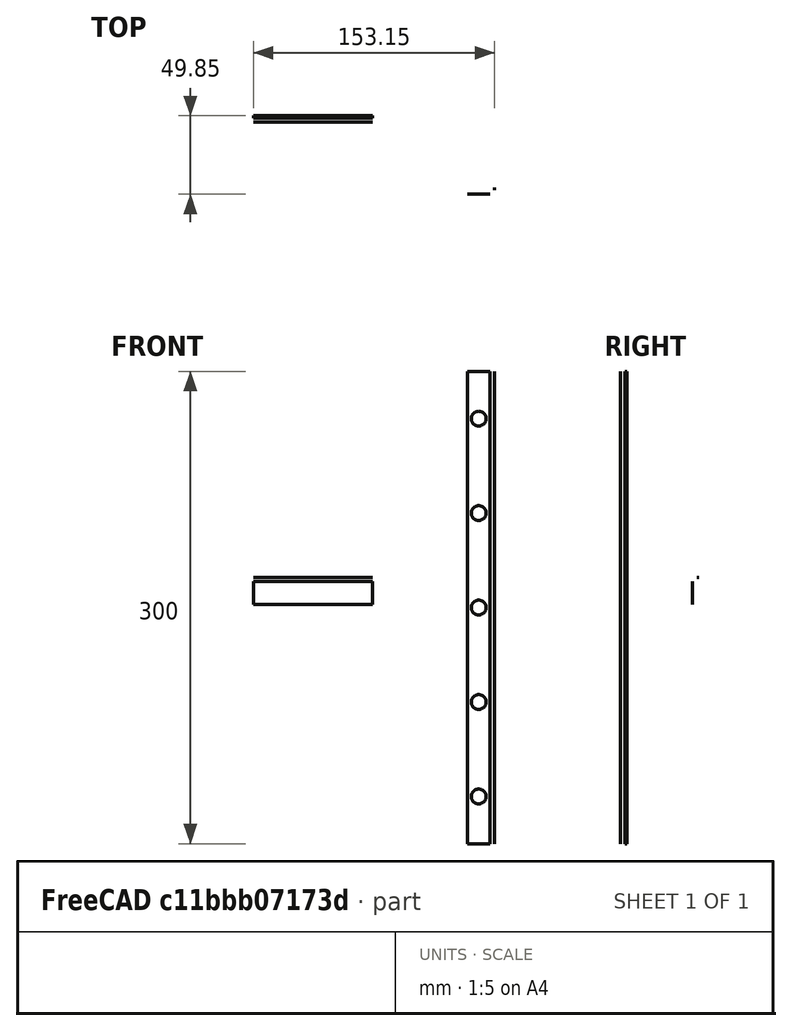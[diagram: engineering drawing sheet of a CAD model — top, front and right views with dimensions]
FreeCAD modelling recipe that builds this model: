
FCSTD DOCUMENT  (FreeCAD 2021.717R24301 +3842 (Git))
Label: Z-axis
License: Creative Commons Attribution
LicenseURL: http://creativecommons.org/licenses/by/4.0/
objects: App::FeaturePython×43, Part::FeaturePython×38, App::Link×14
note: 37 computed .brp shape members not serialized (recipe doc carries the construction recipe); baked Part::Feature solids carry a one-line shape summary decoded from their .brp
EXTERNAL_REF file=parts/Ballscrew.FCStd obj=Assembly002
EXTERNAL_REF file=parts/Z axis plates.FCStd obj=Assembly
EXTERNAL_REF file=parts/HGR20.FCStd obj=Assembly
EXTERNAL_REF file=parts/Z axis plates.FCStd obj=Assembly004
EXTERNAL_REF file=parts/NEMA23-76.FCStd obj=Assembly
EXTERNAL_REF file=parts/NEMA23-76.FCStd obj=Assembly001
EXTERNAL_REF file=parts/BallNut.FCStd obj=Assembly
EXTERNAL_REF file=parts/Z axis plates.FCStd obj=Assembly005
EXTERNAL_REF file=parts/HGH20CA.FCStd obj=Assembly
EXTERNAL_REF file=parts/HGH20CA.FCStd obj=Assembly001
EXTERNAL_REF file=parts/LimitSensor.FCStd obj=Assembly

FEATURE [App::Link] Link007  label="Ballscrew"
  AutoLinkLabel = true
  AutoPlacement = true
  LinkPlacement = pos=(0.026908,-40.4231,-69.025) rot=(-1,0,0;4.71239rad)
  LinkedObject = -> <external parts/Ballscrew.FCStd>#Assembly002
  Placement = pos=(0.026908,-40.4231,-69.025) rot=(-1,0,0;4.71239rad)
  SyncGroupVisibility = false
  _LinkVersion = 1
FEATURE [App::Link] Link  label="Backplate"
  AutoLinkLabel = true
  AutoPlacement = true
  LinkedObject = -> <external parts/Z axis plates.FCStd>#Assembly
  SyncGroupVisibility = false
  _LinkVersion = 1
FEATURE [App::Link] Link011  label="HGR20-300-R"
  AutoLinkLabel = true
  AutoPlacement = true
  LinkPlacement = pos=(54,-15.7,-6.00267e-11) rot=(1,0,0;1.5708rad)
  LinkedObject = -> <external parts/HGR20.FCStd>#Assembly
  Placement = pos=(54,-15.7,-6.00267e-11) rot=(1,0,0;1.5708rad)
  SyncGroupVisibility = false
  _LinkVersion = 1
FEATURE [App::Link] Link012  label="HGR20-300-L"
  AutoLinkLabel = true
  AutoPlacement = true
  LinkPlacement = pos=(-54,-15.7,-5.99982e-11) rot=(1,0,0;1.5708rad)
  LinkedObject = -> <external parts/HGR20.FCStd>#Assembly
  Placement = pos=(-54,-15.7,-5.99982e-11) rot=(1,0,0;1.5708rad)
  SyncGroupVisibility = false
  _LinkVersion = 1
FEATURE [App::Link] Link017  label="Motor Bracket"
  AutoLinkLabel = true
  AutoPlacement = true
  LinkedObject = -> <external parts/Z axis plates.FCStd>#Assembly004
  SyncGroupVisibility = false
  _LinkVersion = 1
FEATURE [App::Link] Link018  label="NEMA23-76"
  AutoLinkLabel = true
  AutoPlacement = true
  LinkPlacement = pos=(0,-40.7,158.85) rot=(0,0,1;3.14159rad)
  LinkedObject = -> <external parts/NEMA23-76.FCStd>#Assembly
  Placement = pos=(0,-40.7,158.85) rot=(0,0,1;3.14159rad)
  SyncGroupVisibility = false
  _LinkVersion = 1
FEATURE [App::Link] Link019  label="Coupling"
  AutoLinkLabel = true
  AutoPlacement = true
  LinkPlacement = pos=(3e-16,-40.7,131.25) rot=(0,1,0;3.14159rad)
  LinkedObject = -> <external parts/NEMA23-76.FCStd>#Assembly001
  Placement = pos=(3e-16,-40.7,131.25) rot=(0,1,0;3.14159rad)
  SyncGroupVisibility = false
  _LinkVersion = 1
FEATURE [App::Link] Link026  label="X-Nut"
  AutoLinkLabel = true
  AutoPlacement = true
  LinkPlacement = pos=(9.875,36.75,-60.65) rot=(-0.57735,-0.57735,-0.57735;2.0944rad)
  LinkedObject = -> <external parts/BallNut.FCStd>#Assembly
  Placement = pos=(9.875,36.75,-60.65) rot=(-0.57735,-0.57735,-0.57735;2.0944rad)
  SyncGroupVisibility = false
  _LinkVersion = 1
FEATURE [App::Link] Link027  label="Nut-shim-X"
  AutoLinkLabel = true
  AutoPlacement = true
  LinkPlacement = pos=(35.475,-6.6e-15,68.35) rot=(0,1,0;4.71239rad)
  LinkedObject = -> <external parts/Z axis plates.FCStd>#Assembly005
  Placement = pos=(35.475,-6.6e-15,68.35) rot=(0,1,0;4.71239rad)
  SyncGroupVisibility = false
  _LinkVersion = 1
FEATURE [App::Link] Link028  label="HGH20CA-L-B"
  AutoLinkLabel = true
  AutoPlacement = true
  LinkPlacement = pos=(-51.25,30,-130.5) rot=(0.57735,0.57735,-0.57735;2.0944rad)
  LinkedObject = -> <external parts/HGH20CA.FCStd>#Assembly
  Placement = pos=(-51.25,30,-130.5) rot=(0.57735,0.57735,-0.57735;2.0944rad)
  SyncGroupVisibility = false
  _LinkVersion = 1
FEATURE [App::Link] Link029  label="HGH20CA-R-B"
  AutoLinkLabel = true
  AutoPlacement = true
  LinkPlacement = pos=(51.25,30,-130.5) rot=(0.57735,0.57735,-0.57735;2.0944rad)
  LinkedObject = -> <external parts/HGH20CA.FCStd>#Assembly001
  Placement = pos=(51.25,30,-130.5) rot=(0.57735,0.57735,-0.57735;2.0944rad)
  SyncGroupVisibility = false
  _LinkVersion = 1
FEATURE [App::Link] Link030  label="HGH20CA-R-T"
  AutoLinkLabel = true
  AutoPlacement = true
  LinkPlacement = pos=(51.25,30,9.2) rot=(0.57735,-0.57735,0.57735;2.0944rad)
  LinkedObject = -> <external parts/HGH20CA.FCStd>#Assembly
  Placement = pos=(51.25,30,9.2) rot=(0.57735,-0.57735,0.57735;2.0944rad)
  SyncGroupVisibility = false
  _LinkVersion = 1
FEATURE [App::Link] Link031  label="HGH20CA-L-T"
  AutoLinkLabel = true
  AutoPlacement = true
  LinkPlacement = pos=(-51.25,30,9.2) rot=(0.57735,-0.57735,0.57735;2.0944rad)
  LinkedObject = -> <external parts/HGH20CA.FCStd>#Assembly001
  Placement = pos=(-51.25,30,9.2) rot=(0.57735,-0.57735,0.57735;2.0944rad)
  SyncGroupVisibility = false
  _LinkVersion = 1
FEATURE [App::Link] Link032  label="Limit sensor"
  AutoLinkLabel = true
  AutoPlacement = true
  LinkPlacement = pos=(-54,-61.85,152.5) rot=(0,0.707107,0.707107;3.14159rad)
  LinkedObject = -> <external parts/LimitSensor.FCStd>#Assembly
  Placement = pos=(-54,-61.85,152.5) rot=(0,0.707107,0.707107;3.14159rad)
  SyncGroupVisibility = false
  _LinkVersion = 1
FEATURE [Part::FeaturePython] Parts  # WARN: FeaturePython — macro-defined, semantics opaque (R4)
  Group = -> [Link007,Link,Link011,Link012,Link017,Link018,Link019,Link026,Link027,Link028,Link029,Link030,Link031,Link032]
  GroupMode = 0
  _LinkVersion = 1
FEATURE [Part::FeaturePython] Assembly  label="Z-axis assembly"  # WARN: FeaturePython — macro-defined, semantics opaque (R4)
  AutoRelax = true
  BuildShape = 0
  Freeze = false
  Group = -> [Constraints,Elements,Parts]
  Verbose = false
  _LinkVersion = 1
  _SolverType = 1
  _Version = 1
FEATURE [App::FeaturePython] Elements  # WARN: FeaturePython — macro-defined, semantics opaque (R4)
  Group = -> [Element,Element001,Element002,Element004,Element005,Element006,Element007,Element009,Element011,Element033,Element034,Element035,Element036,Element037,Element039,Element040,Element041,Element042,Element043,Element044,Element053,Element054,Element055,Element056,Element057,Element058,Element059,Element060,Element061,Element062,Element063,Element064,_Element,_Element001,Element065,_Element002]
  _LinkVersion = 1
FEATURE [Part::FeaturePython] Element  label="rail-tr@Backplate-Assembly"  # link proxy (typed FeaturePython)
  Detach = false
  LinkTransform = true
  LinkedObject = -> Link [1.$rail-tr.]
  _LinkVersion = 1
  _Parent = -> Elements
FEATURE [Part::FeaturePython] Element001  label="rail-bl@Backplate-Assembly"  # link proxy (typed FeaturePython)
  Detach = false
  LinkTransform = true
  LinkedObject = -> Link [1.$rail-tl.]
  _LinkVersion = 1
  _Parent = -> Elements
FEATURE [Part::FeaturePython] Element002  label="screw-br@Backplate-Assembly"  # link proxy (typed FeaturePython)
  Detach = false
  LinkTransform = true
  LinkedObject = -> Link [1.$screw-br.]
  _LinkVersion = 1
  _Parent = -> Elements
FEATURE [Part::FeaturePython] Element004  label="BP-mate@Ballscrew-Assembly"  # link proxy (typed FeaturePython)
  Detach = false
  LinkTransform = true
  LinkedObject = -> Link007 [1.$BP-mate.]
  _LinkVersion = 1
  _Parent = -> Elements
FEATURE [Part::FeaturePython] Element005  label="BP-mate-r@HGR20-300-Assembly"  # link proxy (typed FeaturePython)
  Detach = false
  LinkTransform = true
  LinkedObject = -> Link011 [1.$BP-mate-r.]
  _LinkVersion = 1
  _Parent = -> Elements
FEATURE [Part::FeaturePython] Element006  label="r-mate@HGR20-300-Assembly"  # link proxy (typed FeaturePython)
  Detach = false
  LinkTransform = true
  LinkedObject = -> Link011 [1.$r-mate.]
  _LinkVersion = 1
  _Parent = -> Elements
FEATURE [Part::FeaturePython] Element007  label="top-mate@HGR20-300-Assembly"  # link proxy (typed FeaturePython)
  Detach = false
  LinkTransform = true
  LinkedObject = -> Link011 [1.$top-mate.]
  _LinkVersion = 1
  _Parent = -> Elements
FEATURE [Part::FeaturePython] Element009  label="BP-mate-r@HGR20-300-Assembly001"  # link proxy (typed FeaturePython)
  Detach = false
  LinkTransform = true
  LinkedObject = -> Link012 [1.$BP-mate-r.]
  _LinkVersion = 1
  _Parent = -> Elements
FEATURE [Part::FeaturePython] Element011  label="Axis@Ballscrew-Assembly"  # link proxy (typed FeaturePython)
  Detach = false
  LinkTransform = true
  LinkedObject = -> Link007 [1.$Axis.]
  _LinkVersion = 1
  _Parent = -> Elements
FEATURE [Part::FeaturePython] Element033  label="point@HGR20-300-Assembly"  # link proxy (typed FeaturePython)
  Detach = false
  LinkTransform = true
  LinkedObject = -> Link011 [1.$point.]
  _LinkVersion = 1
  _Parent = -> Elements
FEATURE [App::FeaturePython] ElementLink  label="rail-tr@Backplate-Assembly"  # link proxy (typed FeaturePython)
  LinkTransform = true
  LinkedObject = -> Element
  _LinkVersion = 1
  _Parent = -> Constraint
FEATURE [App::FeaturePython] Constraint  label="Locked"  # WARN: FeaturePython — macro-defined, semantics opaque (R4)
  Disabled = false
  Group = -> [ElementLink]
  _ConstraintType = 0
  _LinkVersion = 1
  _Parent = -> Constraints
FEATURE [App::FeaturePython] ElementLink002  label="screw-br@Backplate-Assembly"  # link proxy (typed FeaturePython)
  LinkTransform = true
  LinkedObject = -> Element002
  Offset = pos=(0,0,0) rot=(0,0,1;3.14159rad)
  Placement = pos=(46,5.33e-14,-241.05) rot=(0,1,0;3.14159rad)
  _LinkVersion = 1
  _Parent = -> Constraint001
FEATURE [App::FeaturePython] ElementLink007  label="BP-mate@Ballscrew-Assembly"  # link proxy (typed FeaturePython)
  LinkTransform = true
  LinkedObject = -> Element004
  Offset = pos=(0,0,0) rot=(1,0,0;3.14159rad)
  Placement = pos=(-2.84e-14,-31.4,-241.05) rot=(1,0,0;3.14159rad)
  _LinkVersion = 1
  _Parent = -> Constraint001
FEATURE [App::FeaturePython] Constraint001  label="Attachment-BP-Screw"  # WARN: FeaturePython — macro-defined, semantics opaque (R4)
  Cascade = false
  Disabled = false
  Group = -> [ElementLink002,ElementLink007]
  Multiply = false
  _ConstraintType = 45
  _LinkVersion = 1
  _Parent = -> Constraints
FEATURE [App::FeaturePython] ElementLink008  label="rail-tr@Backplate-Assembly"  # link proxy (typed FeaturePython)
  LinkTransform = true
  LinkedObject = -> Element
  _LinkVersion = 1
  _Parent = -> Constraint002
FEATURE [App::FeaturePython] ElementLink009  label="BP-mate-r@HGR20-300-Assembly"  # link proxy (typed FeaturePython)
  LinkTransform = true
  LinkedObject = -> Element005
  Offset = pos=(0,0,0) rot=(0,0,1;3.14159rad)
  Placement = pos=(108,5.51e-14,240) rot=(0,1,0;3.14159rad)
  _LinkVersion = 1
  _Parent = -> Constraint002
FEATURE [App::FeaturePython] Constraint002  label="Attachment-BP-rail-r"  # WARN: FeaturePython — macro-defined, semantics opaque (R4)
  Cascade = false
  Disabled = false
  Group = -> [ElementLink008,ElementLink009]
  Multiply = false
  _ConstraintType = 45
  _LinkVersion = 1
  _Parent = -> Constraints
FEATURE [App::FeaturePython] ElementLink010  label="rail-bl@Backplate-Assembly"  # link proxy (typed FeaturePython)
  LinkTransform = true
  LinkedObject = -> Element001
  _LinkVersion = 1
  _Parent = -> Constraint003
FEATURE [App::FeaturePython] ElementLink011  label="BP-mate-r@HGR20-300-Assembly001"  # link proxy (typed FeaturePython)
  LinkTransform = true
  LinkedObject = -> Element009
  _LinkVersion = 1
  _Parent = -> Constraint003
FEATURE [App::FeaturePython] Constraint003  label="Attachment-BP-rail-l"  # WARN: FeaturePython — macro-defined, semantics opaque (R4)
  Cascade = false
  Disabled = false
  Group = -> [ElementLink010,ElementLink011]
  Multiply = false
  _ConstraintType = 45
  _LinkVersion = 1
  _Parent = -> Constraints
FEATURE [App::FeaturePython] Constraints  # WARN: FeaturePython — macro-defined, semantics opaque (R4)
  Group = -> [Constraint,Constraint001,Constraint002,Constraint003,Constraint016,Constraint017,Constraint018,Constraint019,Constraint020,Constraint023,Constraint025,Constraint026,Constraint027,Constraint028]
  _LinkVersion = 1
  _Version = 1
FEATURE [Part::FeaturePython] Element034  label="bp-mate@Motor Bracket Assembly"  # link proxy (typed FeaturePython)
  Detach = false
  LinkTransform = true
  LinkedObject = -> Link017 [1.$bp-mate.]
  _LinkVersion = 1
  _Parent = -> Elements
FEATURE [Part::FeaturePython] Element035  label="Motor-mate@Motor Bracket Assembly"  # link proxy (typed FeaturePython)
  Detach = false
  LinkTransform = true
  LinkedObject = -> Link017 [1.$Motor-mate.]
  _LinkVersion = 1
  _Parent = -> Elements
FEATURE [Part::FeaturePython] Element036  label="bracket-mate@Backplate-Assembly"  # link proxy (typed FeaturePython)
  Detach = false
  LinkTransform = true
  LinkedObject = -> Link [1.$bracket-mate.]
  _LinkVersion = 1
  _Parent = -> Elements
FEATURE [App::FeaturePython] Constraint016  label="Attachment-BP-bracket"  # WARN: FeaturePython — macro-defined, semantics opaque (R4)
  Cascade = false
  Disabled = false
  Group = -> [ElementLink036,ElementLink037]
  Multiply = false
  _ConstraintType = 45
  _LinkVersion = 1
  _Parent = -> Constraints
FEATURE [App::FeaturePython] ElementLink036  label="bracket-mate@Backplate-Assembly"  # link proxy (typed FeaturePython)
  LinkTransform = true
  LinkedObject = -> Element036
  _LinkVersion = 1
  _Parent = -> Constraint016
FEATURE [App::FeaturePython] ElementLink037  label="bp-mate@Motor Bracket Assembly"  # link proxy (typed FeaturePython)
  LinkTransform = true
  LinkedObject = -> Element034
  _LinkVersion = 1
  _Parent = -> Constraint016
FEATURE [Part::FeaturePython] Element037  label="bracket-mate@NEMA23-76-Assembly"  # link proxy (typed FeaturePython)
  Detach = false
  LinkTransform = true
  LinkedObject = -> Link018 [1.$bracket-mate.]
  _LinkVersion = 1
  _Parent = -> Elements
FEATURE [App::FeaturePython] Constraint017  label="Attachment-motor"  # WARN: FeaturePython — macro-defined, semantics opaque (R4)
  Cascade = false
  Disabled = false
  Group = -> [ElementLink038,ElementLink039]
  Multiply = false
  _ConstraintType = 45
  _LinkVersion = 1
  _Parent = -> Constraints
FEATURE [App::FeaturePython] ElementLink038  label="bracket-mate@NEMA23-76-Assembly"  # link proxy (typed FeaturePython)
  LinkTransform = true
  LinkedObject = -> Element037
  Offset = pos=(0,0,0) rot=(1,0,0;3.14159rad)
  Placement = pos=(-1e-14,-81.4,317.7) rot=(1,0,0;3.14159rad)
  _LinkVersion = 1
  _Parent = -> Constraint017
FEATURE [App::FeaturePython] ElementLink039  label="Motor-mate@Motor Bracket Assembly"  # link proxy (typed FeaturePython)
  LinkTransform = true
  LinkedObject = -> Element035
  _LinkVersion = 1
  _Parent = -> Constraint017
FEATURE [Part::FeaturePython] Element039  label="coupling-mate@NEMA23-76-Assembly"  # link proxy (typed FeaturePython)
  Detach = false
  LinkTransform = true
  LinkedObject = -> Link018 [1.$coupling-mate.]
  _LinkVersion = 1
  _Parent = -> Elements
FEATURE [Part::FeaturePython] Element040  label="motor-mate@Coupling-Assembly"  # link proxy (typed FeaturePython)
  Detach = false
  LinkTransform = true
  LinkedObject = -> Link019 [1.$motor-mate.]
  _LinkVersion = 1
  _Parent = -> Elements
FEATURE [App::FeaturePython] Constraint018  label="Attachment-coupling"  # WARN: FeaturePython — macro-defined, semantics opaque (R4)
  Cascade = false
  Disabled = false
  Group = -> [ElementLink040,ElementLink041]
  Multiply = false
  _ConstraintType = 45
  _LinkVersion = 1
  _Parent = -> Constraints
FEATURE [App::FeaturePython] ElementLink040  label="coupling-mate@NEMA23-76-Assembly"  # link proxy (typed FeaturePython)
  LinkTransform = true
  LinkedObject = -> Element039
  _LinkVersion = 1
  _Parent = -> Constraint018
FEATURE [App::FeaturePython] ElementLink041  label="motor-mate@Coupling-Assembly"  # link proxy (typed FeaturePython)
  LinkTransform = true
  LinkedObject = -> Element040
  _LinkVersion = 1
  _Parent = -> Constraint018
FEATURE [Part::FeaturePython] Element041  label="X-cart-BP-br@HGH20CA-R-Assembly002"  # link proxy (typed FeaturePython)
  Detach = false
  LinkTransform = true
  LinkedObject = -> Link029 [1.$shim-br.]
  _LinkVersion = 1
  _Parent = -> Elements
FEATURE [Part::FeaturePython] Element042  label="X-cart-BP-bl@HGH20CA-L-Assembly002"  # link proxy (typed FeaturePython)
  Detach = false
  LinkTransform = true
  LinkedObject = -> Link028 [1.$shim-tr.]
  _LinkVersion = 1
  _Parent = -> Elements
FEATURE [Part::FeaturePython] Element043  label="x-cart-bl@Backplate-Assembly"  # link proxy (typed FeaturePython)
  Detach = false
  LinkTransform = true
  LinkedObject = -> Link [1.$x-cart-bl.]
  _LinkVersion = 1
  _Parent = -> Elements
FEATURE [Part::FeaturePython] Element044  label="x-cart-br@Backplate-Assembly"  # link proxy (typed FeaturePython)
  Detach = false
  LinkTransform = true
  LinkedObject = -> Link [1.$x-cart-br.]
  _LinkVersion = 1
  _Parent = -> Elements
FEATURE [App::FeaturePython] Constraint019  label="Attachment-x-cart-br"  # WARN: FeaturePython — macro-defined, semantics opaque (R4)
  Cascade = false
  Disabled = false
  Group = -> [ElementLink042,ElementLink043]
  Multiply = false
  _ConstraintType = 45
  _LinkVersion = 1
  _Parent = -> Constraints
FEATURE [App::FeaturePython] ElementLink042  label="x-cart-br@Backplate-Assembly"  # link proxy (typed FeaturePython)
  LinkTransform = true
  LinkedObject = -> Element044
  Offset = pos=(0,0,0) rot=(1,0,0;3.14159rad)
  Placement = pos=(0,4.71e-14,-293) rot=(1,0,0;3.14159rad)
  _LinkVersion = 1
  _Parent = -> Constraint019
FEATURE [App::FeaturePython] ElementLink043  label="X-cart-BP-br@HGH20CA-R-Assembly002"  # link proxy (typed FeaturePython)
  LinkTransform = true
  LinkedObject = -> Element041
  Offset = pos=(0,0,0) rot=(0,0,1;4.71239rad)
  Placement = pos=(179.75,-9.02e-14,-113.25) rot=(0,1,0;1.5708rad)
  _LinkVersion = 1
  _Parent = -> Constraint019
FEATURE [App::FeaturePython] Constraint020  label="Attachment-x-cart-bl"  # WARN: FeaturePython — macro-defined, semantics opaque (R4)
  Cascade = false
  Disabled = false
  Group = -> [ElementLink044,ElementLink045]
  Multiply = false
  _ConstraintType = 45
  _LinkVersion = 1
  _Parent = -> Constraints
FEATURE [App::FeaturePython] ElementLink044  label="x-cart-bl@Backplate-Assembly"  # link proxy (typed FeaturePython)
  LinkTransform = true
  LinkedObject = -> Element043
  Offset = pos=(0,0,0) rot=(1,0,0;3.14159rad)
  Placement = pos=(0,4.71e-14,-293) rot=(1,0,0;3.14159rad)
  _LinkVersion = 1
  _Parent = -> Constraint020
FEATURE [App::FeaturePython] ElementLink045  label="X-cart-BP-bl@HGH20CA-L-Assembly002"  # link proxy (typed FeaturePython)
  LinkTransform = true
  LinkedObject = -> Element042
  Offset = pos=(0,0,0) rot=(0,0,1;4.71239rad)
  Placement = pos=(113.25,-3.99e-14,-179.75) rot=(0,1,0;1.5708rad)
  _LinkVersion = 1
  _Parent = -> Constraint020
FEATURE [Part::FeaturePython] Element053  label="x-cart-BP-tl@HGH20CA-R-Assembly002"  # link proxy (typed FeaturePython)
  Detach = false
  LinkTransform = true
  LinkedObject = -> Link030 [1.$shim-tr.]
  _LinkVersion = 1
  _Parent = -> Elements
FEATURE [Part::FeaturePython] Element054  label="x-cart-BP-tr@HGH20CA-R-Assembly002"  # link proxy (typed FeaturePython)
  Detach = false
  LinkTransform = true
  LinkedObject = -> Link030 [1.$shim-tr.]
  _LinkVersion = 1
  _Parent = -> Elements
FEATURE [Part::FeaturePython] Element055  label="x-cart-tl@Backplate-Assembly"  # link proxy (typed FeaturePython)
  Detach = false
  LinkTransform = true
  LinkedObject = -> Link [1.$x-cart-tl.]
  _LinkVersion = 1
  _Parent = -> Elements
FEATURE [Part::FeaturePython] Element056  label="x-cart-tr@Backplate-Assembly"  # link proxy (typed FeaturePython)
  Detach = false
  LinkTransform = true
  LinkedObject = -> Link [1.$x-cart-tr.]
  _LinkVersion = 1
  _Parent = -> Elements
FEATURE [App::FeaturePython] Constraint023  label="Attachment-x-cart-tr"  # WARN: FeaturePython — macro-defined, semantics opaque (R4)
  Cascade = false
  Disabled = false
  Group = -> [ElementLink051,ElementLink052]
  Multiply = false
  _ConstraintType = 45
  _LinkVersion = 1
  _Parent = -> Constraints
FEATURE [App::FeaturePython] ElementLink051  label="x-cart-tr@Backplate-Assembly"  # link proxy (typed FeaturePython)
  LinkTransform = true
  LinkedObject = -> Element056
  Offset = pos=(0,0,0) rot=(1,0,0;3.14159rad)
  Placement = pos=(0,-8.1e-15,50.4) rot=(1,0,0;3.14159rad)
  _LinkVersion = 1
  _Parent = -> Constraint023
FEATURE [App::FeaturePython] ElementLink052  label="x-cart-BP-tr@HGH20CA-R-Assembly002"  # link proxy (typed FeaturePython)
  LinkTransform = true
  LinkedObject = -> Element054
  Offset = pos=(0,0,0) rot=(0,0,1;1.5708rad)
  Placement = pos=(58.45,2.7e-15,-8.05) rot=(0,-1,0;1.5708rad)
  _LinkVersion = 1
  _Parent = -> Constraint023
FEATURE [Part::FeaturePython] Element057  label="x-top-rail-side-mate@HGH20CA-R-Assembly001"  # link proxy (typed FeaturePython)
  Detach = false
  LinkTransform = true
  LinkedObject = -> Link031 [1.$side-mate.]
  _LinkVersion = 1
  _Parent = -> Elements
FEATURE [Part::FeaturePython] Element058  label="x-top-rail-top-mate@HGH20CA-R-Assembly001"  # link proxy (typed FeaturePython)
  Detach = false
  LinkTransform = true
  LinkedObject = -> Link031 [1.$top-mate.]
  _LinkVersion = 1
  _Parent = -> Elements
FEATURE [Part::FeaturePython] Element059  label="x-nut-BP-mate@NUT Assembly001"  # link proxy (typed FeaturePython)
  Detach = false
  LinkTransform = true
  LinkedObject = -> Link026 [1.$shim-mate.]
  _LinkVersion = 1
  _Parent = -> Elements
FEATURE [Part::FeaturePython] Element060  label="x-nut-mate@Backplate-Assembly"  # link proxy (typed FeaturePython)
  Detach = false
  LinkTransform = true
  LinkedObject = -> Link [1.$x-nut-mate.]
  _LinkVersion = 1
  _Parent = -> Elements
FEATURE [App::FeaturePython] Constraint025  label="Attachment-X-Nut-shim"  # WARN: FeaturePython — macro-defined, semantics opaque (R4)
  Cascade = false
  Disabled = false
  Group = -> [ElementLink056,ElementLink057]
  Multiply = false
  _ConstraintType = 45
  _LinkVersion = 1
  _Parent = -> Constraints
FEATURE [App::FeaturePython] ElementLink056  label="x-nut-BP-mate@NUT Assembly001"  # link proxy (typed FeaturePython)
  LinkTransform = true
  LinkedObject = -> Element059
  _LinkVersion = 1
  _Parent = -> Constraint025
FEATURE [Part::FeaturePython] Element061  label="X-nut-Axis@NUT Assembly001"  # link proxy (typed FeaturePython)
  Detach = false
  LinkTransform = true
  LinkedObject = -> Link026 [1.$Axis.]
  _LinkVersion = 1
  _Parent = -> Elements
FEATURE [Part::FeaturePython] Element062  label="x-cart-point@HGH20CA-R-Assembly001"  # link proxy (typed FeaturePython)
  Detach = false
  LinkTransform = true
  LinkedObject = -> Link031 [1.$point.]
  _LinkVersion = 1
  _Parent = -> Elements
FEATURE [Part::FeaturePython] Element063  label="bp-mate@Nut-shim-X-Assembly"  # link proxy (typed FeaturePython)
  Detach = false
  LinkTransform = true
  LinkedObject = -> Link027 [1.$bp-mate.]
  _LinkVersion = 1
  _Parent = -> Elements
FEATURE [Part::FeaturePython] Element064  label="nut-mate@Nut-shim-X-Assembly"  # link proxy (typed FeaturePython)
  Detach = false
  LinkTransform = true
  LinkedObject = -> Link027 [1.$nut-mate.]
  _LinkVersion = 1
  _Parent = -> Elements
FEATURE [App::FeaturePython] ElementLink057  label="nut-mate@Nut-shim-X-Assembly"  # link proxy (typed FeaturePython)
  LinkTransform = true
  LinkedObject = -> Element064
  _LinkVersion = 1
  _Parent = -> Constraint025
FEATURE [App::FeaturePython] Constraint026  label="Attachment001"  # WARN: FeaturePython — macro-defined, semantics opaque (R4)
  Cascade = false
  Disabled = false
  Group = -> [ElementLink058,ElementLink059]
  Multiply = false
  _ConstraintType = 45
  _LinkVersion = 1
  _Parent = -> Constraints
FEATURE [App::FeaturePython] ElementLink058  label="bp-mate@Nut-shim-X-Assembly"  # link proxy (typed FeaturePython)
  LinkTransform = true
  LinkedObject = -> Element063
  Offset = pos=(0,0,0) rot=(1,0,0;3.14159rad)
  Placement = pos=(-6,-3.5e-15,0) rot=(0,0,1;3.14159rad)
  _LinkVersion = 1
  _Parent = -> Constraint026
FEATURE [App::FeaturePython] ElementLink059  label="x-nut-mate@Backplate-Assembly"  # link proxy (typed FeaturePython)
  LinkTransform = true
  LinkedObject = -> Element060
  Offset = pos=(0,0,0) rot=(0,0,1;4.71239rad)
  Placement = pos=(-43.65,8.4e-15,-37.65) rot=(0,-1,0;1.5708rad)
  _LinkVersion = 1
  _Parent = -> Constraint026
FEATURE [Part::FeaturePython] _Element  label="x-cart-tl@Backplate-Assembly001"  # link proxy (typed FeaturePython)
  Detach = false
  LinkTransform = true
  LinkedObject = -> Link [1.$x-cart-tl.]
  _LinkVersion = 1
  _Parent = -> Elements
FEATURE [App::FeaturePython] Constraint027  label="Attachment-x-cart-tl"  # WARN: FeaturePython — macro-defined, semantics opaque (R4)
  Cascade = false
  Disabled = false
  Group = -> [ElementLink060,ElementLink061]
  Multiply = false
  _ConstraintType = 45
  _LinkVersion = 1
  _Parent = -> Constraints
FEATURE [App::FeaturePython] ElementLink060  label="x-cart-tl@Backplate-Assembly"  # link proxy (typed FeaturePython)
  LinkTransform = true
  LinkedObject = -> Element055
  Offset = pos=(0,0,0) rot=(1,0,0;3.14159rad)
  Placement = pos=(0,3.1e-15,50.4) rot=(1,0,0;3.14159rad)
  _LinkVersion = 1
  _Parent = -> Constraint027
FEATURE [App::FeaturePython] ElementLink061  label="shim-br@HGH20CA-R-Assembly"  # link proxy (typed FeaturePython)
  LinkTransform = true
  LinkedObject = -> _Element001
  Offset = pos=(0,0,0) rot=(0,0,1;1.5708rad)
  Placement = pos=(-8.05,1.3e-14,58.45) rot=(0,-1,0;1.5708rad)
  _LinkVersion = 1
  _Parent = -> Constraint027
FEATURE [Part::FeaturePython] _Element001  label="shim-br@HGH20CA-R-Assembly"  # link proxy (typed FeaturePython)
  Detach = false
  LinkTransform = true
  LinkedObject = -> Link031 [1.$shim-br.]
  _LinkVersion = 1
  _Parent = -> Elements
FEATURE [Part::FeaturePython] Element065  label="limit-mate@Motor Bracket Assembly"  # link proxy (typed FeaturePython)
  Detach = false
  LinkTransform = true
  LinkedObject = -> Link017 [1.$limit-mate.]
  _LinkVersion = 1
  _Parent = -> Elements
FEATURE [App::FeaturePython] Constraint028  label="Attachment-limit-sensor"  # WARN: FeaturePython — macro-defined, semantics opaque (R4)
  Cascade = false
  Disabled = false
  Group = -> [ElementLink062,ElementLink063]
  Multiply = false
  _ConstraintType = 45
  _LinkVersion = 1
  _Parent = -> Constraints
FEATURE [App::FeaturePython] ElementLink062  label="limit-mate@Motor Bracket Assembly"  # link proxy (typed FeaturePython)
  LinkTransform = true
  LinkedObject = -> Element065
  Offset = pos=(0,0,0) rot=(0,0,1;3.14159rad)
  Placement = pos=(-96,-102.7,-5.68e-14) rot=(0,0,1;3.14159rad)
  _LinkVersion = 1
  _Parent = -> Constraint028
FEATURE [App::FeaturePython] ElementLink063  label="mate l@Limit sensor Assembly"  # link proxy (typed FeaturePython)
  LinkTransform = true
  LinkedObject = -> _Element002
  Offset = pos=(0,0,0) rot=(1,0,0;3.14159rad)
  Placement = pos=(0,-102.7,305) rot=(1,0,0;3.14159rad)
  _LinkVersion = 1
  _Parent = -> Constraint028
FEATURE [Part::FeaturePython] _Element002  label="mate l@Limit sensor Assembly"  # link proxy (typed FeaturePython)
  Detach = false
  LinkTransform = true
  LinkedObject = -> Link032 [1.$mate l.]
  _LinkVersion = 1
  _Parent = -> Elements

RESOLVED EXTERNAL PARTS (link-assembly join: the EXTERNAL_REF files above that resolve inside this repo's crawl, each included once):
---- part parts/BallNut.FCStd = doc fcstd_aec63517059e ----
FCSTD DOCUMENT  (FreeCAD 2021.614R24301 +3747 (Git))
Label: BallNut
License: Creative Commons Attribution
LicenseURL: http://creativecommons.org/licenses/by/4.0/
objects: App::FeaturePython×25, Part::FeaturePython×22, Sketcher::SketchObject×9, PartDesign::Pocket×6, App::LinkElement×6, PartDesign::Pad×3, App::Link×3, PartDesign::Chamfer×2, PartDesign::Body×2, PartDesign::Plane×1, PartDesign::Line×1, App::DocumentObjectGroup×1
note: 67 computed .brp shape members not serialized (recipe doc carries the construction recipe); baked Part::Feature solids carry a one-line shape summary decoded from their .brp

FEATURE [Sketcher::SketchObject] Sketch
  FullyConstrained = true
  MapMode = 5
  Placement = pos=(0,0,0) rot=(1,0,0;1.5708rad)
  Support = -> [XZ_Plane]
  sketch-geometry (9):
    g0: Circle CenterX=0 CenterY=0 CenterZ=0 NormalX=0 NormalY=0 NormalZ=1 AngleXU=0 Radius=14
    g1: LineSegment StartX=-26.125 StartY=-20 StartZ=0 EndX=26.125 EndY=-20 EndZ=0
    g2: LineSegment StartX=26.125 StartY=-20 StartZ=0 EndX=26.125 EndY=8 EndZ=0
    g3: LineSegment StartX=26.125 StartY=8 StartZ=0 EndX=14 EndY=20 EndZ=0
    g4: LineSegment StartX=14 StartY=20 StartZ=0 EndX=-14 EndY=20 EndZ=0
    g5: LineSegment StartX=-14 StartY=20 StartZ=0 EndX=-26.125 EndY=8 EndZ=0
    g6: LineSegment StartX=-26.125 StartY=8 StartZ=0 EndX=-26.125 EndY=-20 EndZ=0
    g7: GeomPoint [constr] X=0 Y=-20 Z=0
    g8: GeomPoint [constr] X=2e-16 Y=20 Z=0
  constraints (21):
    c: Coincident(g0,g-1)
    c: Horizontal(g1)
    c: Coincident(g1,g2)
    c: Vertical(g2)
    c: Coincident(g2,g3)
    c: Coincident(g3,g4)
    c: Horizontal(g4)
    c: Coincident(g4,g5)
    c: Coincident(g5,g6)
    c: Coincident(g6,g1)
    c: Vertical(g6)
    c: Horizontal(g5,g2)
    c: PointOnObject(g7,g-2)
    c: Symmetric(g4,g3,g8)
    c: Symmetric(g1,g1,g7)
    c: DistanceY(g1,g3) = 40
    c: Symmetric(g8,g7,g0)
    c: DistanceX(g1,g1) = 52.25
    c: DistanceY(g2,g2) = 28
    c: DistanceX(g4,g4) = 28
    c: Diameter(g0) = 28
FEATURE [PartDesign::Pad] Pad
  ClaimChildren = false
  Direction = (1,1,1)
  Fit = 0
  FitJoin = 0
  InnerFit = 0
  InnerFitJoin = 0
  InnerTaperAngle = 0
  InnerTaperAngleRev = 0
  Length = 40.25
  Length2 = 100
  Linearize = true
  Midplane = true
  NewSolid = false
  Placement = pos=(0,0,0) rot=(1,0,0;1.5708rad)
  Profile = -> Sketch
  Refine = true
  Suppress = false
  Type = 0
FEATURE [Sketcher::SketchObject] Sketch001
  FullyConstrained = true
  MapMode = 5
  Placement = pos=(0,-20.125,4.4e-15) rot=(1,0,0;1.5708rad)
  Support = -> [Pad]
  sketch-geometry (8):
    g0: Circle CenterX=-19 CenterY=0 CenterZ=0 NormalX=0 NormalY=0 NormalZ=1 AngleXU=0 Radius=2.1
    g1: Circle CenterX=19 CenterY=0 CenterZ=0 NormalX=0 NormalY=0 NormalZ=1 AngleXU=0 Radius=2.1
    g2: Circle CenterX=13.435 CenterY=-13.435 CenterZ=0 NormalX=0 NormalY=0 NormalZ=1 AngleXU=0 Radius=2.1
    g3: Circle CenterX=-13.435 CenterY=-13.435 CenterZ=0 NormalX=0 NormalY=0 NormalZ=1 AngleXU=0 Radius=2.1
    g4: Circle CenterX=-13.435 CenterY=13.435 CenterZ=0 NormalX=0 NormalY=0 NormalZ=1 AngleXU=0 Radius=2.1
    g5: Circle CenterX=13.435 CenterY=13.435 CenterZ=0 NormalX=0 NormalY=0 NormalZ=1 AngleXU=0 Radius=2.1
    g6: Circle [constr] CenterX=0 CenterY=0 CenterZ=0 NormalX=0 NormalY=0 NormalZ=1 AngleXU=0 Radius=19
    g7: LineSegment [constr] StartX=0 StartY=0 StartZ=0 EndX=13.435 EndY=13.435 EndZ=0
  constraints (22):
    c: PointOnObject(g0,g-1)
    c: PointOnObject(g1,g-1)
    c: Coincident(g6,g-1)
    c: Diameter(g6) = 38
    c: Equal(g1,g5)
    c: Equal(g5,g4)
    c: Equal(g4,g0)
    c: Equal(g0,g3)
    c: Equal(g3,g2)
    c: PointOnObject(g5,g6)
    c: PointOnObject(g4,g6)
    c: PointOnObject(g0,g6)
    c: PointOnObject(g1,g6)
    c: PointOnObject(g2,g6)
    c: PointOnObject(g3,g6)
    c: Vertical(g4,g3)
    c: Vertical(g5,g2)
    c: Horizontal(g4,g5)
    c: Diameter(g4) = 4.2
    c: Coincident(g7,g6)
    c: Coincident(g7,g5)
    c: Angle(g-1,g7) = 0.785398
FEATURE [PartDesign::Pocket] Pocket
  BaseFeature = -> Pad
  ClaimChildren = false
  Fit = 0
  FitJoin = 0
  InnerFit = 0
  InnerFitJoin = 0
  InnerTaperAngle = 0
  InnerTaperAngleRev = 0
  Length = 16
  Length2 = 100
  Linearize = true
  NewSolid = false
  Placement = pos=(0,0,0) rot=(1,0,0;1.5708rad)
  Profile = -> Sketch001
  Refine = true
  Suppress = false
  Type = 0
FEATURE [Sketcher::SketchObject] Sketch002
  FullyConstrained = true
  MapMode = 5
  Placement = pos=(0,-8.8e-15,-20) rot=(1,0,0;3.14159rad)
  Support = -> [Pocket]
  sketch-geometry (4):
    g0: Circle CenterX=-20 CenterY=12 CenterZ=0 NormalX=0 NormalY=0 NormalZ=1 AngleXU=0 Radius=2.1
    g1: Circle CenterX=20 CenterY=12 CenterZ=0 NormalX=0 NormalY=0 NormalZ=1 AngleXU=0 Radius=2.1
    g2: Circle CenterX=-20 CenterY=-12 CenterZ=0 NormalX=0 NormalY=0 NormalZ=1 AngleXU=0 Radius=2.1
    g3: Circle CenterX=20 CenterY=-12 CenterZ=0 NormalX=0 NormalY=0 NormalZ=1 AngleXU=0 Radius=2.1
  constraints (11):
    c: Equal(g3,g1)
    c: Equal(g1,g0)
    c: Equal(g0,g2)
    c: Diameter(g0) = 4.2
    c: Symmetric(g0,g3,g-1)
    c: Horizontal(g0,g1)
    c: Vertical(g0,g2)
    c: Vertical(g1,g3)
    c: Horizontal(g3,g2)
    c: DistanceY(g2,g0) = 24
    c: DistanceX(g0,g1) = 40
FEATURE [PartDesign::Pocket] Pocket001
  BaseFeature = -> Pocket
  ClaimChildren = false
  Fit = 0
  FitJoin = 0
  InnerFit = 0
  InnerFitJoin = 0
  InnerTaperAngle = 0
  InnerTaperAngleRev = 0
  Length = 16
  Length2 = 100
  Linearize = true
  NewSolid = false
  Placement = pos=(0,0,0) rot=(1,0,0;1.5708rad)
  Profile = -> Sketch002
  Refine = true
  Suppress = false
  Type = 0
FEATURE [PartDesign::Chamfer] Chamfer
  Angle = 45
  Base = -> Pocket001 [Edge10,Edge2,Edge15,Edge14,Edge13,Edge12,Edge37,Edge9,Edge1,Edge4,Edge28,Edge38,Edge16,Edge3,Edge17,Edge19,Edge20,Edge18,Edge11,Edge25,Edge22,Edge21,Edge24,Edge26,Edge27,Edge23,Edge5,Edge7,Edge8,Edge6]
  BaseFeature = -> Pocket001
  ChamferType = 0
  FlipDirection = false
  NewSolid = false
  Placement = pos=(0,0,0) rot=(1,0,0;1.5708rad)
  Refine = true
  Size = 1
  Size2 = 1
  SupportTransform = false
  Suppress = false
FEATURE [Sketcher::SketchObject] Sketch003
  FullyConstrained = true
  MapMode = 5
  Placement = pos=(0,0,0) rot=(1,0,0;1.5708rad)
  Support = -> [XZ_Plane001]
  sketch-geometry (1):
    g0: Circle CenterX=0 CenterY=0 CenterZ=0 NormalX=0 NormalY=0 NormalZ=1 AngleXU=0 Radius=14
  constraints (2):
    c: Coincident(g0,g-1)
    c: Diameter(g0) = 28
FEATURE [PartDesign::Pad] Pad001
  ClaimChildren = false
  Direction = (1,1,1)
  Fit = 0
  FitJoin = 0
  InnerFit = 0
  InnerFitJoin = 0
  InnerTaperAngle = 0
  InnerTaperAngleRev = 0
  Length = 32
  Length2 = 100
  Linearize = true
  Midplane = true
  NewSolid = false
  Placement = pos=(0,0,0) rot=(1,0,0;1.5708rad)
  Profile = -> Sketch003
  Refine = true
  Suppress = false
  Type = 0
FEATURE [Sketcher::SketchObject] Sketch004
  FullyConstrained = true
  MapMode = 5
  Placement = pos=(0,-16,3.5e-15) rot=(1,0,0;1.5708rad)
  Support = -> [Pad001]
  sketch-geometry (12):
    g0: ArcOfCircle CenterX=0 CenterY=0 CenterZ=0 NormalX=0 NormalY=0 NormalZ=1 AngleXU=0 Radius=24 StartAngle=2.15648 EndAngle=4.1267
    g1: Circle [constr] CenterX=0 CenterY=0 CenterZ=0 NormalX=0 NormalY=0 NormalZ=1 AngleXU=0 Radius=19
    g2: LineSegment StartX=-13.2665 StartY=20 StartZ=0 EndX=13.2665 EndY=20 EndZ=0
    g3: LineSegment StartX=-13.2665 StartY=-20 StartZ=0 EndX=13.2665 EndY=-20 EndZ=0
    g4: ArcOfCircle CenterX=0 CenterY=0 CenterZ=0 NormalX=0 NormalY=0 NormalZ=1 AngleXU=0 Radius=24 StartAngle=5.29807 EndAngle=7.2683
    g5: Circle CenterX=-19 CenterY=0 CenterZ=0 NormalX=0 NormalY=0 NormalZ=1 AngleXU=0 Radius=2.75
    g6: Circle CenterX=-13.435 CenterY=13.435 CenterZ=0 NormalX=0 NormalY=0 NormalZ=1 AngleXU=0 Radius=2.75
    g7: Circle CenterX=13.435 CenterY=13.435 CenterZ=0 NormalX=0 NormalY=0 NormalZ=1 AngleXU=0 Radius=2.75
    g8: Circle CenterX=19 CenterY=0 CenterZ=0 NormalX=0 NormalY=0 NormalZ=1 AngleXU=0 Radius=2.75
    g9: Circle CenterX=13.435 CenterY=-13.435 CenterZ=0 NormalX=0 NormalY=0 NormalZ=1 AngleXU=0 Radius=2.75
    g10: Circle CenterX=-13.435 CenterY=-13.435 CenterZ=0 NormalX=0 NormalY=0 NormalZ=1 AngleXU=0 Radius=2.75
    g11: LineSegment [constr] StartX=0 StartY=0 StartZ=0 EndX=13.435 EndY=13.435 EndZ=0
  constraints (34):
    c: Coincident(g0,g-1)
    c: Coincident(g1,g0)
    c: Diameter(g1) = 38
    c: Diameter(g0) = 48
    c: Horizontal(g2)
    c: Horizontal(g3)
    c: Symmetric(g3,g2,g0)
    c: DistanceY(g3,g2) = 40
    c: Coincident(g0,g2)
    c: Coincident(g4,g2)
    c: Equal(g0,g4)
    c: Coincident(g0,g3)
    c: PointOnObject(g4,g3)
    c: Coincident(g0,g4)
    c: PointOnObject(g5,g1)
    c: PointOnObject(g6,g1)
    c: PointOnObject(g7,g1)
    c: PointOnObject(g8,g1)
    c: PointOnObject(g9,g1)
    c: PointOnObject(g8,g-1)
    c: PointOnObject(g5,g-1)
    c: PointOnObject(g10,g1)
    c: Vertical(g10,g6)
    c: Vertical(g7,g9)
    c: Horizontal(g7,g6)
    c: Equal(g7,g8)
    c: Equal(g8,g9)
    c: Equal(g9,g6)
    c: Equal(g6,g5)
    c: Equal(g5,g10)
    c: Diameter(g6) = 5.5
    c: Coincident(g11,g0)
    c: Coincident(g11,g7)
    c: Angle(g-1,g11) = 0.785398
FEATURE [PartDesign::Pad] Pad002
  BaseFeature = -> Pad001
  ClaimChildren = false
  Direction = (1,1,1)
  Fit = 0
  FitJoin = 0
  InnerFit = 0
  InnerFitJoin = 0
  InnerTaperAngle = 0
  InnerTaperAngleRev = 0
  Length = 10
  Length2 = 100
  Linearize = true
  NewSolid = false
  Placement = pos=(0,0,0) rot=(1,0,0;1.5708rad)
  Profile = -> Sketch004
  Refine = true
  Suppress = false
  Type = 0
FEATURE [Sketcher::SketchObject] Sketch005
  FullyConstrained = true
  MapMode = 5
  Placement = pos=(0,-26,2.03e-14) rot=(1,0,0;1.5708rad)
  Support = -> [Pad002]
  sketch-geometry (1):
    g0: Circle CenterX=0 CenterY=0 CenterZ=0 NormalX=0 NormalY=0 NormalZ=1 AngleXU=0 Radius=8
  constraints (2):
    c: Coincident(g0,g-1)
    c: Diameter(g0) = 16
FEATURE [PartDesign::Pocket] Pocket002
  BaseFeature = -> Pad002
  ClaimChildren = false
  Fit = 0
  FitJoin = 0
  InnerFit = 0
  InnerFitJoin = 0
  InnerTaperAngle = 0
  InnerTaperAngleRev = 0
  Length = 5
  Length2 = 100
  Linearize = true
  NewSolid = false
  Placement = pos=(0,0,0) rot=(1,0,0;1.5708rad)
  Profile = -> Sketch005
  Refine = true
  Suppress = false
  Type = 1
FEATURE [Sketcher::SketchObject] Sketch006
  FullyConstrained = true
  MapMode = 5
  Placement = pos=(0,-26,2.03e-14) rot=(1,0,0;1.5708rad)
  Support = -> [Pocket002]
  sketch-geometry (1):
    g0: Circle CenterX=0 CenterY=0 CenterZ=0 NormalX=0 NormalY=0 NormalZ=1 AngleXU=0 Radius=11
  constraints (2):
    c: Coincident(g0,g-1)
    c: Diameter(g0) = 22
FEATURE [PartDesign::Pocket] Pocket003
  BaseFeature = -> Pocket002
  ClaimChildren = false
  Fit = 0
  FitJoin = 0
  InnerFit = 0
  InnerFitJoin = 0
  InnerTaperAngle = 0
  InnerTaperAngleRev = 0
  Length = 1
  Length2 = 100
  Linearize = true
  NewSolid = false
  Placement = pos=(0,0,0) rot=(1,0,0;1.5708rad)
  Profile = -> Sketch006
  Refine = true
  Suppress = false
  Type = 0
FEATURE [Sketcher::SketchObject] Sketch007
  FullyConstrained = true
  MapMode = 5
  Placement = pos=(0,16,-3.5e-15) rot=(-1,0,0;1.5708rad)
  Support = -> [Pocket003]
  sketch-geometry (1):
    g0: Circle CenterX=0 CenterY=0 CenterZ=0 NormalX=0 NormalY=0 NormalZ=1 AngleXU=0 Radius=11
  constraints (2):
    c: Coincident(g0,g-1)
    c: Diameter(g0) = 22
FEATURE [PartDesign::Pocket] Pocket004
  BaseFeature = -> Pocket003
  ClaimChildren = false
  Fit = 0
  FitJoin = 0
  InnerFit = 0
  InnerFitJoin = 0
  InnerTaperAngle = 0
  InnerTaperAngleRev = 0
  Length = 1
  Length2 = 100
  Linearize = true
  NewSolid = false
  Placement = pos=(0,0,0) rot=(1,0,0;1.5708rad)
  Profile = -> Sketch007
  Refine = true
  Suppress = false
  Type = 0
FEATURE [PartDesign::Plane] DatumPlane
  AttachmentOffset = pos=(0,0,0) rot=(1,0,0;0.392699rad)
  Length = 42
  MapMode = 5
  MinimumLength = 10
  MinimumWidth = 10
  Placement = pos=(0,0,0) rot=(0.639338,0.639338,0.427192;2.33414rad)
  ResizeMode = 0
  Support = -> [YZ_Plane001]
  Width = 55.324
FEATURE [Sketcher::SketchObject] Sketch008
  ExternalGeometry = -> [Pocket004]
  FullyConstrained = true
  MapMode = 5
  Placement = pos=(0,0,0) rot=(0.485653,-0.485653,-0.726831;1.88458rad)
  Support = -> [DatumPlane]
  sketch-geometry (3):
    g0: Circle CenterX=21 CenterY=0 CenterZ=0 NormalX=0 NormalY=0 NormalZ=1 AngleXU=0 Radius=2.5
    g1: LineSegment [constr] StartX=16 StartY=13.4007 StartZ=0 EndX=21 EndY=0 EndZ=0
    g2: LineSegment [constr] StartX=21 StartY=0 StartZ=0 EndX=26 EndY=13.4007 EndZ=0
  constraints (7):
    c: PointOnObject(g0,g-1)
    c: Coincident(g1,g-3)
    c: Coincident(g1,g0)
    c: Coincident(g2,g0)
    c: Coincident(g2,g-4)
    c: Equal(g2,g1)
    c: Diameter(g0) = 5
FEATURE [PartDesign::Pocket] Pocket005
  BaseFeature = -> Pocket004
  ClaimChildren = false
  Fit = 0
  FitJoin = 0
  InnerFit = 0
  InnerFitJoin = 0
  InnerTaperAngle = 0
  InnerTaperAngleRev = 0
  Length = 5
  Length2 = 100
  Linearize = true
  NewSolid = false
  Placement = pos=(0,0,0) rot=(1,0,0;1.5708rad)
  Profile = -> Sketch008
  Refine = true
  Reversed = true
  Suppress = false
  Type = 1
FEATURE [PartDesign::Chamfer] Chamfer001
  Angle = 45
  Base = -> Pocket005 [Edge35,Edge43,Edge24,Edge25,Edge26,Edge22,Edge21,Edge20,Edge23,Edge14,Edge16,Edge17,Edge11,Edge12,Edge13]
  BaseFeature = -> Pocket005
  ChamferType = 0
  FlipDirection = false
  NewSolid = false
  Placement = pos=(0,0,0) rot=(1,0,0;1.5708rad)
  Refine = true
  Size = 0.5
  Size2 = 1
  SupportTransform = false
  Suppress = false
FEATURE [PartDesign::Body] Body001  label="SFU1605"
  AutoGroupSolids = false
  ExportMode = 0
  Group = -> [Sketch003,Pad001,Sketch004,Pad002,Sketch005,Pocket002,Sketch006,Pocket003,Sketch007,Pocket004,DatumPlane,Sketch008,Pocket005,Chamfer001]
  Origin = -> Origin001
  Placement = pos=(0,-5,0) rot=(0,0,1;0rad)
  Tip = -> Chamfer001
  _ExportChildren = -> [Pad001,Pad002,Pocket002,Pocket003,Pocket004,DatumPlane,Pocket005,Chamfer001]
  _GroupVersion = 1
FEATURE [App::Link] Link  label="Link(SFU1605)"
  AutoLinkLabel = true
  LinkPlacement = pos=(4e-16,-5,-2.7e-15) rot=(0,0,1;0rad)
  LinkedObject = -> Body001
  Placement = pos=(4e-16,-5,-2.7e-15) rot=(0,0,1;0rad)
  SyncGroupVisibility = false
  _LinkVersion = 1
FEATURE [App::Link] Link001  label="Link001(DSG16)"
  AutoLinkLabel = true
  LinkPlacement = pos=(0,-0.875,-9.7e-15) rot=(0,0,1;0rad)
  LinkedObject = -> Body
  Placement = pos=(0,-0.875,-9.7e-15) rot=(0,0,1;0rad)
  SyncGroupVisibility = false
  _LinkVersion = 1
FEATURE [PartDesign::Line] DatumLine
  AttacherType = Attacher::AttachEngineLine
  Length = 40.25
  MapMode = 19
  MinimumLength = 10
  Placement = pos=(0,-19.125,4e-15) rot=(1,0,0;1.5708rad)
  ResizeMode = 0
  Support = -> [Chamfer]
FEATURE [PartDesign::Body] Body  label="DSG16"
  AutoGroupSolids = false
  ExportMode = 0
  Group = -> [Sketch,Pad,Sketch001,Pocket,Sketch002,Pocket001,Chamfer,DatumLine]
  Origin = -> Origin
  Tip = -> Chamfer
  _ExportChildren = -> [Pad,Pocket,Pocket001,Chamfer,DatumLine]
  _GroupVersion = 1
FEATURE [Part::FeaturePython] Screw  label="M5x20-Screw"  # Fasteners workbench fastener (typed FeaturePython)
  Placement = pos=(0,-51,0) rot=(0,0,1;0rad)
  diameter = 3
  invert = false
  length = 5
  lengthCustom = 20
  matchOuter = false
  offset = 0
  thread = false
  type = 39
FEATURE [App::DocumentObjectGroup] Group  label="Components"
  ExportMode = 1
  Group = -> [Body,Body001,Screw]
  _GroupVersion = 1
FEATURE [App::LinkElement] Link002_i0
  LinkPlacement = pos=(-13.435,20,13.435) rot=(1,0,0;1.5708rad)
  LinkedObject = -> Screw
  Placement = pos=(-13.435,20,13.435) rot=(1,0,0;1.5708rad)
  _LinkVersion = 0
FEATURE [App::LinkElement] Link002_i1
  LinkPlacement = pos=(13.435,20,13.435) rot=(1,0,0;1.5708rad)
  LinkedObject = -> Screw
  Placement = pos=(13.435,20,13.435) rot=(1,0,0;1.5708rad)
  _LinkVersion = 0
FEATURE [App::LinkElement] Link002_i2
  LinkPlacement = pos=(19,20,6.78e-14) rot=(1,0,0;1.5708rad)
  LinkedObject = -> Screw
  Placement = pos=(19,20,6.78e-14) rot=(1,0,0;1.5708rad)
  _LinkVersion = 0
FEATURE [App::LinkElement] Link002_i3
  LinkPlacement = pos=(13.435,20,-13.435) rot=(1,0,0;1.5708rad)
  LinkedObject = -> Screw
  Placement = pos=(13.435,20,-13.435) rot=(1,0,0;1.5708rad)
  _LinkVersion = 0
FEATURE [App::LinkElement] Link002_i4
  LinkPlacement = pos=(-19,20,6.78e-14) rot=(1,0,0;1.5708rad)
  LinkedObject = -> Screw
  Placement = pos=(-19,20,6.78e-14) rot=(1,0,0;1.5708rad)
  _LinkVersion = 0
FEATURE [App::LinkElement] Link002_i5
  LinkPlacement = pos=(-13.435,20,-13.435) rot=(1,0,0;1.5708rad)
  LinkedObject = -> Screw
  Placement = pos=(-13.435,20,-13.435) rot=(1,0,0;1.5708rad)
  _LinkVersion = 0
FEATURE [App::Link] Link002  label="M5x20-Screw 6ct"
  AutoLinkLabel = true
  ElementCount = 6
  ElementList = -> [Link002_i0,Link002_i1,Link002_i2,Link002_i3,Link002_i4,Link002_i5]
  LinkPlacement = pos=(0,-51,0) rot=(0,0,1;0rad)
  LinkedObject = -> Screw
  Placement = pos=(0,-51,0) rot=(0,0,1;0rad)
  SyncGroupVisibility = false
  _LinkVersion = 1
FEATURE [Part::FeaturePython] Parts  # WARN: FeaturePython — macro-defined, semantics opaque (R4)
  Group = -> [Link,Link001,Link002]
  GroupMode = 0
  _LinkVersion = 1
FEATURE [Part::FeaturePython] Assembly  label="NUT Assembly"  # WARN: FeaturePython — macro-defined, semantics opaque (R4)
  AutoRelax = true
  BuildShape = 0
  Freeze = false
  Group = -> [Constraints,Elements,Parts]
  Verbose = false
  _LinkVersion = 1
  _SolverType = 1
  _Version = 1
FEATURE [App::FeaturePython] Constraints  # WARN: FeaturePython — macro-defined, semantics opaque (R4)
  Group = -> [Constraint006,Constraint007,Constraint,Constraint008,Constraint009,Constraint010,Constraint011,Constraint012]
  _LinkVersion = 1
  _Version = 1
FEATURE [App::FeaturePython] Elements  # WARN: FeaturePython — macro-defined, semantics opaque (R4)
  Group = -> [_Element012,_Element013,_Element014,Element,Element001,Element002,Element003,_Element,_Element015,_Element016,_Element017,_Element018,_Element019,_Element020,_Element021,_Element022,_Element023,_Element024,_Element025]
  _LinkVersion = 1
FEATURE [App::FeaturePython] Constraint006  label="Attachment006"  # WARN: FeaturePython — macro-defined, semantics opaque (R4)
  Cascade = false
  Disabled = false
  Group = -> [ElementLink012,ElementLink013]
  Multiply = false
  _ConstraintType = 45
  _LinkVersion = 1
  _Parent = -> Constraints
FEATURE [App::FeaturePython] ElementLink012  label="_Element012"  # link proxy (typed FeaturePython)
  LinkTransform = true
  LinkedObject = -> _Element012
  _LinkVersion = 1
  _Parent = -> Constraint006
FEATURE [Part::FeaturePython] _Element012  # link proxy (typed FeaturePython)
  Detach = false
  LinkTransform = true
  LinkedObject = -> Link001 [Chamfer.Edge58]
  _LinkVersion = 1
  _Parent = -> Elements
FEATURE [App::FeaturePython] ElementLink013  label="Nut-mate"  # link proxy (typed FeaturePython)
  LinkTransform = true
  LinkedObject = -> _Element013
  _LinkVersion = 1
  _Parent = -> Constraint006
FEATURE [Part::FeaturePython] _Element013  label="Nut-mate"  # link proxy (typed FeaturePython)
  Detach = false
  LinkTransform = true
  LinkedObject = -> Link [Chamfer001.Edge6]
  _LinkVersion = 1
  _Parent = -> Elements
FEATURE [App::FeaturePython] Constraint007  label="Locked"  # WARN: FeaturePython — macro-defined, semantics opaque (R4)
  Disabled = false
  Group = -> [ElementLink014]
  _ConstraintType = 0
  _LinkVersion = 1
  _Parent = -> Constraints
FEATURE [App::FeaturePython] ElementLink014  label="_Element014"  # link proxy (typed FeaturePython)
  LinkTransform = true
  LinkedObject = -> _Element014
  _LinkVersion = 1
  _Parent = -> Constraint007
FEATURE [Part::FeaturePython] _Element014  # link proxy (typed FeaturePython)
  Detach = false
  LinkTransform = true
  LinkedObject = -> Link001 [Chamfer.Face1]
  _LinkVersion = 1
  _Parent = -> Elements
FEATURE [Part::FeaturePython] Element  label="gov-mate"  # link proxy (typed FeaturePython)
  Detach = false
  LinkTransform = true
  LinkedObject = -> Link001 [Chamfer.Edge7]
  _LinkVersion = 1
  _Parent = -> Elements
FEATURE [Part::FeaturePython] Element001  label="Axis"  # link proxy (typed FeaturePython)
  Detach = false
  LinkTransform = true
  LinkedObject = -> Link001 [DatumLine.]
  _LinkVersion = 1
  _Parent = -> Elements
FEATURE [Part::FeaturePython] Element002  label="gov-mate-r"  # link proxy (typed FeaturePython)
  Detach = false
  LinkTransform = true
  LinkedObject = -> Link001 [Chamfer.Edge5]
  _LinkVersion = 1
  _Parent = -> Elements
FEATURE [Part::FeaturePython] Element003  label="shim-mate"  # link proxy (typed FeaturePython)
  Detach = false
  LinkTransform = true
  LinkedObject = -> Link001 [Chamfer.Edge8]
  _LinkVersion = 1
  _Parent = -> Elements
FEATURE [App::FeaturePython] Constraint  label="Attachment"  # WARN: FeaturePython — macro-defined, semantics opaque (R4)
  Cascade = false
  Disabled = false
  Group = -> [ElementLink,ElementLink015]
  Multiply = false
  _ConstraintType = 45
  _LinkVersion = 0
  _Parent = -> Constraints
FEATURE [App::FeaturePython] ElementLink  label="_Element"  # link proxy (typed FeaturePython)
  LinkTransform = true
  LinkedObject = -> _Element
  _LinkVersion = 0
  _Parent = -> Constraint
FEATURE [Part::FeaturePython] _Element  # link proxy (typed FeaturePython)
  Detach = false
  LinkTransform = true
  LinkedObject = -> Link002 [0.Edge4]
  _LinkVersion = 0
  _Parent = -> Elements
FEATURE [App::FeaturePython] ElementLink015  label="_Element015"  # link proxy (typed FeaturePython)
  LinkTransform = true
  LinkedObject = -> _Element015
  _LinkVersion = 0
  _Parent = -> Constraint
FEATURE [Part::FeaturePython] _Element015  # link proxy (typed FeaturePython)
  Detach = false
  LinkTransform = true
  LinkedObject = -> Link [Chamfer001.Edge40]
  _LinkVersion = 0
  _Parent = -> Elements
FEATURE [App::FeaturePython] Constraint008  label="Attachment007"  # WARN: FeaturePython — macro-defined, semantics opaque (R4)
  Cascade = false
  Disabled = false
  Group = -> [ElementLink016,ElementLink017]
  Multiply = false
  _ConstraintType = 45
  _LinkVersion = 0
  _Parent = -> Constraints
FEATURE [App::FeaturePython] ElementLink016  label="_Element016"  # link proxy (typed FeaturePython)
  LinkTransform = true
  LinkedObject = -> _Element016
  _LinkVersion = 0
  _Parent = -> Constraint008
FEATURE [Part::FeaturePython] _Element016  # link proxy (typed FeaturePython)
  Detach = false
  LinkTransform = true
  LinkedObject = -> Link002 [1.Edge4]
  _LinkVersion = 0
  _Parent = -> Elements
FEATURE [App::FeaturePython] ElementLink017  label="_Element017"  # link proxy (typed FeaturePython)
  LinkTransform = true
  LinkedObject = -> _Element017
  _LinkVersion = 0
  _Parent = -> Constraint008
FEATURE [Part::FeaturePython] _Element017  # link proxy (typed FeaturePython)
  Detach = false
  LinkTransform = true
  LinkedObject = -> Link [Chamfer001.Edge39]
  _LinkVersion = 0
  _Parent = -> Elements
FEATURE [App::FeaturePython] Constraint009  label="Attachment008"  # WARN: FeaturePython — macro-defined, semantics opaque (R4)
  Cascade = false
  Disabled = false
  Group = -> [ElementLink018,ElementLink019]
  Multiply = false
  _ConstraintType = 45
  _LinkVersion = 0
  _Parent = -> Constraints
FEATURE [App::FeaturePython] ElementLink018  label="_Element018"  # link proxy (typed FeaturePython)
  LinkTransform = true
  LinkedObject = -> _Element018
  _LinkVersion = 0
  _Parent = -> Constraint009
FEATURE [Part::FeaturePython] _Element018  # link proxy (typed FeaturePython)
  Detach = false
  LinkTransform = true
  LinkedObject = -> Link002 [2.Edge4]
  _LinkVersion = 0
  _Parent = -> Elements
FEATURE [App::FeaturePython] ElementLink019  label="_Element019"  # link proxy (typed FeaturePython)
  LinkTransform = true
  LinkedObject = -> _Element019
  _LinkVersion = 0
  _Parent = -> Constraint009
FEATURE [Part::FeaturePython] _Element019  # link proxy (typed FeaturePython)
  Detach = false
  LinkTransform = true
  LinkedObject = -> Link [Chamfer001.Edge38]
  _LinkVersion = 0
  _Parent = -> Elements
FEATURE [App::FeaturePython] Constraint010  label="Attachment009"  # WARN: FeaturePython — macro-defined, semantics opaque (R4)
  Cascade = false
  Disabled = false
  Group = -> [ElementLink020,ElementLink021]
  Multiply = false
  _ConstraintType = 45
  _LinkVersion = 0
  _Parent = -> Constraints
FEATURE [App::FeaturePython] ElementLink020  label="_Element020"  # link proxy (typed FeaturePython)
  LinkTransform = true
  LinkedObject = -> _Element020
  _LinkVersion = 0
  _Parent = -> Constraint010
FEATURE [Part::FeaturePython] _Element020  # link proxy (typed FeaturePython)
  Detach = false
  LinkTransform = true
  LinkedObject = -> Link002 [3.Edge4]
  _LinkVersion = 0
  _Parent = -> Elements
FEATURE [App::FeaturePython] ElementLink021  label="_Element021"  # link proxy (typed FeaturePython)
  LinkTransform = true
  LinkedObject = -> _Element021
  _LinkVersion = 0
  _Parent = -> Constraint010
FEATURE [Part::FeaturePython] _Element021  # link proxy (typed FeaturePython)
  Detach = false
  LinkTransform = true
  LinkedObject = -> Link [Chamfer001.Edge43]
  _LinkVersion = 0
  _Parent = -> Elements
FEATURE [App::FeaturePython] Constraint011  label="Attachment010"  # WARN: FeaturePython — macro-defined, semantics opaque (R4)
  Cascade = false
  Disabled = false
  Group = -> [ElementLink022,ElementLink023]
  Multiply = false
  _ConstraintType = 45
  _LinkVersion = 0
  _Parent = -> Constraints
FEATURE [App::FeaturePython] ElementLink022  label="_Element022"  # link proxy (typed FeaturePython)
  LinkTransform = true
  LinkedObject = -> _Element022
  _LinkVersion = 0
  _Parent = -> Constraint011
FEATURE [Part::FeaturePython] _Element022  # link proxy (typed FeaturePython)
  Detach = false
  LinkTransform = true
  LinkedObject = -> Link002 [4.Edge4]
  _LinkVersion = 0
  _Parent = -> Elements
FEATURE [App::FeaturePython] ElementLink023  label="_Element023"  # link proxy (typed FeaturePython)
  LinkTransform = true
  LinkedObject = -> _Element023
  _LinkVersion = 0
  _Parent = -> Constraint011
FEATURE [Part::FeaturePython] _Element023  # link proxy (typed FeaturePython)
  Detach = false
  LinkTransform = true
  LinkedObject = -> Link [Chamfer001.Edge41]
  _LinkVersion = 0
  _Parent = -> Elements
FEATURE [App::FeaturePython] Constraint012  label="Attachment011"  # WARN: FeaturePython — macro-defined, semantics opaque (R4)
  Cascade = false
  Disabled = false
  Group = -> [ElementLink024,ElementLink025]
  Multiply = false
  _ConstraintType = 45
  _LinkVersion = 0
  _Parent = -> Constraints
FEATURE [App::FeaturePython] ElementLink024  label="_Element024"  # link proxy (typed FeaturePython)
  LinkTransform = true
  LinkedObject = -> _Element024
  _LinkVersion = 0
  _Parent = -> Constraint012
FEATURE [Part::FeaturePython] _Element024  # link proxy (typed FeaturePython)
  Detach = false
  LinkTransform = true
  LinkedObject = -> Link002 [5.Edge4]
  _LinkVersion = 0
  _Parent = -> Elements
FEATURE [App::FeaturePython] ElementLink025  label="_Element025"  # link proxy (typed FeaturePython)
  LinkTransform = true
  LinkedObject = -> _Element025
  _LinkVersion = 0
  _Parent = -> Constraint012
FEATURE [Part::FeaturePython] _Element025  # link proxy (typed FeaturePython)
  Detach = false
  LinkTransform = true
  LinkedObject = -> Link [Chamfer001.Edge42]
  _LinkVersion = 0
  _Parent = -> Elements
---- part parts/Ballscrew.FCStd = doc fcstd_904fc7d7aa5a (101767 chars; too large to inline — full recipe in that document) ----
---- part parts/HGH20CA.FCStd = doc fcstd_d22bc38b7fa2 ----
FCSTD DOCUMENT  (FreeCAD 2021.614R24301 +3747 (Git))
Label: HGH20CA
License: Creative Commons Attribution
LicenseURL: http://creativecommons.org/licenses/by/4.0/
objects: Part::FeaturePython×21, App::FeaturePython×20, Sketcher::SketchObject×11, PartDesign::Pad×6, PartDesign::Pocket×4, App::Link×4, PartDesign::Plane×2, PartDesign::Body×2, App::DocumentObjectGroup×2, PartDesign::Mirrored×1, PartDesign::Fillet×1, PartDesign::Line×1, PartDesign::Revolution×1
note: 74 computed .brp shape members not serialized (recipe doc carries the construction recipe); baked Part::Feature solids carry a one-line shape summary decoded from their .brp

FEATURE [Sketcher::SketchObject] Sketch
  FullyConstrained = true
  MapMode = 5
  Placement = pos=(0,0,0) rot=(1,0,0;1.5708rad)
  Support = -> [XZ_Plane]
  sketch-geometry (20):
    g0: LineSegment StartX=-21 StartY=30 StartZ=0 EndX=-11.5 EndY=30 EndZ=0
    g1: LineSegment StartX=22 StartY=29 StartZ=0 EndX=22 EndY=6.1 EndZ=0
    g2: LineSegment StartX=20.5 StartY=4.6 StartZ=0 EndX=-20.5 EndY=4.6 EndZ=0
    g3: LineSegment StartX=-21.6 StartY=5.7 StartZ=0 EndX=-21.6 EndY=22 EndZ=0
    g4: GeomPoint [constr] X=0 Y=4.6 Z=0
    g5: LineSegment StartX=-20.5 StartY=4.6 StartZ=0 EndX=-21.6 EndY=5.7 EndZ=0
    g6: LineSegment StartX=20.5 StartY=4.6 StartZ=0 EndX=22 EndY=6.1 EndZ=0
    g7: LineSegment StartX=-22 StartY=29 StartZ=0 EndX=-21 EndY=30 EndZ=0
    g8: LineSegment StartX=21 StartY=30 StartZ=0 EndX=22 EndY=29 EndZ=0
    g9: LineSegment StartX=-11.5 StartY=30 StartZ=0 EndX=-11.5 EndY=29.6 EndZ=0
    g10: LineSegment StartX=-11.5 StartY=29.6 StartZ=0 EndX=-4.25 EndY=29.6 EndZ=0
    g11: LineSegment StartX=-4.25 StartY=29.6 StartZ=0 EndX=-4.25 EndY=30 EndZ=0
    g12: LineSegment StartX=4.25 StartY=30 StartZ=0 EndX=4.25 EndY=29.6 EndZ=0
    g13: LineSegment StartX=4.25 StartY=29.6 StartZ=0 EndX=11.5 EndY=29.6 EndZ=0
    g14: LineSegment StartX=11.5 StartY=29.6 StartZ=0 EndX=11.5 EndY=30 EndZ=0
    g15: LineSegment StartX=11.5 StartY=30 StartZ=0 EndX=21 EndY=30 EndZ=0
    g16: LineSegment StartX=-4.25 StartY=30 StartZ=0 EndX=4.25 EndY=30 EndZ=0
    g17: GeomPoint [constr] X=0 Y=30 Z=0
    g18: LineSegment StartX=-21.6 StartY=22 StartZ=0 EndX=-22 EndY=22 EndZ=0
    g19: LineSegment StartX=-22 StartY=22 StartZ=0 EndX=-22 EndY=29 EndZ=0
  constraints (54):
    c: Horizontal(g0)
    c: Horizontal(g2)
    c: Vertical(g1)
    c: Vertical(g3)
    c: PointOnObject(g4,g-2)
    c: Vertical(g9)
    c: Coincident(g10,g9)
    c: Horizontal(g10)
    c: Coincident(g11,g10)
    c: Vertical(g11)
    c: Vertical(g12)
    c: Coincident(g13,g12)
    c: Horizontal(g13)
    c: Coincident(g14,g13)
    c: Vertical(g14)
    c: Coincident(g0,g7)
    c: Coincident(g15,g8)
    c: Coincident(g1,g8)
    c: Coincident(g16,g12)
    c: Coincident(g15,g14)
    c: Tangent(g0,g15)
    c: Coincident(g0,g9)
    c: Coincident(g16,g11)
    c: Tangent(g0,g16)
    c: Coincident(g1,g6)
    c: Coincident(g2,g6)
    c: Coincident(g2,g5)
    c: Coincident(g3,g5)
    c: Symmetric(g2,g2,g4)
    c: PointOnObject(g17,g-2)
    c: Symmetric(g12,g11,g17)
    c: Equal(g13,g10)
    c: Symmetric(g8,g0,g17)
    c: Horizontal(g12,g10)
    c: DistanceX(g16,g16) = 8.5
    c: DistanceX(g2,g2) = 41
    c: DistanceY(g14,g14) = 0.4
    c: DistanceX(g14,g1) = 10.5
    c: DistanceY(g1,g8) = 1
    c: DistanceY(g-1,g2) = 4.6
    c: DistanceY(g-1,g8) = 30
    c: DistanceY(g2,g1) = 1.5
    c: Horizontal(g18)
    c: Coincident(g19,g18)
    c: Vertical(g19)
    c: DistanceX(g8,g1) = 1
    c: Coincident(g3,g18)
    c: Coincident(g7,g19)
    c: Horizontal(g1,g7)
    c: DistanceX(g7,g1) = 44
    c: DistanceX(g7,g0) = 10.5
    c: DistanceY(g18,g0) = 8
    c: DistanceX(g18,g3) = 0.4
    c: Angle(g2,g5) = 2.35619
FEATURE [PartDesign::Pad] Pad
  ClaimChildren = false
  Direction = (1,1,1)
  Fit = 0
  FitJoin = 0
  InnerFit = 0
  InnerFitJoin = 0
  InnerTaperAngle = 0
  InnerTaperAngleRev = 0
  Length = 50.5
  Length2 = 100
  Linearize = true
  Midplane = true
  NewSolid = false
  Placement = pos=(0,0,0) rot=(1,0,0;1.5708rad)
  Profile = -> Sketch
  Refine = true
  Suppress = false
  Type = 0
FEATURE [Sketcher::SketchObject] Sketch001
  ExternalGeometry = -> [Pad]
  FullyConstrained = true
  MapMode = 5
  Placement = pos=(0,1.32e-14,30) rot=(0,0,1;3.14159rad)
  Support = -> [Pad]
  sketch-geometry (4):
    g0: Circle CenterX=-16 CenterY=18 CenterZ=0 NormalX=0 NormalY=0 NormalZ=1 AngleXU=0 Radius=2.5
    g1: Circle CenterX=-16 CenterY=-18 CenterZ=0 NormalX=0 NormalY=0 NormalZ=1 AngleXU=0 Radius=2.5
    g2: Circle CenterX=16 CenterY=18 CenterZ=0 NormalX=0 NormalY=0 NormalZ=1 AngleXU=0 Radius=2.5
    g3: Circle CenterX=16 CenterY=-18 CenterZ=0 NormalX=0 NormalY=0 NormalZ=1 AngleXU=0 Radius=2.5
  constraints (12):
    c: Horizontal(g3,g1)
    c: Vertical(g1,g0)
    c: Vertical(g2,g3)
    c: Horizontal(g0,g2)
    c: DistanceX(g0,g2) = 32
    c: DistanceY(g3,g2) = 36
    c: Equal(g0,g2)
    c: Equal(g2,g3)
    c: Equal(g3,g1)
    c: Symmetric(g0,g3,g-1)
    c: DistanceX(g2,g-3) = 5.6
    c: Diameter(g2) = 5
FEATURE [Sketcher::SketchObject] Sketch002
  ExternalGeometry = -> [Pad]
  FullyConstrained = true
  MapMode = 5
  Placement = pos=(0,0,0) rot=(1,0,0;1.5708rad)
  Support = -> [XZ_Plane]
  sketch-geometry (8):
    g0: LineSegment StartX=-20.6 StartY=29.1 StartZ=0 EndX=20.4 EndY=29.1 EndZ=0
    g1: LineSegment StartX=21.4 StartY=28.1 StartZ=0 EndX=21.4 EndY=5.5 EndZ=0
    g2: LineSegment StartX=20.5 StartY=4.6 StartZ=0 EndX=-20.5 EndY=4.6 EndZ=0
    g3: LineSegment StartX=-21.6 StartY=5.7 StartZ=0 EndX=-21.6 EndY=28.1 EndZ=0
    g4: LineSegment StartX=-21.6 StartY=5.7 StartZ=0 EndX=-20.5 EndY=4.6 EndZ=0
    g5: LineSegment StartX=-21.6 StartY=28.1 StartZ=0 EndX=-20.6 EndY=29.1 EndZ=0
    g6: LineSegment StartX=20.4 StartY=29.1 StartZ=0 EndX=21.4 EndY=28.1 EndZ=0
    g7: LineSegment StartX=20.5 StartY=4.6 StartZ=0 EndX=21.4 EndY=5.5 EndZ=0
  constraints (22):
    c: Horizontal(g0)
    c: Horizontal(g2)
    c: Vertical(g1)
    c: Vertical(g3)
    c: Coincident(g3,g4)
    c: Coincident(g2,g4)
    c: Coincident(g2,g-7)
    c: Coincident(g3,g-7)
    c: Coincident(g0,g5)
    c: Coincident(g3,g5)
    c: Coincident(g0,g6)
    c: Coincident(g1,g6)
    c: Horizontal(g1,g3)
    c: DistanceX(g3,g0) = 1
    c: DistanceY(g3,g0) = 1
    c: DistanceX(g0,g1) = 1
    c: DistanceY(g2,g0) = 24.5
    c: DistanceX(g3,g1) = 43
    c: Coincident(g7,g-5)
    c: PointOnObject(g7,g-5)
    c: Coincident(g1,g7)
    c: PointOnObject(g2,g7)
FEATURE [PartDesign::Pad] Pad001
  BaseFeature = -> Pad
  ClaimChildren = false
  Direction = (1,1,1)
  Fit = 0
  FitJoin = 0
  InnerFit = 0
  InnerFitJoin = 0
  InnerTaperAngle = 0
  InnerTaperAngleRev = 0
  Length = 75.8
  Length2 = 100
  Linearize = true
  Midplane = true
  NewSolid = false
  Placement = pos=(0,0,0) rot=(1,0,0;1.5708rad)
  Profile = -> Sketch002
  Refine = true
  Suppress = false
  Type = 0
FEATURE [Sketcher::SketchObject] Sketch003
  ExternalGeometry = -> [Pad001]
  FullyConstrained = true
  MapMode = 5
  Placement = pos=(0,-37.9,8.3e-15) rot=(1,0,0;1.5708rad)
  Support = -> [Pad001]
  sketch-geometry (14):
    g0: ArcOfCircle CenterX=0 CenterY=24.1 CenterZ=0 NormalX=0 NormalY=0 NormalZ=1 AngleXU=0 Radius=5.25 StartAngle=3.14159 EndAngle=6.28319
    g1: ArcOfCircle CenterX=-19.35 CenterY=15.6 CenterZ=0 NormalX=0 NormalY=0 NormalZ=1 AngleXU=0 Radius=2.75 StartAngle=4.71239 EndAngle=7.85398
    g2: ArcOfCircle CenterX=19.35 CenterY=15.6 CenterZ=0 NormalX=0 NormalY=0 NormalZ=1 AngleXU=0 Radius=2.75 StartAngle=1.5708 EndAngle=4.71239
    g3: LineSegment StartX=-5.25 StartY=24.1 StartZ=0 EndX=-5.25 EndY=29.1 EndZ=0
    g4: LineSegment StartX=5.25 StartY=24.1 StartZ=0 EndX=5.25 EndY=29.1 EndZ=0
    g5: LineSegment StartX=-5.25 StartY=29.1 StartZ=0 EndX=5.25 EndY=29.1 EndZ=0
    g6: LineSegment StartX=-19.35 StartY=18.35 StartZ=0 EndX=-21.6 EndY=18.35 EndZ=0
    g7: LineSegment StartX=-19.35 StartY=12.85 StartZ=0 EndX=-21.6 EndY=12.85 EndZ=0
    g8: LineSegment [constr] StartX=-19.35 StartY=15.6 StartZ=0 EndX=0 EndY=15.6 EndZ=0
    g9: LineSegment [constr] StartX=0 StartY=15.6 StartZ=0 EndX=19.35 EndY=15.6 EndZ=0
    g10: LineSegment StartX=19.35 StartY=18.35 StartZ=0 EndX=21.4 EndY=18.35 EndZ=0
    g11: LineSegment StartX=19.35 StartY=12.85 StartZ=0 EndX=21.4 EndY=12.85 EndZ=0
    g12: LineSegment StartX=-21.6 StartY=18.35 StartZ=0 EndX=-21.6 EndY=12.85 EndZ=0
    g13: LineSegment StartX=21.4 StartY=18.35 StartZ=0 EndX=21.4 EndY=12.85 EndZ=0
  constraints (38):
    c: PointOnObject(g0,g-2)
    c: Horizontal(g1,g2)
    c: Equal(g1,g2)
    c: Diameter(g0) = 10.5
    c: DistanceY(g0,g-3) = 5
    c: PointOnObject(g3,g-3)
    c: Vertical(g3)
    c: PointOnObject(g4,g-3)
    c: Vertical(g4)
    c: Tangent(g0,g3) = 1.5708
    c: Tangent(g0,g4) = -1.5708
    c: Coincident(g5,g3)
    c: Coincident(g5,g4)
    c: PointOnObject(g6,g-4)
    c: Horizontal(g6)
    c: PointOnObject(g7,g-4)
    c: Horizontal(g7)
    c: Diameter(g1) = 5.5
    c: Coincident(g8,g1)
    c: Horizontal(g8)
    c: Coincident(g9,g8)
    c: Coincident(g9,g2)
    c: Equal(g9,g8)
    c: PointOnObject(g10,g-5)
    c: Horizontal(g10)
    c: PointOnObject(g11,g-5)
    c: Horizontal(g11)
    c: DistanceY(g2,g-3) = 13.5
    c: DistanceX(g-4,g1) = 2.25
    c: PointOnObject(g8,g-2)
    c: Tangent(g1,g7) = 1.5708
    c: Tangent(g1,g6) = -1.5708
    c: Tangent(g2,g10) = 1.5708
    c: Tangent(g2,g11) = -1.5708
    c: Coincident(g12,g6)
    c: Coincident(g12,g7)
    c: Coincident(g13,g10)
    c: Coincident(g13,g11)
FEATURE [PartDesign::Pocket] Pocket
  BaseFeature = -> Pad001
  ClaimChildren = false
  Fit = 0
  FitJoin = 0
  InnerFit = 0
  InnerFitJoin = 0
  InnerTaperAngle = 0
  InnerTaperAngleRev = 0
  Length = 1.5
  Length2 = 100
  Linearize = true
  NewSolid = false
  Placement = pos=(0,0,0) rot=(1,0,0;1.5708rad)
  Profile = -> Sketch003
  Refine = true
  Suppress = false
  Type = 0
FEATURE [Sketcher::SketchObject] Sketch004
  ExternalGeometry = -> [Pocket]
  FullyConstrained = true
  MapMode = 5
  Placement = pos=(0,-36.4,2.95e-14) rot=(1,0,0;1.5708rad)
  Support = -> [Pocket]
  sketch-geometry (3):
    g0: Circle CenterX=-19.35 CenterY=15.6 CenterZ=0 NormalX=0 NormalY=0 NormalZ=1 AngleXU=0 Radius=1.25
    g1: Circle CenterX=19.35 CenterY=15.6 CenterZ=0 NormalX=0 NormalY=0 NormalZ=1 AngleXU=0 Radius=1.25
    g2: Circle CenterX=0 CenterY=24.1 CenterZ=0 NormalX=0 NormalY=0 NormalZ=1 AngleXU=0 Radius=2.5
  constraints (6):
    c: Coincident(g0,g-3)
    c: Coincident(g1,g-5)
    c: Coincident(g2,g-4)
    c: Diameter(g2) = 5
    c: Diameter(g1) = 2.5
    c: Equal(g1,g0)
FEATURE [PartDesign::Pocket] Pocket001
  BaseFeature = -> Pocket
  ClaimChildren = false
  Fit = 0
  FitJoin = 0
  InnerFit = 0
  InnerFitJoin = 0
  InnerTaperAngle = 0
  InnerTaperAngleRev = 0
  Length = 8
  Length2 = 100
  Linearize = true
  NewSolid = false
  Placement = pos=(0,0,0) rot=(1,0,0;1.5708rad)
  Profile = -> Sketch004
  Refine = true
  Suppress = false
  Type = 0
FEATURE [PartDesign::Mirrored] Mirrored
  BaseFeature = -> Pocket001
  CopyShape = false
  MirrorPlane = -> XZ_Plane
  NewSolid = false
  OriginalSubs = -> [Pocket001,Pocket]
  Originals = -> [Pocket001,Pocket]
  ParallelTransform = true
  Placement = pos=(0,0,0) rot=(1,0,0;1.5708rad)
  Refine = true
  SubTransform = true
  Suppress = false
  _Version = 1
FEATURE [Sketcher::SketchObject] Sketch005
  FullyConstrained = true
  MapMode = 5
  Placement = pos=(0,0,0) rot=(1,0,0;1.5708rad)
  Support = -> [XZ_Plane001]
  sketch-geometry (1):
    g0: Circle CenterX=0 CenterY=0 CenterZ=0 NormalX=0 NormalY=0 NormalZ=1 AngleXU=0 Radius=3
  constraints (2):
    c: Coincident(g0,g-1)
    c: Radius(g0) = 3
FEATURE [PartDesign::Pad] Pad002
  ClaimChildren = false
  Direction = (1,1,1)
  Fit = 0
  FitJoin = 0
  InnerFit = 0
  InnerFitJoin = 0
  InnerTaperAngle = 0
  InnerTaperAngleRev = 0
  Length = 7
  Length2 = 100
  Linearize = true
  NewSolid = false
  Placement = pos=(0,0,0) rot=(1,0,0;1.5708rad)
  Profile = -> Sketch005
  Refine = true
  Suppress = false
  Type = 0
FEATURE [Sketcher::SketchObject] Sketch006
  FullyConstrained = true
  MapMode = 5
  Placement = pos=(0,0,0) rot=(-1,0,0;1.5708rad)
  Support = -> [Pad002]
  sketch-geometry (7):
    g0: LineSegment StartX=4 StartY=-2.3094 StartZ=0 EndX=4 EndY=2.3094 EndZ=0
    g1: LineSegment StartX=4 StartY=2.3094 StartZ=0 EndX=-4e-16 EndY=4.6188 EndZ=0
    g2: LineSegment StartX=-4e-16 StartY=4.6188 StartZ=0 EndX=-4 EndY=2.3094 EndZ=0
    g3: LineSegment StartX=-4 StartY=2.3094 StartZ=0 EndX=-4 EndY=-2.3094 EndZ=0
    g4: LineSegment StartX=-4 StartY=-2.3094 StartZ=0 EndX=4e-16 EndY=-4.6188 EndZ=0
    g5: LineSegment StartX=4e-16 StartY=-4.6188 StartZ=0 EndX=4 EndY=-2.3094 EndZ=0
    g6: Circle [constr] CenterX=0 CenterY=0 CenterZ=0 NormalX=0 NormalY=0 NormalZ=1 AngleXU=0 Radius=4.6188
  constraints (16):
    c: Coincident(g0,g1)
    c: Coincident(g1,g2)
    c: Coincident(g2,g3)
    c: Coincident(g3,g4)
    c: Coincident(g4,g5)
    c: Coincident(g5,g0)
    c: Equal(g0, g1-g5) x5
    c: PointOnObject(g0,g6)
    c: PointOnObject(g1,g6)
    c: PointOnObject(g2,g6)
    c: PointOnObject(g3,g6)
    c: PointOnObject(g4,g6)
    c: PointOnObject(g5,g6)
    c: Coincident(g6,g-1)
    c: Vertical(g0)
    c: DistanceX(g2,g0) = 8
FEATURE [PartDesign::Pad] Pad003
  BaseFeature = -> Pad002
  ClaimChildren = false
  Direction = (1,1,1)
  Fit = 0
  FitJoin = 0
  InnerFit = 0
  InnerFitJoin = 0
  InnerTaperAngle = 0
  InnerTaperAngleRev = 0
  Length = 3.5
  Length2 = 100
  Linearize = true
  NewSolid = false
  Placement = pos=(0,0,0) rot=(1,0,0;1.5708rad)
  Profile = -> Sketch006
  Refine = true
  Suppress = false
  Type = 0
FEATURE [Sketcher::SketchObject] Sketch007
  FullyConstrained = true
  MapMode = 5
  Placement = pos=(0,3.5,8e-16) rot=(-1,0,0;1.5708rad)
  Support = -> [Pad003]
  sketch-geometry (1):
    g0: Circle CenterX=0 CenterY=0 CenterZ=0 NormalX=0 NormalY=0 NormalZ=1 AngleXU=0 Radius=4
  constraints (2):
    c: Coincident(g0,g-1)
    c: Radius(g0) = 4
FEATURE [PartDesign::Pad] Pad004
  BaseFeature = -> Pad003
  ClaimChildren = false
  Direction = (1,1,1)
  Fit = 0
  FitJoin = 0
  InnerFit = 0
  InnerFitJoin = 0
  InnerTaperAngle = 0
  InnerTaperAngleRev = 0
  Length = 8
  Length2 = 100
  Linearize = true
  NewSolid = false
  Placement = pos=(0,0,0) rot=(1,0,0;1.5708rad)
  Profile = -> Sketch007
  Refine = true
  Suppress = false
  Type = 0
FEATURE [PartDesign::Fillet] Fillet
  Base = -> Pad004 [Edge35]
  BaseFeature = -> Pad004
  NewSolid = false
  Placement = pos=(0,0,0) rot=(1,0,0;1.5708rad)
  Radius = 3
  Refine = true
  SupportTransform = false
  Suppress = false
FEATURE [PartDesign::Plane] DatumPlane
  AttachmentOffset = pos=(0,0,0) rot=(1,0,0;0.785398rad)
  Length = 50
  MapMode = 5
  MinimumLength = 10
  MinimumWidth = 10
  Placement = pos=(0,11.5,3e-15) rot=(-1,0,0;0.785398rad)
  ResizeMode = 0
  Support = -> [Fillet]
  Width = 70.7107
FEATURE [Sketcher::SketchObject] Sketch008
  FullyConstrained = true
  MapMode = 5
  Placement = pos=(0,11.5,3.6e-15) rot=(-1,0,0;0.785398rad)
  Support = -> [DatumPlane]
  sketch-geometry (7):
    g0: LineSegment StartX=3.5 StartY=-4.62073 StartZ=0 EndX=3.5 EndY=-0.579274 EndZ=0
    g1: LineSegment StartX=3.5 StartY=-0.579274 StartZ=0 EndX=8.273e-13 EndY=1.44145 EndZ=0
    g2: LineSegment StartX=8.273e-13 StartY=1.44145 StartZ=0 EndX=-3.5 EndY=-0.579274 EndZ=0
    g3: LineSegment StartX=-3.5 StartY=-0.579274 StartZ=0 EndX=-3.5 EndY=-4.62073 EndZ=0
    g4: LineSegment StartX=-3.5 StartY=-4.62073 StartZ=0 EndX=-8.273e-13 EndY=-6.64145 EndZ=0
    g5: LineSegment StartX=-8.273e-13 StartY=-6.64145 StartZ=0 EndX=3.5 EndY=-4.62073 EndZ=0
    g6: Circle [constr] CenterX=0 CenterY=-2.6 CenterZ=0 NormalX=0 NormalY=0 NormalZ=1 AngleXU=0 Radius=4.04145
  constraints (17):
    c: Coincident(g0,g1)
    c: Coincident(g1,g2)
    c: Coincident(g2,g3)
    c: Coincident(g3,g4)
    c: Coincident(g4,g5)
    c: Coincident(g5,g0)
    c: Equal(g0, g1-g5) x5
    c: PointOnObject(g0,g6)
    c: PointOnObject(g1,g6)
    c: PointOnObject(g2,g6)
    c: PointOnObject(g3,g6)
    c: PointOnObject(g4,g6)
    c: PointOnObject(g5,g6)
    c: PointOnObject(g6,g-2)
    c: Vertical(g0)
    c: DistanceX(g2,g0) = 7
    c: DistanceY(g6,g-1) = 2.6
FEATURE [PartDesign::Pad] Pad005
  BaseFeature = -> Fillet
  ClaimChildren = false
  Direction = (1,1,1)
  Fit = 0
  FitJoin = 0
  InnerFit = 0
  InnerFitJoin = 0
  InnerTaperAngle = 0
  InnerTaperAngleRev = 0
  Length = 2.5
  Length2 = 100
  Linearize = true
  NewSolid = false
  Placement = pos=(0,0,0) rot=(1,0,0;1.5708rad)
  Profile = -> Sketch008
  Refine = true
  Suppress = false
  Type = 0
FEATURE [PartDesign::Plane] DatumPlane001
  AttachmentOffset = pos=(0,0,0) rot=(0,1,0;1.5708rad)
  Length = 70.7107
  MapMode = 5
  MinimumLength = 10
  MinimumWidth = 10
  Placement = pos=(2e-16,7.51777,7.51777) rot=(-0.357407,0.862856,-0.357407;1.71777rad)
  ResizeMode = 0
  Support = -> [Pad005]
  Width = 70.7107
FEATURE [Sketcher::SketchObject] Sketch009
  ExternalGeometry = -> [Pad005]
  FullyConstrained = true
  MapMode = 5
  Placement = pos=(2e-16,7.51777,7.51777) rot=(-0.357407,0.862856,-0.357407;1.71777rad)
  Support = -> [DatumPlane001]
  sketch-geometry (7):
    g0: LineSegment StartX=0 StartY=8.43173 StartZ=0 EndX=-2 EndY=7.78173 EndZ=0
    g1: LineSegment StartX=-4 StartY=8.78173 StartZ=0 EndX=-5.5 EndY=7.78173 EndZ=0
    g2: LineSegment StartX=-5.5 StartY=7.78173 StartZ=0 EndX=-5.5 EndY=5.53173 EndZ=0
    g3: LineSegment StartX=-5.5 StartY=5.53173 StartZ=0 EndX=1.8e-15 EndY=5.53173 EndZ=0
    g4: LineSegment StartX=1.8e-15 StartY=5.53173 StartZ=0 EndX=0 EndY=8.43173 EndZ=0
    g5: LineSegment StartX=-4 StartY=8.78173 StartZ=0 EndX=-3.5 EndY=8.78173 EndZ=0
    g6: LineSegment StartX=-3.5 StartY=8.78173 StartZ=0 EndX=-2 EndY=7.78173 EndZ=0
  constraints (20):
    c: PointOnObject(g0,g-2)
    c: Vertical(g2)
    c: Coincident(g3,g2)
    c: Horizontal(g3)
    c: Coincident(g4,g3)
    c: Coincident(g4,g0)
    c: Symmetric(g-3,g-4,g3)
    c: DistanceY(g4,g4) = 2.9
    c: DistanceX(g3,g3) = 5.5
    c: Coincident(g2,g1)
    c: DistanceX(g1,g1) = 1.5
    c: Coincident(g5,g1)
    c: Coincident(g6,g5)
    c: Coincident(g6,g0)
    c: Horizontal(g5)
    c: DistanceX(g5,g0) = 1.5
    c: Horizontal(g1,g0)
    c: DistanceX(g1,g0) = 3.5
    c: DistanceY(g2,g2) = 2.25
    c: DistanceY(g2,g1) = 3.25
FEATURE [PartDesign::Line] DatumLine
  AttacherType = Attacher::AttachEngineLine
  Length = 70.7107
  MapMode = 29
  MinimumLength = 10
  Placement = pos=(2e-16,11.4293,3.60624) rot=(1,0,0;2.35619rad)
  ResizeMode = 0
  Support = -> [Sketch009]
FEATURE [PartDesign::Revolution] Revolution
  Angle = 360
  Axis = (0,-0.707107,-0.707107)
  Base = (2e-16,11.4293,3.60624)
  BaseFeature = -> Pad005
  ClaimChildren = false
  Fit = 0
  FitJoin = 0
  InnerFit = 0
  InnerFitJoin = 0
  NewSolid = false
  Placement = pos=(0,0,0) rot=(1,0,0;1.5708rad)
  Profile = -> Sketch009
  ReferenceAxis = -> DatumLine
  Refine = true
  Suppress = false
FEATURE [PartDesign::Body] Body001  label="Greaser"
  AutoGroupSolids = false
  ExportMode = 0
  Group = -> [Sketch005,Pad002,Sketch006,Pad003,Sketch007,Pad004,Fillet,DatumPlane,Sketch008,Pad005,DatumPlane001,Sketch009,DatumLine,Revolution]
  Origin = -> Origin001
  Placement = pos=(0.291005,-51,25.9599) rot=(-0.793353,0,0.608761;3.14159rad)
  Tip = -> Revolution
  _ExportChildren = -> [Pad002,Pad003,Pad004,Fillet,DatumPlane,Pad005,DatumPlane001,DatumLine,Revolution]
  _GroupVersion = 1
FEATURE [App::Link] Link001  label="Link001(HGH20CA)"
  AutoLinkLabel = true
  LinkedObject = -> Body
  SyncGroupVisibility = false
  _LinkVersion = 1
FEATURE [App::Link] Link002  label="Link002(Greaser)"
  AutoLinkLabel = true
  LinkPlacement = pos=(-9e-16,36.4,24.1) rot=(0,-1,0;4.45059rad)
  LinkedObject = -> Body001
  Placement = pos=(-9e-16,36.4,24.1) rot=(0,-1,0;4.45059rad)
  SyncGroupVisibility = false
  _LinkVersion = 1
FEATURE [Part::FeaturePython] Screw  label="M6x8-Screw"  # Fasteners workbench fastener (typed FeaturePython)
  Placement = pos=(0,-36.4,24.1) rot=(1,0,0;1.5708rad)
  diameter = 4
  invert = false
  length = 13
  lengthCustom = 8
  matchOuter = false
  offset = 0
  thread = false
  type = 39
FEATURE [Part::FeaturePython] Parts  # WARN: FeaturePython — macro-defined, semantics opaque (R4)
  Group = -> [Link001,Link002,Screw]
  GroupMode = 0
  _LinkVersion = 1
FEATURE [App::Link] Link003  label="Link003(Greaser)"
  AutoLinkLabel = true
  LinkPlacement = pos=(-1e-16,-36.4,24.1) rot=(-0.793353,0,-0.608761;3.14159rad)
  LinkedObject = -> Body001
  Placement = pos=(-1e-16,-36.4,24.1) rot=(-0.793353,0,-0.608761;3.14159rad)
  SyncGroupVisibility = false
  _LinkVersion = 1
FEATURE [App::Link] Link004  label="Link004(HGH20CA)"
  AutoLinkLabel = true
  LinkedObject = -> Body
  SyncGroupVisibility = false
  _LinkVersion = 1
FEATURE [Part::FeaturePython] Screw001  label="M6x8-Screw001"  # Fasteners workbench fastener (typed FeaturePython)
  Placement = pos=(0,36.4,24.1) rot=(-1,0,0;1.5708rad)
  diameter = 4
  invert = false
  length = 13
  lengthCustom = 8
  matchOuter = false
  offset = 0
  thread = false
  type = 39
FEATURE [Part::FeaturePython] Parts001  # WARN: FeaturePython — macro-defined, semantics opaque (R4)
  Group = -> [Link003,Link004,Screw001]
  GroupMode = 0
  _LinkVersion = 1
FEATURE [Sketcher::SketchObject] Sketch010
  FullyConstrained = true
  MapMode = 5
  Placement = pos=(0,0,0) rot=(1,0,0;1.5708rad)
  Support = -> [XZ_Plane]
  sketch-geometry (29):
    g0: LineSegment StartX=-9 StartY=0 StartZ=0 EndX=-10 EndY=1 EndZ=0
    g1: LineSegment StartX=-10 StartY=1 StartZ=0 EndX=-10 EndY=4 EndZ=0
    g2: LineSegment StartX=-10 StartY=4 StartZ=0 EndX=-6.6 EndY=7.45 EndZ=0
    g3: LineSegment StartX=-6.6 StartY=7.45 StartZ=0 EndX=-6.6 EndY=9.95 EndZ=0
    g4: LineSegment StartX=-6.6 StartY=9.95 StartZ=0 EndX=-7.65996 EndY=11.05 EndZ=0
    g5: ArcOfCircle CenterX=-9.8 CenterY=10.8 CenterZ=0 NormalX=0 NormalY=0 NormalZ=1 AngleXU=0 Radius=2.15459 StartAngle=0.116293 EndAngle=1.47784
    g6: LineSegment StartX=-9.6 StartY=12.9453 StartZ=0 EndX=-10 EndY=13.3453 EndZ=0
    g7: LineSegment StartX=-10 StartY=13.3453 StartZ=0 EndX=-10 EndY=14.6953 EndZ=0
    g8: LineSegment StartX=-10 StartY=14.6953 StartZ=0 EndX=-9.6 EndY=15.0953 EndZ=0
    g9: ArcOfCircle CenterX=-9.8 CenterY=17.2406 CenterZ=0 NormalX=0 NormalY=0 NormalZ=1 AngleXU=0 Radius=2.15459 StartAngle=4.80535 EndAngle=6.21789
    g10: LineSegment StartX=-7.65 StartY=17.1 StartZ=0 EndX=-7.25 EndY=17.5 EndZ=0
    g11: LineSegment StartX=-7.25 StartY=17.5 StartZ=0 EndX=0 EndY=17.5 EndZ=0
    g12: LineSegment StartX=0 StartY=17.5 StartZ=0 EndX=7.25 EndY=17.5 EndZ=0
    g13: LineSegment StartX=7.25 StartY=17.5 StartZ=0 EndX=7.65 EndY=17.1 EndZ=0
    g14: ArcOfCircle CenterX=9.8 CenterY=17.2406 CenterZ=0 NormalX=0 NormalY=0 NormalZ=1 AngleXU=0 Radius=2.15459 StartAngle=3.20688 EndAngle=4.61943
    g15: LineSegment StartX=9.6 StartY=15.0953 StartZ=0 EndX=10 EndY=14.6953 EndZ=0
    g16: LineSegment StartX=10 StartY=14.6953 StartZ=0 EndX=10 EndY=13.3453 EndZ=0
    g17: LineSegment StartX=10 StartY=13.3453 StartZ=0 EndX=9.6 EndY=12.9453 EndZ=0
    g18: ArcOfCircle CenterX=9.8 CenterY=10.8 CenterZ=0 NormalX=0 NormalY=0 NormalZ=1 AngleXU=0 Radius=2.15459 StartAngle=1.66376 EndAngle=3.0253
    g19: LineSegment StartX=7.65996 StartY=11.05 StartZ=0 EndX=6.6 EndY=9.95 EndZ=0
    g20: LineSegment StartX=6.6 StartY=9.95 StartZ=0 EndX=6.6 EndY=7.45 EndZ=0
    g21: LineSegment StartX=6.6 StartY=7.45 StartZ=0 EndX=10 EndY=4 EndZ=0
    g22: LineSegment StartX=10 StartY=4 StartZ=0 EndX=10 EndY=1 EndZ=0
    g23: LineSegment StartX=10 StartY=1 StartZ=0 EndX=9 EndY=0 EndZ=0
    g24: LineSegment StartX=-4 StartY=0 StartZ=0 EndX=-4 EndY=0.4 EndZ=0
    g25: LineSegment StartX=-4 StartY=0.4 StartZ=0 EndX=4 EndY=0.4 EndZ=0
    g26: LineSegment StartX=4 StartY=0.4 StartZ=0 EndX=4 EndY=0 EndZ=0
    g27: LineSegment StartX=-9 StartY=0 StartZ=0 EndX=-4 EndY=0 EndZ=0
    g28: LineSegment StartX=4 StartY=0 StartZ=0 EndX=9 EndY=0 EndZ=0
  constraints (89):
    c: Coincident(g0,g1)
    c: Vertical(g1)
    c: Coincident(g1,g2)
    c: Coincident(g2,g3)
    c: Vertical(g3)
    c: Coincident(g3,g4)
    c: Coincident(g5,g4)
    c: Coincident(g6,g5)
    c: Coincident(g6,g7)
    c: Vertical(g7)
    c: Coincident(g7,g8)
    c: Coincident(g9,g8)
    c: Coincident(g9,g10)
    c: Coincident(g10,g11)
    c: PointOnObject(g11,g-2)
    c: Horizontal(g11)
    c: Coincident(g11,g12)
    c: Horizontal(g12)
    c: Coincident(g12,g13)
    c: Coincident(g14,g13)
    c: Coincident(g14,g15)
    c: Coincident(g15,g16)
    c: Coincident(g16,g17)
    c: Coincident(g18,g17)
    c: Coincident(g18,g19)
    c: Coincident(g19,g20)
    c: Vertical(g20)
    c: Coincident(g20,g21)
    c: Coincident(g21,g22)
    c: Vertical(g22)
    c: Coincident(g22,g23)
    c: PointOnObject(g23,g-1)
    c: Equal(g0,g23)
    c: Equal(g22,g1)
    c: Equal(g2,g21)
    c: Equal(g20,g3)
    c: Equal(g4,g19)
    c: Equal(g5,g18)
    c: Equal(g18,g14)
    c: Equal(g14,g9)
    c: Equal(g15,g17)
    c: Vertical(g16)
    c: Equal(g16,g7)
    c: Equal(g10,g13)
    c: Equal(g12,g11)
    c: DistanceX(g10,g12) = 14.5
    c: Horizontal(g22,g0)
    c: DistanceX(g0,g22) = 20
    c: Horizontal(g2,g20)
    c: DistanceX(g0,g23) = 18
    c: DistanceY(g23,g22) = 1
    c: DistanceY(g22,g22) = 3
    c: DistanceX(g2,g20) = 13.2
    c: DistanceY(g21,g20) = 3.45
    c: DistanceY(g20,g20) = 2.5
    c: Horizontal(g18,g5)
    c: Horizontal(g18,g4)
    c: Horizontal(g9,g13)
    c: Horizontal(g9,g14)
    c: Vertical(g9,g5)
    c: DistanceX(g9,g13) = 15.3
    c: DistanceY(g13,g12) = 0.4
    c: Vertical(g15,g21)
    c: Vertical(g7,g1)
    c: Equal(g13,g15)
    c: Equal(g17,g6)
    c: Equal(g6,g8)
    c: DistanceY(g19,g18) = 1.1
    c: DistanceY(g23,g18) = 10.8
    c: DistanceX(g5,g17) = 19.2
    c: DistanceY(g23,g12) = 17.5
    c: DistanceY(g17,g16) = 0.4
    c: DistanceY(g15,g14) = 0.4
    c: DistanceY(g7,g7) = 1.35
    c: DistanceX(g-1,g18) = 9.8
    c: Coincident(g24,g25)
    c: Horizontal(g25)
    c: Coincident(g25,g26)
    c: Vertical(g26)
    c: Vertical(g24)
    c: Symmetric(g26,g24,g-1)
    c: Coincident(g27,g0)
    c: Coincident(g27,g24)
    c: Horizontal(g27)
    c: Coincident(g28,g26)
    c: Coincident(g28,g23)
    c: DistanceX(g25,g25) = 8
    c: DistanceY(g26,g26) = 0.4
    c: Symmetric(g23,g0,g-1)
FEATURE [PartDesign::Pocket] Pocket002
  BaseFeature = -> Mirrored
  ClaimChildren = false
  Fit = 0
  FitJoin = 0
  InnerFit = 0
  InnerFitJoin = 0
  InnerTaperAngle = 0
  InnerTaperAngleRev = 0
  Length = 5
  Length2 = 100
  Linearize = true
  Midplane = true
  NewSolid = false
  Placement = pos=(0,0,0) rot=(1,0,0;1.5708rad)
  Profile = -> Sketch010
  Refine = true
  Suppress = false
  Type = 1
FEATURE [PartDesign::Pocket] Pocket003
  BaseFeature = -> Pocket002
  ClaimChildren = false
  Fit = 0
  FitJoin = 0
  InnerFit = 0
  InnerFitJoin = 0
  InnerTaperAngle = 0
  InnerTaperAngleRev = 0
  Length = 9
  Length2 = 100
  Linearize = true
  NewSolid = false
  Placement = pos=(0,0,0) rot=(1,0,0;1.5708rad)
  Profile = -> Sketch001
  Refine = true
  Suppress = false
  Type = 0
FEATURE [PartDesign::Body] Body  label="HGH20CA"
  AutoGroupSolids = false
  ExportMode = 0
  Group = -> [Sketch,Pad,Sketch001,Sketch002,Pad001,Sketch003,Pocket,Sketch004,Pocket001,Mirrored,Sketch010,Pocket002,Pocket003]
  Origin = -> Origin
  Tip = -> Pocket003
  _ExportChildren = -> [Pad,Pad001,Pocket,Pocket001,Mirrored,Pocket002,Pocket003]
  _GroupVersion = 1
FEATURE [App::DocumentObjectGroup] Group  label="Components"
  ExportMode = 1
  Group = -> [Body,Body001]
  _GroupVersion = 1
FEATURE [Part::FeaturePython] Assembly  label="HGH20CA-L-Assembly"  # WARN: FeaturePython — macro-defined, semantics opaque (R4)
  AutoRelax = true
  BuildShape = 0
  Freeze = false
  Group = -> [Constraints,Elements,Parts]
  Placement = pos=(0,54,-7.15256e-07) rot=(0,0,1;0rad)
  Verbose = false
  _LinkVersion = 1
  _SolverType = 1
  _Version = 1
FEATURE [App::FeaturePython] Constraints  # WARN: FeaturePython — macro-defined, semantics opaque (R4)
  Group = -> [Constraint,Constraint001,Constraint002]
  _LinkVersion = 1
  _Version = 1
FEATURE [App::FeaturePython] Elements  # WARN: FeaturePython — macro-defined, semantics opaque (R4)
  Group = -> [_Element,_Element001,_Element002,_Element003,_Element004,Element004]
  _LinkVersion = 1
FEATURE [App::FeaturePython] Constraint  label="Locked"  # WARN: FeaturePython — macro-defined, semantics opaque (R4)
  Disabled = false
  Group = -> [ElementLink]
  _ConstraintType = 0
  _LinkVersion = 1
  _Parent = -> Constraints
FEATURE [App::FeaturePython] ElementLink  label="_Element"  # link proxy (typed FeaturePython)
  LinkTransform = true
  LinkedObject = -> _Element
  _LinkVersion = 1
  _Parent = -> Constraint
FEATURE [Part::FeaturePython] _Element  # link proxy (typed FeaturePython)
  Detach = false
  LinkTransform = true
  LinkedObject = -> Link001 [Pocket003.Face62]
  _LinkVersion = 1
  _Parent = -> Elements
FEATURE [App::FeaturePython] Constraint001  label="Attachment"  # WARN: FeaturePython — macro-defined, semantics opaque (R4)
  Cascade = false
  Disabled = false
  Group = -> [ElementLink001,ElementLink002]
  Multiply = false
  _ConstraintType = 45
  _LinkVersion = 1
  _Parent = -> Constraints
FEATURE [App::FeaturePython] ElementLink001  label="_Element001"  # link proxy (typed FeaturePython)
  LinkTransform = true
  LinkedObject = -> _Element001
  Offset = pos=(0,0,0) rot=(0,0,1;1.8326rad)
  Placement = pos=(23.2788,-2.84e-14,30.3375) rot=(0,-1,0;1.8326rad)
  _LinkVersion = 1
  _Parent = -> Constraint001
FEATURE [Part::FeaturePython] _Element001  # link proxy (typed FeaturePython)
  Detach = false
  LinkTransform = true
  LinkedObject = -> Link002 [Revolution.Edge59]
  _LinkVersion = 1
  _Parent = -> Elements
FEATURE [App::FeaturePython] ElementLink002  label="_Element002"  # link proxy (typed FeaturePython)
  LinkTransform = true
  LinkedObject = -> _Element002
  _LinkVersion = 1
  _Parent = -> Constraint001
FEATURE [Part::FeaturePython] _Element002  # link proxy (typed FeaturePython)
  Detach = false
  LinkTransform = true
  LinkedObject = -> Link001 [Pocket003.Edge186]
  _LinkVersion = 1
  _Parent = -> Elements
FEATURE [App::FeaturePython] Constraint002  label="Attachment001"  # WARN: FeaturePython — macro-defined, semantics opaque (R4)
  Cascade = false
  Disabled = false
  Group = -> [ElementLink003,ElementLink004]
  Multiply = false
  _ConstraintType = 45
  _LinkVersion = 1
  _Parent = -> Constraints
FEATURE [App::FeaturePython] ElementLink003  label="_Element003"  # link proxy (typed FeaturePython)
  LinkTransform = true
  LinkedObject = -> _Element003
  _LinkVersion = 1
  _Parent = -> Constraint002
FEATURE [Part::FeaturePython] _Element003  # link proxy (typed FeaturePython)
  Detach = false
  LinkTransform = true
  LinkedObject = -> Screw [Edge4]
  _LinkVersion = 1
  _Parent = -> Elements
FEATURE [App::FeaturePython] ElementLink004  label="_Element004"  # link proxy (typed FeaturePython)
  LinkTransform = true
  LinkedObject = -> _Element004
  _LinkVersion = 1
  _Parent = -> Constraint002
FEATURE [Part::FeaturePython] _Element004  # link proxy (typed FeaturePython)
  Detach = false
  LinkTransform = true
  LinkedObject = -> Link001 [Pocket003.Edge234]
  _LinkVersion = 1
  _Parent = -> Elements
FEATURE [Part::FeaturePython] Assembly001  label="HGH20CA-R-Assembly"  # WARN: FeaturePython — macro-defined, semantics opaque (R4)
  AutoRelax = true
  BuildShape = 0
  Freeze = false
  Group = -> [Constraints001,Elements001,Parts001]
  Placement = pos=(0,-36,-7.15256e-07) rot=(0,0,1;0rad)
  Verbose = false
  _LinkVersion = 1
  _SolverType = 1
  _Version = 1
FEATURE [App::FeaturePython] Constraints001  # WARN: FeaturePython — macro-defined, semantics opaque (R4)
  Group = -> [Constraint003,Constraint004,Constraint005]
  _LinkVersion = 1
  _Version = 1
FEATURE [App::FeaturePython] Elements001  # WARN: FeaturePython — macro-defined, semantics opaque (R4)
  Group = -> [_Element005,_Element006,_Element007,_Element008,_Element009,Element,Element001,Element002,Element003]
  _LinkVersion = 1
FEATURE [App::FeaturePython] Constraint003  label="Locked001"  # WARN: FeaturePython — macro-defined, semantics opaque (R4)
  Disabled = false
  Group = -> [ElementLink005]
  _ConstraintType = 0
  _LinkVersion = 1
  _Parent = -> Constraints001
FEATURE [App::FeaturePython] ElementLink005  label="_Element005"  # link proxy (typed FeaturePython)
  LinkTransform = true
  LinkedObject = -> _Element005
  _LinkVersion = 1
  _Parent = -> Constraint003
FEATURE [Part::FeaturePython] _Element005  # link proxy (typed FeaturePython)
  Detach = false
  LinkTransform = true
  LinkedObject = -> Link004 [Pocket003.Face62]
  _LinkVersion = 1
  _Parent = -> Elements001
FEATURE [App::FeaturePython] Constraint004  label="Attachment002"  # WARN: FeaturePython — macro-defined, semantics opaque (R4)
  Cascade = false
  Disabled = false
  Group = -> [ElementLink006,ElementLink007]
  Multiply = false
  _ConstraintType = 45
  _LinkVersion = 1
  _Parent = -> Constraints001
FEATURE [App::FeaturePython] ElementLink006  label="_Element006"  # link proxy (typed FeaturePython)
  LinkTransform = true
  LinkedObject = -> _Element006
  Offset = pos=(0,0,0) rot=(1,0,0;3.14159rad)
  Placement = pos=(0,-72.8,48.2) rot=(1,0,0;3.14159rad)
  _LinkVersion = 1
  _Parent = -> Constraint004
FEATURE [Part::FeaturePython] _Element006  # link proxy (typed FeaturePython)
  Detach = false
  LinkTransform = true
  LinkedObject = -> Link004 [Pocket003.Edge234]
  _LinkVersion = 1
  _Parent = -> Elements001
FEATURE [App::FeaturePython] ElementLink007  label="_Element007"  # link proxy (typed FeaturePython)
  LinkTransform = true
  LinkedObject = -> _Element007
  Offset = pos=(0,0,0) rot=(0,0,1;1.309rad)
  Placement = pos=(-23.2788,2.13e-14,17.8625) rot=(0,1,0;1.309rad)
  _LinkVersion = 1
  _Parent = -> Constraint004
FEATURE [Part::FeaturePython] _Element007  # link proxy (typed FeaturePython)
  Detach = false
  LinkTransform = true
  LinkedObject = -> Link003 [Revolution.Edge59]
  _LinkVersion = 1
  _Parent = -> Elements001
FEATURE [App::FeaturePython] Constraint005  label="Attachment003"  # WARN: FeaturePython — macro-defined, semantics opaque (R4)
  Cascade = false
  Disabled = false
  Group = -> [ElementLink008,ElementLink009]
  Multiply = false
  _ConstraintType = 45
  _LinkVersion = 1
  _Parent = -> Constraints001
FEATURE [App::FeaturePython] ElementLink008  label="_Element008"  # link proxy (typed FeaturePython)
  LinkTransform = true
  LinkedObject = -> _Element008
  Offset = pos=(0,0,0) rot=(1,0,0;3.14159rad)
  Placement = pos=(0,72.8,48.2) rot=(1,0,0;3.14159rad)
  _LinkVersion = 1
  _Parent = -> Constraint005
FEATURE [Part::FeaturePython] _Element008  # link proxy (typed FeaturePython)
  Detach = false
  LinkTransform = true
  LinkedObject = -> Link004 [Pocket003.Edge186]
  _LinkVersion = 1
  _Parent = -> Elements001
FEATURE [App::FeaturePython] ElementLink009  label="_Element009"  # link proxy (typed FeaturePython)
  LinkTransform = true
  LinkedObject = -> _Element009
  _LinkVersion = 1
  _Parent = -> Constraint005
FEATURE [Part::FeaturePython] _Element009  # link proxy (typed FeaturePython)
  Detach = false
  LinkTransform = true
  LinkedObject = -> Screw001 [Edge4]
  _LinkVersion = 1
  _Parent = -> Elements001
FEATURE [App::DocumentObjectGroup] Group001  label="Assemblies"
  ExportMode = 1
  Group = -> [Assembly,Assembly001]
  _GroupVersion = 1
FEATURE [Part::FeaturePython] Element  label="top-mate"  # link proxy (typed FeaturePython)
  Detach = false
  LinkTransform = true
  LinkedObject = -> Link004 [Pocket003.Face13]
  _LinkVersion = 1
  _Parent = -> Elements001
FEATURE [Part::FeaturePython] Element001  label="side-mate"  # link proxy (typed FeaturePython)
  Detach = false
  LinkTransform = true
  LinkedObject = -> Link004 [Pocket003.Face17]
  _LinkVersion = 1
  _Parent = -> Elements001
FEATURE [Part::FeaturePython] Element002  label="point"  # link proxy (typed FeaturePython)
  Detach = false
  LinkTransform = true
  LinkedObject = -> Link004 [Pocket003.Vertex56]
  _LinkVersion = 1
  _Parent = -> Elements001
FEATURE [Part::FeaturePython] Element003  label="shim-br"  # link proxy (typed FeaturePython)
  Detach = false
  LinkTransform = true
  LinkedObject = -> Link004 [Pocket003.Edge212]
  _LinkVersion = 1
  _Parent = -> Elements001
FEATURE [Part::FeaturePython] Element004  label="shim-tr"  # link proxy (typed FeaturePython)
  Detach = false
  LinkTransform = true
  LinkedObject = -> Link001 [Pocket003.Edge213]
  _LinkVersion = 1
  _Parent = -> Elements
---- part parts/HGR20.FCStd = doc fcstd_98294569bf8e (65349 chars; too large to inline — full recipe in that document) ----
---- part parts/LimitSensor.FCStd = doc fcstd_3f7c24fee6a1 ----
FCSTD DOCUMENT  (FreeCAD 2021.717R24301 +3842 (Git))
Label: LimitSensor
License: Creative Commons Attribution
LicenseURL: http://creativecommons.org/licenses/by/4.0/
objects: App::FeaturePython×10, Part::FeaturePython×8, Sketcher::SketchObject×6, PartDesign::Pocket×4, App::Link×2, App::DocumentObjectGroup×2, App::LinkElement×2, PartDesign::Pad×1, PartDesign::Mirrored×1, PartDesign::Body×1
note: 32 computed .brp shape members not serialized (recipe doc carries the construction recipe); baked Part::Feature solids carry a one-line shape summary decoded from their .brp

FEATURE [Sketcher::SketchObject] Sketch
  FullyConstrained = true
  MapMode = 5
  Placement = pos=(0,0,0) rot=(1,0,0;1.5708rad)
  Support = -> [XZ_Plane]
  sketch-geometry (4):
    g0: LineSegment StartX=-9 StartY=15.25 StartZ=0 EndX=9 EndY=15.25 EndZ=0
    g1: LineSegment StartX=9 StartY=15.25 StartZ=0 EndX=9 EndY=-15.25 EndZ=0
    g2: LineSegment StartX=9 StartY=-15.25 StartZ=0 EndX=-9 EndY=-15.25 EndZ=0
    g3: LineSegment StartX=-9 StartY=-15.25 StartZ=0 EndX=-9 EndY=15.25 EndZ=0
  constraints (11):
    c: Coincident(g0,g1)
    c: Coincident(g1,g2)
    c: Coincident(g2,g3)
    c: Coincident(g3,g0)
    c: Horizontal(g0)
    c: Horizontal(g2)
    c: Vertical(g1)
    c: Vertical(g3)
    c: Symmetric(g1,g0,g-1)
    c: DistanceX(g0,g0) = 18
    c: DistanceY(g1,g1) = 30.5
FEATURE [PartDesign::Pad] Pad
  ClaimChildren = false
  Direction = (1,1,1)
  Fit = 0
  FitJoin = 0
  InnerFit = 0
  InnerFitJoin = 0
  InnerTaperAngle = 0
  InnerTaperAngleRev = 0
  Length = 10
  Length2 = 100
  Linearize = true
  NewSolid = false
  Placement = pos=(0,0,0) rot=(1,0,0;1.5708rad)
  Profile = -> Sketch
  Refine = true
  Suppress = false
  Type = 0
  _ProfileBasedVersion = 1
FEATURE [Sketcher::SketchObject] Sketch001
  FullyConstrained = true
  MapMode = 5
  Placement = pos=(0,-10,2.2e-15) rot=(1,0,0;1.5708rad)
  Support = -> [Pad]
  sketch-geometry (4):
    g0: LineSegment StartX=-9 StartY=15.25 StartZ=0 EndX=9 EndY=15.25 EndZ=0
    g1: LineSegment StartX=9 StartY=15.25 StartZ=0 EndX=9 EndY=7 EndZ=0
    g2: LineSegment StartX=9 StartY=7 StartZ=0 EndX=-9 EndY=7 EndZ=0
    g3: LineSegment StartX=-9 StartY=7 StartZ=0 EndX=-9 EndY=15.25 EndZ=0
  constraints (11):
    c: Coincident(g0,g1)
    c: Coincident(g1,g2)
    c: Coincident(g2,g3)
    c: Coincident(g3,g0)
    c: Horizontal(g0)
    c: Vertical(g1)
    c: Vertical(g3)
    c: Symmetric(g1,g2,g-2)
    c: DistanceX(g0,g0) = 18
    c: DistanceY(g1,g1) = 8.25
    c: DistanceY(g-1,g1) = 7
FEATURE [PartDesign::Pocket] Pocket
  BaseFeature = -> Pad
  ClaimChildren = false
  Fit = 0
  FitJoin = 0
  InnerFit = 0
  InnerFitJoin = 0
  InnerTaperAngle = 0
  InnerTaperAngleRev = 0
  Length = 2
  Length2 = 100
  Linearize = true
  NewSolid = false
  Placement = pos=(0,0,0) rot=(1,0,0;1.5708rad)
  Profile = -> Sketch001
  Refine = true
  Suppress = false
  Type = 0
  _ProfileBasedVersion = 1
FEATURE [Sketcher::SketchObject] Sketch002
  FullyConstrained = true
  MapMode = 5
  Placement = pos=(0,-8,6.9e-15) rot=(1,0,0;1.5708rad)
  Support = -> [Pocket]
  sketch-geometry (4):
    g0: ArcOfCircle CenterX=-6 CenterY=11.25 CenterZ=0 NormalX=0 NormalY=0 NormalZ=1 AngleXU=0 Radius=1.75 StartAngle=0 EndAngle=3.14159
    g1: ArcOfCircle CenterX=-6 CenterY=9.75 CenterZ=0 NormalX=0 NormalY=0 NormalZ=1 AngleXU=0 Radius=1.75 StartAngle=3.14159 EndAngle=6.28319
    g2: LineSegment StartX=-7.75 StartY=11.25 StartZ=0 EndX=-7.75 EndY=9.75 EndZ=0
    g3: LineSegment StartX=-4.25 StartY=11.25 StartZ=0 EndX=-4.25 EndY=9.75 EndZ=0
  constraints (10):
    c: Tangent(g0,g3) = 1.5708
    c: Tangent(g0,g2) = -1.5708
    c: Tangent(g2,g1) = -1.5708
    c: Tangent(g3,g1) = 1.5708
    c: Vertical(g2)
    c: Equal(g0,g1)
    c: DistanceY(g3,g3) = 1.5
    c: Diameter(g0) = 3.5
    c: DistanceY(g-1,g0) = 11.25
    c: DistanceX(g0,g-1) = 6
FEATURE [PartDesign::Pocket] Pocket001
  BaseFeature = -> Pocket
  ClaimChildren = false
  Fit = 0
  FitJoin = 0
  InnerFit = 0
  InnerFitJoin = 0
  InnerTaperAngle = 0
  InnerTaperAngleRev = 0
  Length = 5
  Length2 = 100
  Linearize = true
  NewSolid = false
  Placement = pos=(0,0,0) rot=(1,0,0;1.5708rad)
  Profile = -> Sketch002
  Refine = true
  Suppress = false
  Type = 1
  _ProfileBasedVersion = 1
FEATURE [Sketcher::SketchObject] Sketch003
  ExternalGeometry = -> [Pocket001]
  FullyConstrained = true
  MapMode = 5
  Placement = pos=(0,-8,6.9e-15) rot=(1,0,0;1.5708rad)
  Support = -> [Pocket001]
  sketch-geometry (6):
    g0: LineSegment StartX=-9 StartY=15.25 StartZ=0 EndX=-2 EndY=15.25 EndZ=0
    g1: LineSegment StartX=-2 StartY=15.25 StartZ=0 EndX=-2 EndY=9 EndZ=0
    g2: LineSegment StartX=-4 StartY=7 StartZ=0 EndX=-9 EndY=7 EndZ=0
    g3: LineSegment StartX=-9 StartY=7 StartZ=0 EndX=-9 EndY=15.25 EndZ=0
    g4: ArcOfCircle CenterX=-4 CenterY=9 CenterZ=0 NormalX=0 NormalY=0 NormalZ=1 AngleXU=0 Radius=2 StartAngle=4.71239 EndAngle=6.28319
    g5: GeomPoint [constr] X=-2 Y=7 Z=0
  constraints (16):
    c: Coincident(g0,g1)
    c: Coincident(g2,g3)
    c: Coincident(g3,g0)
    c: Horizontal(g0)
    c: Horizontal(g2)
    c: Vertical(g1)
    c: Vertical(g3)
    c: DistanceX(g2,g-1) = 9
    c: DistanceY(g-1,g0) = 15.25
    c: Horizontal(g-3,g2)
    c: DistanceX(g0,g0) = 7
    c: PointOnObject(g5,g1)
    c: PointOnObject(g5,g2)
    c: Tangent(g1,g4) = 1.5708
    c: Tangent(g2,g4) = 1.5708
    c: Radius(g4) = 2
FEATURE [PartDesign::Pocket] Pocket002
  BaseFeature = -> Pocket001
  ClaimChildren = false
  Fit = 0
  FitJoin = 0
  InnerFit = 0
  InnerFitJoin = 0
  InnerTaperAngle = 0
  InnerTaperAngleRev = 0
  Length = 1.5
  Length2 = 100
  Linearize = true
  NewSolid = false
  Placement = pos=(0,0,0) rot=(1,0,0;1.5708rad)
  Profile = -> Sketch003
  Refine = true
  Suppress = false
  Type = 0
  _ProfileBasedVersion = 1
FEATURE [PartDesign::Mirrored] Mirrored
  BaseFeature = -> Pocket002
  CopyShape = false
  MirrorPlane = -> Sketch003 [V_Axis]
  NewSolid = false
  OriginalSubs = -> [Pocket002,Pocket001]
  Originals = -> [Pocket002,Pocket001]
  ParallelTransform = true
  Placement = pos=(0,0,0) rot=(1,0,0;1.5708rad)
  Refine = true
  SubTransform = true
  Suppress = false
  _Version = 2
FEATURE [Sketcher::SketchObject] Sketch004
  FullyConstrained = false
  MapMode = 5
  Placement = pos=(0,-10,2.2e-15) rot=(1,0,0;1.5708rad)
  Support = -> [Mirrored]
  sketch-geometry (30):
    g0: LineSegment StartX=-7.75 StartY=5.75 StartZ=0 EndX=7.75 EndY=5.75 EndZ=0
    g1: LineSegment StartX=7.75 StartY=5.75 StartZ=0 EndX=7.75 EndY=0.25 EndZ=0
    g2: LineSegment StartX=7.75 StartY=0.25 StartZ=0 EndX=-7.75 EndY=0.25 EndZ=0
    g3: LineSegment StartX=-7.75 StartY=0.25 StartZ=0 EndX=-7.75 EndY=5.75 EndZ=0
    g4: Circle CenterX=0 CenterY=-7 CenterZ=0 NormalX=0 NormalY=0 NormalZ=1 AngleXU=0 Radius=6
    g5: ArcOfCircle CenterX=0 CenterY=-7 CenterZ=0 NormalX=0 NormalY=0 NormalZ=1 AngleXU=0 Radius=5.5 StartAngle=3.18706 EndAngle=4.66692
    g6: ArcOfCircle CenterX=0 CenterY=-7 CenterZ=0 NormalX=0 NormalY=0 NormalZ=1 AngleXU=0 Radius=3.175 StartAngle=3.22041 EndAngle=4.63357
    g7: ArcOfCircle CenterX=0 CenterY=-7 CenterZ=0 NormalX=0 NormalY=0 NormalZ=1 AngleXU=0 Radius=2.675 StartAngle=3.23519 EndAngle=4.61879
    g8: LineSegment StartX=-5.49432 StartY=-6.75 StartZ=0 EndX=-3.16514 EndY=-6.75 EndZ=0
    g9: LineSegment StartX=-5.49432 StartY=-7.25 StartZ=0 EndX=-3.16514 EndY=-7.25 EndZ=0
    g10: LineSegment StartX=0.25 StartY=-1.50568 StartZ=0 EndX=0.25 EndY=-3.83486 EndZ=0
    g11: LineSegment StartX=-0.25 StartY=-1.50568 StartZ=0 EndX=-0.25 EndY=-3.83486 EndZ=0
    g12: LineSegment [constr] StartX=-7.32001 StartY=-7 StartZ=0 EndX=7.24789 EndY=-7 EndZ=0
    g13: ArcOfCircle CenterX=0 CenterY=-7 CenterZ=0 NormalX=0 NormalY=0 NormalZ=1 AngleXU=0 Radius=2.675 StartAngle=0.0935945 EndAngle=1.4772
    g14: ArcOfCircle CenterX=0 CenterY=-7 CenterZ=0 NormalX=0 NormalY=0 NormalZ=1 AngleXU=0 Radius=3.175 StartAngle=0.0788218 EndAngle=1.49197
    g15: ArcOfCircle CenterX=0 CenterY=-7 CenterZ=0 NormalX=0 NormalY=0 NormalZ=1 AngleXU=0 Radius=5.5 StartAngle=0.0454702 EndAngle=1.52533
    g16: LineSegment StartX=3.16514 StartY=-7.25 StartZ=0 EndX=5.49432 EndY=-7.25 EndZ=0
    g17: LineSegment StartX=3.16514 StartY=-6.75 StartZ=0 EndX=5.49432 EndY=-6.75 EndZ=0
    g18: LineSegment StartX=-2.66329 StartY=-6.75 StartZ=0 EndX=2.66329 EndY=-6.75 EndZ=0
    g19: LineSegment StartX=-2.66329 StartY=-7.25 StartZ=0 EndX=2.66329 EndY=-7.25 EndZ=0
    g20: LineSegment StartX=-0.25 StartY=-4.33671 StartZ=0 EndX=-0.25 EndY=-9.66329 EndZ=0
    g21: LineSegment StartX=0.25 StartY=-4.33671 StartZ=0 EndX=0.25 EndY=-9.66329 EndZ=0
    g22: ArcOfCircle CenterX=0 CenterY=-7 CenterZ=0 NormalX=0 NormalY=0 NormalZ=1 AngleXU=0 Radius=2.675 StartAngle=1.66439 EndAngle=3.048
    g23: ArcOfCircle CenterX=0 CenterY=-7 CenterZ=0 NormalX=0 NormalY=0 NormalZ=1 AngleXU=0 Radius=2.675 StartAngle=4.80598 EndAngle=6.18959
    g24: ArcOfCircle CenterX=0 CenterY=-7 CenterZ=0 NormalX=0 NormalY=0 NormalZ=1 AngleXU=0 Radius=3.175 StartAngle=4.79121 EndAngle=6.20436
    g25: LineSegment StartX=0.25 StartY=-10.1651 StartZ=0 EndX=0.25 EndY=-12.4943 EndZ=0
    g26: LineSegment StartX=-0.25 StartY=-10.1651 StartZ=0 EndX=-0.25 EndY=-12.4943 EndZ=0
    g27: ArcOfCircle CenterX=0 CenterY=-7 CenterZ=0 NormalX=0 NormalY=0 NormalZ=1 AngleXU=0 Radius=5.5 StartAngle=4.75786 EndAngle=6.23772
    g28: ArcOfCircle CenterX=0 CenterY=-7 CenterZ=0 NormalX=0 NormalY=0 NormalZ=1 AngleXU=0 Radius=5.5 StartAngle=1.61627 EndAngle=3.09612
    g29: ArcOfCircle CenterX=0 CenterY=-7 CenterZ=0 NormalX=0 NormalY=0 NormalZ=1 AngleXU=0 Radius=3.175 StartAngle=1.64962 EndAngle=3.06277
  constraints (80):
    c: Coincident(g0,g1)
    c: Coincident(g1,g2)
    c: Coincident(g2,g3)
    c: Coincident(g3,g0)
    c: Horizontal(g2)
    c: Vertical(g1)
    c: Vertical(g3)
    c: Symmetric(g0,g0,g-2)
    c: DistanceX(g0,g0) = 15.5
    c: DistanceY(g1,g1) = 5.5
    c: PointOnObject(g4,g-2)
    c: Coincident(g5,g4)
    c: Coincident(g6,g4)
    c: Coincident(g7,g4)
    c: Diameter(g7) = 5.35
    c: Diameter(g6) = 6.35
    c: Diameter(g5) = 11
    c: Diameter(g4) = 12
    c: Horizontal(g8)
    c: Horizontal(g9)
    c: PointOnObject(g10,g5)
    c: Vertical(g10)
    c: Vertical(g11)
    c: Symmetric(g11,g10,g-2)
    c: DistanceX(g11,g10) = 0.5
    c: Horizontal(g12)
    c: Symmetric(g17,g16,g12)
    c: DistanceY(g16,g17) = 0.5
    c: Coincident(g28,g8)
    c: Coincident(g5,g9)
    c: Equal(g7,g13)
    c: Coincident(g7,g13)
    c: Equal(g6,g14)
    c: Coincident(g6,g14)
    c: Equal(g5,g15)
    c: Coincident(g15,g17)
    c: Coincident(g5,g15)
    c: Coincident(g27,g16)
    c: Coincident(g19,g23)
    c: Coincident(g16,g24)
    c: Tangent(g9,g16)
    c: Coincident(g18,g13)
    c: Coincident(g17,g14)
    c: Tangent(g8,g17)
    c: Coincident(g8,g29)
    c: Coincident(g18,g22)
    c: Tangent(g8,g18)
    c: Coincident(g9,g6)
    c: Coincident(g19,g7)
    c: Tangent(g9,g19)
    c: Tangent(g11,g20)
    c: Tangent(g10,g21)
    c: Equal(g13,g22)
    c: Coincident(g13,g21)
    c: Coincident(g22,g20)
    c: Coincident(g13,g22)
    c: Equal(g7,g23)
    c: Coincident(g7,g23)
    c: Equal(g6,g24)
    c: Coincident(g6,g24)
    c: Coincident(g21,g23)
    c: Coincident(g25,g24)
    c: Tangent(g21,g25)
    c: Coincident(g20,g7)
    c: Coincident(g26,g6)
    c: Tangent(g20,g26)
    c: Equal(g5,g27)
    c: Coincident(g5,g26)
    c: Coincident(g27,g25)
    c: Coincident(g5,g27)
    c: Equal(g15,g28)
    c: PointOnObject(g15,g10)
    c: PointOnObject(g28,g11)
    c: Coincident(g15,g28)
    c: DistanceY(g4,g-1) = 7
    c: DistanceY(g-1,g1) = 0.25
    c: Equal(g14,g29)
    c: Coincident(g14,g10)
    c: Coincident(g29,g11)
    c: Coincident(g14,g29)
FEATURE [PartDesign::Pocket] Pocket003
  BaseFeature = -> Mirrored
  ClaimChildren = false
  Fit = 0
  FitJoin = 0
  InnerFit = 0
  InnerFitJoin = 0
  InnerTaperAngle = 0
  InnerTaperAngleRev = 0
  Length = 0.2
  Length2 = 100
  Linearize = true
  NewSolid = false
  Placement = pos=(0,0,0) rot=(1,0,0;1.5708rad)
  Profile = -> Sketch004
  Refine = true
  Suppress = false
  Type = 0
  _ProfileBasedVersion = 1
FEATURE [App::Link] Link  label="Link(Limit sensor)"
  AutoLinkLabel = true
  AutoPlacement = true
  LinkedObject = -> Body
  SyncGroupVisibility = false
  _LinkVersion = 1
FEATURE [Sketcher::SketchObject] Sketch005
  ExternalGeometry = -> [Pocket003]
  FullyConstrained = true
  MapMode = 5
  Placement = pos=(0,0,0) rot=(-1,0,0;1.5708rad)
  Support = -> [Pocket003]
  sketch-geometry (2):
    g0: Circle CenterX=-6 CenterY=-10.5 CenterZ=0 NormalX=0 NormalY=0 NormalZ=1 AngleXU=0 Radius=1.5
    g1: Circle CenterX=6 CenterY=-10.5 CenterZ=0 NormalX=0 NormalY=0 NormalZ=1 AngleXU=0 Radius=1.5
  constraints (4):
    c: Symmetric(g-3,g-4,g0)
    c: Symmetric(g-5,g-6,g1)
    c: Equal(g1,g0)
    c: Diameter(g1) = 3
FEATURE [PartDesign::Body] Body  label="Limit sensor"
  AutoGroupSolids = false
  ExportMode = 0
  Group = -> [Sketch,Pad,Sketch001,Pocket,Sketch002,Pocket001,Sketch003,Pocket002,Mirrored,Sketch004,Pocket003,Sketch005]
  Origin = -> Origin
  Tip = -> Pocket003
  _ExportChildren = -> [Pad,Pocket,Pocket001,Pocket002,Mirrored,Pocket003,Sketch005]
  _GroupVersion = 1
FEATURE [Part::FeaturePython] Screw  label="M3x12-Screw"  # Fasteners workbench fastener (typed FeaturePython)
  Placement = pos=(15,-17,-3.8e-15) rot=(1,0,0;1.5708rad)
  diameter = 4
  invert = false
  length = 10
  lengthCustom = 12
  matchOuter = false
  offset = 0
  thread = false
  type = 33
FEATURE [App::DocumentObjectGroup] Group  label="Components"
  ExportMode = 1
  Group = -> [Body,Screw]
  _GroupVersion = 1
FEATURE [App::LinkElement] Link001_i0
  LinkPlacement = pos=(-9,10.5,-10.5) rot=(0,0,1;0rad)
  LinkedObject = -> Screw
  Placement = pos=(-9,10.5,-10.5) rot=(0,0,1;0rad)
  _LinkVersion = 0
FEATURE [App::LinkElement] Link001_i1
  LinkPlacement = pos=(-21,10.5,-10.5) rot=(0,0,1;0rad)
  LinkedObject = -> Screw
  Placement = pos=(-21,10.5,-10.5) rot=(0,0,1;0rad)
  _LinkVersion = 0
FEATURE [App::Link] Link001  label="M3x12-Screw 2pc"
  AutoLinkLabel = true
  AutoPlacement = true
  ElementCount = 2
  ElementList = -> [Link001_i0,Link001_i1]
  LinkPlacement = pos=(15,-17,-3.8e-15) rot=(1,0,0;1.5708rad)
  LinkedObject = -> Screw
  Placement = pos=(15,-17,-3.8e-15) rot=(1,0,0;1.5708rad)
  SyncGroupVisibility = false
  _LinkVersion = 1
FEATURE [Part::FeaturePython] Parts  # WARN: FeaturePython — macro-defined, semantics opaque (R4)
  Group = -> [Link,Link001]
  GroupMode = 0
  _LinkVersion = 1
FEATURE [App::DocumentObjectGroup] Group001  label="Assemblies"
  ExportMode = 1
  Group = -> [Assembly]
  _GroupVersion = 1
FEATURE [Part::FeaturePython] Assembly  label="Limit sensor Assembly"  # WARN: FeaturePython — macro-defined, semantics opaque (R4)
  AutoRelax = true
  BuildShape = 0
  Freeze = false
  Group = -> [Constraints,Elements,Parts]
  Verbose = false
  _LinkVersion = 1
  _SolverType = 1
  _Version = 1
FEATURE [App::FeaturePython] Constraints  # WARN: FeaturePython — macro-defined, semantics opaque (R4)
  Group = -> [Constraint,Constraint001,Constraint002]
  _LinkVersion = 1
  _Version = 1
FEATURE [App::FeaturePython] Elements  # WARN: FeaturePython — macro-defined, semantics opaque (R4)
  Group = -> [_Element,Element,Element001,_Element001,_Element002]
  _LinkVersion = 1
FEATURE [App::FeaturePython] Constraint  label="Locked"  # WARN: FeaturePython — macro-defined, semantics opaque (R4)
  Disabled = false
  Group = -> [ElementLink]
  _ConstraintType = 0
  _LinkVersion = 1
  _Parent = -> Constraints
FEATURE [App::FeaturePython] ElementLink  label="_Element"  # link proxy (typed FeaturePython)
  LinkTransform = true
  LinkedObject = -> _Element
  _LinkVersion = 1
  _Parent = -> Constraint
FEATURE [Part::FeaturePython] _Element  # link proxy (typed FeaturePython)
  Detach = false
  LinkTransform = true
  LinkedObject = -> Link [Pocket003.Face2]
  _LinkVersion = 1
  _Parent = -> Elements
FEATURE [Part::FeaturePython] Element  label="mate l"  # link proxy (typed FeaturePython)
  Detach = false
  LinkTransform = true
  LinkedObject = -> Link [Sketch005.Edge1]
  _LinkVersion = 1
  _Parent = -> Elements
FEATURE [Part::FeaturePython] Element001  label="mate r"  # link proxy (typed FeaturePython)
  Detach = false
  LinkTransform = true
  LinkedObject = -> Link [Sketch005.Edge2]
  _LinkVersion = 1
  _Parent = -> Elements
FEATURE [App::FeaturePython] Constraint001  label="Attachment"  # WARN: FeaturePython — macro-defined, semantics opaque (R4)
  Cascade = false
  Disabled = false
  Group = -> [ElementLink001,ElementLink002]
  Multiply = false
  _ConstraintType = 45
  _LinkVersion = 0
  _Parent = -> Constraints
FEATURE [App::FeaturePython] ElementLink001  label="_Element001"  # link proxy (typed FeaturePython)
  LinkTransform = true
  LinkedObject = -> _Element001
  Offset = pos=(0,0,-6.5) rot=(1,0,0;3.14159rad)
  Placement = pos=(-9e-16,-6.5,21) rot=(1,0,0;3.14159rad)
  _LinkVersion = 0
  _Parent = -> Constraint001
FEATURE [Part::FeaturePython] _Element001  # link proxy (typed FeaturePython)
  Detach = false
  LinkTransform = true
  LinkedObject = -> Link001 [0.Edge9]
  _LinkVersion = 0
  _Parent = -> Elements
FEATURE [App::FeaturePython] ElementLink002  label="mate r"  # link proxy (typed FeaturePython)
  LinkTransform = true
  LinkedObject = -> Element001
  _LinkVersion = 0
  _Parent = -> Constraint001
FEATURE [App::FeaturePython] Constraint002  label="Attachment001"  # WARN: FeaturePython — macro-defined, semantics opaque (R4)
  Cascade = false
  Disabled = false
  Group = -> [ElementLink003,ElementLink004]
  Multiply = false
  _ConstraintType = 45
  _LinkVersion = 0
  _Parent = -> Constraints
FEATURE [App::FeaturePython] ElementLink003  label="_Element002"  # link proxy (typed FeaturePython)
  LinkTransform = true
  LinkedObject = -> _Element002
  Offset = pos=(0,0,-6.5) rot=(1,0,0;3.14159rad)
  Placement = pos=(9e-16,-6.5,21) rot=(1,0,0;3.14159rad)
  _LinkVersion = 0
  _Parent = -> Constraint002
FEATURE [Part::FeaturePython] _Element002  # link proxy (typed FeaturePython)
  Detach = false
  LinkTransform = true
  LinkedObject = -> Link001 [1.Edge9]
  _LinkVersion = 0
  _Parent = -> Elements
FEATURE [App::FeaturePython] ElementLink004  label="mate l"  # link proxy (typed FeaturePython)
  LinkTransform = true
  LinkedObject = -> Element
  _LinkVersion = 0
  _Parent = -> Constraint002
---- part parts/NEMA23-76.FCStd = doc fcstd_c19784181319 ----
FCSTD DOCUMENT  (FreeCAD 2021.614R24301 +3747 (Git))
Label: NEMA23-76
License: Creative Commons Attribution
LicenseURL: http://creativecommons.org/licenses/by/4.0/
objects: App::FeaturePython×32, Part::FeaturePython×28, Sketcher::SketchObject×14, PartDesign::Pad×5, App::Link×5, PartDesign::Pocket×4, PartDesign::Hole×4, App::LinkElement×4, PartDesign::Body×2, PartDesign::Fillet×1, PartDesign::Line×1, PartDesign::SubtractiveHelix×1, PartDesign::Chamfer×1, App::DocumentObjectGroup×1
note: 91 computed .brp shape members not serialized (recipe doc carries the construction recipe); baked Part::Feature solids carry a one-line shape summary decoded from their .brp

FEATURE [Sketcher::SketchObject] Sketch
  FullyConstrained = true
  MapMode = 5
  Support = -> [XY_Plane]
  sketch-geometry (16):
    g0: LineSegment StartX=-23.55 StartY=28.2 StartZ=0 EndX=23.55 EndY=28.2 EndZ=0
    g1: LineSegment StartX=28.2 StartY=23.55 StartZ=0 EndX=28.2 EndY=-23.55 EndZ=0
    g2: LineSegment StartX=23.55 StartY=-28.2 StartZ=0 EndX=-23.55 EndY=-28.2 EndZ=0
    g3: LineSegment StartX=-28.2 StartY=-23.55 StartZ=0 EndX=-28.2 EndY=23.55 EndZ=0
    g4: ArcOfCircle CenterX=-23.55 CenterY=23.55 CenterZ=0 NormalX=0 NormalY=0 NormalZ=1 AngleXU=0 Radius=4.65 StartAngle=1.5708 EndAngle=3.14159
    g5: GeomPoint [constr] X=-28.2 Y=28.2 Z=0
    g6: ArcOfCircle CenterX=23.55 CenterY=23.55 CenterZ=0 NormalX=0 NormalY=0 NormalZ=1 AngleXU=0 Radius=4.65 StartAngle=0 EndAngle=1.5708
    g7: GeomPoint [constr] X=28.2 Y=28.2 Z=0
    g8: ArcOfCircle CenterX=23.55 CenterY=-23.55 CenterZ=0 NormalX=0 NormalY=0 NormalZ=1 AngleXU=0 Radius=4.65 StartAngle=4.71239 EndAngle=6.28319
    g9: GeomPoint [constr] X=28.2 Y=-28.2 Z=0
    g10: ArcOfCircle CenterX=-23.55 CenterY=-23.55 CenterZ=0 NormalX=0 NormalY=0 NormalZ=1 AngleXU=0 Radius=4.65 StartAngle=3.14159 EndAngle=4.71239
    g11: GeomPoint [constr] X=-28.2 Y=-28.2 Z=0
    g12: Circle CenterX=-23.55 CenterY=23.55 CenterZ=0 NormalX=0 NormalY=0 NormalZ=1 AngleXU=0 Radius=2.55
    g13: Circle CenterX=23.55 CenterY=23.55 CenterZ=0 NormalX=0 NormalY=0 NormalZ=1 AngleXU=0 Radius=2.55
    g14: Circle CenterX=23.55 CenterY=-23.55 CenterZ=0 NormalX=0 NormalY=0 NormalZ=1 AngleXU=0 Radius=2.55
    g15: Circle CenterX=-23.55 CenterY=-23.55 CenterZ=0 NormalX=0 NormalY=0 NormalZ=1 AngleXU=0 Radius=2.55
  constraints (35):
    c: Horizontal(g0)
    c: Horizontal(g2)
    c: Vertical(g1)
    c: Vertical(g3)
    c: Symmetric(g9,g5,g-1)
    c: PointOnObject(g5,g0)
    c: PointOnObject(g5,g3)
    c: Tangent(g0,g4) = 1.5708
    c: Tangent(g3,g4) = 1.5708
    c: PointOnObject(g7,g0)
    c: PointOnObject(g7,g1)
    c: Tangent(g0,g6) = 1.5708
    c: Tangent(g1,g6) = 1.5708
    c: PointOnObject(g9,g1)
    c: PointOnObject(g9,g2)
    c: Tangent(g1,g8) = 1.5708
    c: Tangent(g2,g8) = 1.5708
    c: PointOnObject(g11,g2)
    c: PointOnObject(g11,g3)
    c: Tangent(g2,g10) = 1.5708
    c: Tangent(g3,g10) = 1.5708
    c: Equal(g10,g8)
    c: Equal(g8,g6)
    c: Equal(g6,g4)
    c: Equal(g0,g1)
    c: DistanceX(g3,g1) = 56.4
    c: Coincident(g12,g4)
    c: Coincident(g13,g6)
    c: Coincident(g14,g8)
    c: Coincident(g15,g10)
    c: Equal(g15,g14)
    c: Equal(g14,g13)
    c: Equal(g13,g12)
    c: Diameter(g12) = 5.1
    c: DistanceX(g4,g6) = 47.1
FEATURE [PartDesign::Pad] Pad
  ClaimChildren = false
  Direction = (1,1,1)
  Fit = 0
  FitJoin = 0
  InnerFit = 0
  InnerFitJoin = 0
  InnerTaperAngle = 0
  InnerTaperAngleRev = 0
  Length = 6
  Length2 = 100
  Linearize = true
  NewSolid = false
  Profile = -> Sketch
  Refine = true
  Suppress = false
  Type = 0
FEATURE [Sketcher::SketchObject] Sketch001
  ExternalGeometry = -> [Pad]
  FullyConstrained = true
  MapMode = 5
  Placement = pos=(0,0,6) rot=(0,0,1;0rad)
  Support = -> [Pad]
  sketch-geometry (16):
    g0: LineSegment StartX=-18.55 StartY=28.2 StartZ=0 EndX=18.55 EndY=28.2 EndZ=0
    g1: LineSegment StartX=28.2 StartY=18.55 StartZ=0 EndX=28.2 EndY=-18.55 EndZ=0
    g2: LineSegment StartX=18.55 StartY=-28.2 StartZ=0 EndX=-18.55 EndY=-28.2 EndZ=0
    g3: LineSegment StartX=-28.2 StartY=-18.55 StartZ=0 EndX=-28.2 EndY=18.55 EndZ=0
    g4: ArcOfCircle CenterX=-23.55 CenterY=23.55 CenterZ=0 NormalX=0 NormalY=0 NormalZ=1 AngleXU=0 Radius=5 StartAngle=4.71239 EndAngle=6.28319
    g5: ArcOfCircle CenterX=23.55 CenterY=23.55 CenterZ=0 NormalX=0 NormalY=0 NormalZ=1 AngleXU=0 Radius=5 StartAngle=3.14159 EndAngle=4.71239
    g6: ArcOfCircle CenterX=23.55 CenterY=-23.55 CenterZ=0 NormalX=0 NormalY=0 NormalZ=1 AngleXU=0 Radius=5 StartAngle=1.5708 EndAngle=3.14159
    g7: ArcOfCircle CenterX=-23.55 CenterY=-23.55 CenterZ=0 NormalX=0 NormalY=0 NormalZ=1 AngleXU=0 Radius=5 StartAngle=1e-16 EndAngle=1.5708
    g8: LineSegment StartX=-18.55 StartY=28.2 StartZ=0 EndX=-18.55 EndY=23.55 EndZ=0
    g9: LineSegment StartX=-23.55 StartY=18.55 StartZ=0 EndX=-28.2 EndY=18.55 EndZ=0
    g10: LineSegment StartX=18.55 StartY=23.55 StartZ=0 EndX=18.55 EndY=28.2 EndZ=0
    g11: LineSegment StartX=23.55 StartY=18.55 StartZ=0 EndX=28.2 EndY=18.55 EndZ=0
    g12: LineSegment StartX=23.55 StartY=-18.55 StartZ=0 EndX=28.2 EndY=-18.55 EndZ=0
    g13: LineSegment StartX=18.55 StartY=-23.55 StartZ=0 EndX=18.55 EndY=-28.2 EndZ=0
    g14: LineSegment StartX=-18.55 StartY=-23.55 StartZ=0 EndX=-18.55 EndY=-28.2 EndZ=0
    g15: LineSegment StartX=-23.55 StartY=-18.55 StartZ=0 EndX=-28.2 EndY=-18.55 EndZ=0
  constraints (40):
    c: Horizontal(g0)
    c: Horizontal(g2)
    c: Vertical(g1)
    c: Vertical(g3)
    c: Coincident(g4,g-4)
    c: Vertical(g7,g4)
    c: Horizontal(g4,g5)
    c: Vertical(g5,g6)
    c: Horizontal(g7,g6)
    c: Symmetric(g6,g4,g-1)
    c: Equal(g5,g4)
    c: Equal(g4,g7)
    c: Equal(g7,g6)
    c: Diameter(g4) = 10
    c: Vertical(g10)
    c: Horizontal(g11)
    c: Horizontal(g12)
    c: Vertical(g14)
    c: Vertical(g8)
    c: Horizontal(g9)
    c: Coincident(g0,g8)
    c: Coincident(g3,g9)
    c: Coincident(g0,g10)
    c: Coincident(g1,g11)
    c: Coincident(g1,g12)
    c: Coincident(g2,g13)
    c: Tangent(g6,g13) = -1.5708
    c: Coincident(g3,g15)
    c: Tangent(g7,g14) = 1.5708
    c: Coincident(g2,g14)
    c: Tangent(g7,g15) = -1.5708
    c: Tangent(g6,g12) = 1.5708
    c: Tangent(g5,g10) = 1.5708
    c: Tangent(g5,g11) = -1.5708
    c: Tangent(g4,g8) = 1.5708
    c: Tangent(g4,g9) = 1.5708
    c: Horizontal(g0,g-4)
    c: Vertical(g3,g-4)
    c: Symmetric(g2,g0,g-1)
    c: Symmetric(g1,g3,g-2)
FEATURE [PartDesign::Pad] Pad001
  BaseFeature = -> Pad
  ClaimChildren = false
  Direction = (1,1,1)
  Fit = 0
  FitJoin = 0
  InnerFit = 0
  InnerFitJoin = 0
  InnerTaperAngle = 0
  InnerTaperAngleRev = 0
  Length = 70
  Length2 = 100
  Linearize = true
  NewSolid = false
  Profile = -> Sketch001
  Refine = true
  Suppress = false
  Type = 0
FEATURE [Sketcher::SketchObject] Sketch002
  FullyConstrained = true
  MapMode = 5
  Placement = pos=(0,0,0) rot=(1,0,0;3.14159rad)
  Support = -> [Pad001]
  sketch-geometry (1):
    g0: Circle CenterX=0 CenterY=0 CenterZ=0 NormalX=0 NormalY=0 NormalZ=1 AngleXU=0 Radius=19.05
  constraints (2):
    c: Coincident(g0,g-1)
    c: Diameter(g0) = 38.1
FEATURE [PartDesign::Pad] Pad002
  BaseFeature = -> Pad001
  ClaimChildren = false
  Direction = (1,1,1)
  Fit = 0
  FitJoin = 0
  InnerFit = 0
  InnerFitJoin = 0
  InnerTaperAngle = 0
  InnerTaperAngleRev = 0
  Length = 1.6
  Length2 = 100
  Linearize = true
  NewSolid = false
  Profile = -> Sketch002
  Refine = true
  Suppress = false
  Type = 0
FEATURE [Sketcher::SketchObject] Sketch003
  FullyConstrained = true
  MapMode = 5
  Placement = pos=(0,0,-1.6) rot=(1,0,0;3.14159rad)
  Support = -> [Pad002]
  sketch-geometry (1):
    g0: Circle CenterX=0 CenterY=0 CenterZ=0 NormalX=0 NormalY=0 NormalZ=1 AngleXU=0 Radius=3.175
  constraints (2):
    c: Coincident(g0,g-1)
    c: Diameter(g0) = 6.35
FEATURE [PartDesign::Pad] Pad003
  BaseFeature = -> Pad002
  ClaimChildren = false
  Direction = (1,1,1)
  Fit = 0
  FitJoin = 0
  InnerFit = 0
  InnerFitJoin = 0
  InnerTaperAngle = 0
  InnerTaperAngleRev = 0
  Length = 20
  Length2 = 100
  Linearize = true
  NewSolid = false
  Profile = -> Sketch003
  Refine = true
  Suppress = false
  Type = 0
FEATURE [PartDesign::Fillet] Fillet
  Base = -> Pad003 [Edge71,Edge8,Edge6,Edge16,Edge14,Edge68,Edge67,Edge72,Edge39,Edge40,Edge43,Edge44,Edge15,Edge47,Edge7,Edge36]
  BaseFeature = -> Pad003
  NewSolid = false
  Radius = 1.5
  Refine = true
  SupportTransform = false
  Suppress = false
FEATURE [App::Link] Link  label="Link(Nema23)"
  AutoLinkLabel = true
  LinkedObject = -> Body
  SyncGroupVisibility = false
  _LinkVersion = 1
FEATURE [PartDesign::Line] DatumLine
  AttacherType = Attacher::AttachEngineLine
  Length = 97.6
  MapMode = 19
  MinimumLength = 10
  Placement = pos=(0,0,-21.6) rot=(-1,0,0;3.14159rad)
  ResizeMode = 0
  Support = -> [Fillet]
FEATURE [PartDesign::Body] Body  label="Nema23"
  AutoGroupSolids = false
  ExportMode = 0
  Group = -> [Sketch,Pad,Sketch001,Pad001,Sketch002,Pad002,Sketch003,Pad003,Fillet,DatumLine]
  Origin = -> Origin
  Tip = -> Fillet
  _ExportChildren = -> [Pad,Pad001,Pad002,Pad003,Fillet,DatumLine]
  _GroupVersion = 1
FEATURE [Sketcher::SketchObject] Sketch004
  FullyConstrained = true
  MapMode = 5
  Support = -> [XY_Plane001]
  sketch-geometry (1):
    g0: Circle CenterX=0 CenterY=0 CenterZ=0 NormalX=0 NormalY=0 NormalZ=1 AngleXU=0 Radius=12.5
  constraints (2):
    c: Coincident(g0,g-1)
    c: Diameter(g0) = 25
FEATURE [PartDesign::Pad] Pad004
  ClaimChildren = false
  Direction = (1,1,1)
  Fit = 0
  FitJoin = 0
  InnerFit = 0
  InnerFitJoin = 0
  InnerTaperAngle = 0
  InnerTaperAngleRev = 0
  Length = 30
  Length2 = 100
  Linearize = true
  Midplane = true
  NewSolid = false
  Profile = -> Sketch004
  Refine = true
  Suppress = false
  Type = 0
FEATURE [Sketcher::SketchObject] Sketch005
  FullyConstrained = true
  MapMode = 5
  Placement = pos=(0,0,15) rot=(0,0,1;0rad)
  Support = -> [Pad004]
  sketch-geometry (1):
    g0: Circle CenterX=0 CenterY=0 CenterZ=0 NormalX=0 NormalY=0 NormalZ=1 AngleXU=0 Radius=3.175
  constraints (2):
    c: Coincident(g0,g-1)
    c: Diameter(g0) = 6.35
FEATURE [PartDesign::Pocket] Pocket
  BaseFeature = -> Pad004
  ClaimChildren = false
  Fit = 0
  FitJoin = 0
  InnerFit = 0
  InnerFitJoin = 0
  InnerTaperAngle = 0
  InnerTaperAngleRev = 0
  Length = 5
  Length2 = 100
  Linearize = true
  NewSolid = false
  Profile = -> Sketch005
  Refine = true
  Suppress = false
  Type = 1
FEATURE [Sketcher::SketchObject] Sketch006
  FullyConstrained = true
  MapMode = 5
  Placement = pos=(0,0,15) rot=(0,0,1;0rad)
  Support = -> [Pocket]
  sketch-geometry (1):
    g0: Circle CenterX=0 CenterY=0 CenterZ=0 NormalX=0 NormalY=0 NormalZ=1 AngleXU=0 Radius=5
  constraints (2):
    c: Coincident(g0,g-1)
    c: Diameter(g0) = 10
FEATURE [PartDesign::Pocket] Pocket001
  BaseFeature = -> Pocket
  ClaimChildren = false
  Fit = 0
  FitJoin = 0
  InnerFit = 0
  InnerFitJoin = 0
  InnerTaperAngle = 0
  InnerTaperAngleRev = 0
  Length = 21.5
  Length2 = 100
  Linearize = true
  NewSolid = false
  Profile = -> Sketch006
  Refine = true
  Suppress = false
  Type = 0
FEATURE [Sketcher::SketchObject] Sketch007
  FullyConstrained = true
  MapMode = 5
  Placement = pos=(0,0,15) rot=(0,0,1;0rad)
  Support = -> [Pocket001]
  sketch-geometry (4):
    g0: LineSegment StartX=-11.5 StartY=0.5 StartZ=0 EndX=13.5 EndY=0.5 EndZ=0
    g1: LineSegment StartX=13.5 StartY=0.5 StartZ=0 EndX=13.5 EndY=-0.5 EndZ=0
    g2: LineSegment StartX=13.5 StartY=-0.5 StartZ=0 EndX=-11.5 EndY=-0.5 EndZ=0
    g3: LineSegment StartX=-11.5 StartY=-0.5 StartZ=0 EndX=-11.5 EndY=0.5 EndZ=0
  constraints (11):
    c: Coincident(g0,g1)
    c: Coincident(g1,g2)
    c: Coincident(g2,g3)
    c: Coincident(g3,g0)
    c: Horizontal(g0)
    c: Horizontal(g2)
    c: DistanceY(g1,g1) = 1
    c: Symmetric(g1,g0,g-1)
    c: DistanceX(g2,g2) = 25
    c: Vertical(g3)
    c: DistanceX(g2,g-1) = 11.5
FEATURE [Sketcher::SketchObject] Sketch008
  FullyConstrained = true
  MapMode = 5
  Placement = pos=(0,0,0) rot=(1,0,0;1.5708rad)
  Support = -> [XZ_Plane001]
  sketch-geometry (2):
    g0: Circle CenterX=0 CenterY=10 CenterZ=0 NormalX=0 NormalY=0 NormalZ=1 AngleXU=0 Radius=1.75
    g1: Circle CenterX=0 CenterY=-10 CenterZ=0 NormalX=0 NormalY=0 NormalZ=1 AngleXU=0 Radius=1.75
  constraints (5):
    c: PointOnObject(g0,g-2)
    c: Equal(g1,g0)
    c: Symmetric(g0,g1,g-1)
    c: DistanceY(g1,g0) = 20
    c: Diameter(g0) = 3.5
FEATURE [PartDesign::Hole] Hole
  BaseFeature = -> Pocket001
  ClaimChildren = false
  CustomThreadClearance = 0
  Depth = 25
  DepthType = 1
  Diameter = 4.5
  DrillForDepth = false
  DrillPoint = 1
  DrillPointAngle = 118
  Fit = 0
  FitJoin = 0
  HoleCutCountersinkAngle = 90
  HoleCutCustomValues = false
  HoleCutDepth = 0
  HoleCutDiameter = 6.1
  HoleCutType = 0
  InnerFit = 0
  InnerFitJoin = 0
  ModelThread = false
  NewSolid = false
  Profile = -> Sketch008
  Refine = true
  Reversed = true
  Suppress = false
  Tapered = false
  TaperedAngle = 90
  ThreadClass = 0
  ThreadDepth = 93.5288
  ThreadDepthType = 0
  ThreadDirection = 0
  ThreadFit = 0
  ThreadSize = 0
  ThreadType = 0
  Threaded = false
  UseCustomThreadClearance = false
FEATURE [Sketcher::SketchObject] Sketch009
  FullyConstrained = true
  MapMode = 5
  Placement = pos=(0,0,0) rot=(1,0,0;1.5708rad)
  Support = -> [XZ_Plane001]
  sketch-geometry (2):
    g0: Circle CenterX=8 CenterY=10 CenterZ=0 NormalX=0 NormalY=0 NormalZ=1 AngleXU=0 Radius=1.25
    g1: Circle CenterX=8 CenterY=-10 CenterZ=0 NormalX=0 NormalY=0 NormalZ=1 AngleXU=0 Radius=1.25
  constraints (5):
    c: Symmetric(g0,g1,g-1)
    c: DistanceX(g-1,g0) = 8
    c: DistanceY(g1,g0) = 20
    c: Equal(g0,g1)
    c: Diameter(g0) = 2.5
FEATURE [Sketcher::SketchObject] Sketch010
  FullyConstrained = true
  MapMode = 5
  Placement = pos=(0,0,0) rot=(1,0,0;1.5708rad)
  Support = -> [XZ_Plane001]
  sketch-geometry (2):
    g0: Circle CenterX=8 CenterY=10 CenterZ=0 NormalX=0 NormalY=0 NormalZ=1 AngleXU=0 Radius=1.25
    g1: Circle CenterX=8 CenterY=-10 CenterZ=0 NormalX=0 NormalY=0 NormalZ=1 AngleXU=0 Radius=1.25
  constraints (5):
    c: Symmetric(g0,g1,g-1)
    c: DistanceX(g-1,g0) = 8
    c: DistanceY(g1,g0) = 20
    c: Equal(g0,g1)
    c: Diameter(g0) = 2.5
FEATURE [Sketcher::SketchObject] Sketch011
  AttachmentOffset = pos=(0,0,-4) rot=(0,0,1;0rad)
  FullyConstrained = true
  MapMode = 5
  Placement = pos=(0,4,9e-16) rot=(1,0,0;1.5708rad)
  Support = -> [XZ_Plane001]
  sketch-geometry (2):
    g0: Circle CenterX=8 CenterY=10 CenterZ=0 NormalX=0 NormalY=0 NormalZ=1 AngleXU=0 Radius=1.25
    g1: Circle CenterX=8 CenterY=-10 CenterZ=0 NormalX=0 NormalY=0 NormalZ=1 AngleXU=0 Radius=1.25
  constraints (5):
    c: Symmetric(g0,g1,g-1)
    c: DistanceX(g-1,g0) = 8
    c: DistanceY(g1,g0) = 20
    c: Equal(g0,g1)
    c: Diameter(g0) = 2.5
FEATURE [PartDesign::Hole] Hole001
  BaseFeature = -> Hole
  ClaimChildren = false
  CustomThreadClearance = 0
  Depth = 25
  DepthType = 1
  Diameter = 2.5
  DrillForDepth = false
  DrillPoint = 1
  DrillPointAngle = 118
  Fit = 0
  FitJoin = 0
  HoleCutCountersinkAngle = 90
  HoleCutCustomValues = false
  HoleCutDepth = 0
  HoleCutDiameter = 6.1
  HoleCutType = 0
  InnerFit = 0
  InnerFitJoin = 0
  ModelThread = false
  NewSolid = false
  Profile = -> Sketch009
  Refine = true
  Reversed = true
  Suppress = false
  Tapered = false
  TaperedAngle = 90
  ThreadClass = 0
  ThreadDepth = 93.5621
  ThreadDepthType = 0
  ThreadDirection = 0
  ThreadFit = 0
  ThreadSize = 0
  ThreadType = 0
  Threaded = false
  UseCustomThreadClearance = false
FEATURE [PartDesign::Hole] Hole002
  BaseFeature = -> Hole001
  ClaimChildren = false
  CustomThreadClearance = 0
  Depth = 25
  DepthType = 1
  Diameter = 3.1
  DrillForDepth = false
  DrillPoint = 1
  DrillPointAngle = 118
  Fit = 0
  FitJoin = 0
  HoleCutCountersinkAngle = 90
  HoleCutCustomValues = false
  HoleCutDepth = 0
  HoleCutDiameter = 6.1
  HoleCutType = 0
  InnerFit = 0
  InnerFitJoin = 0
  ModelThread = false
  NewSolid = false
  Profile = -> Sketch010
  Refine = true
  Suppress = false
  Tapered = false
  TaperedAngle = 90
  ThreadClass = 0
  ThreadDepth = 93.56
  ThreadDepthType = 0
  ThreadDirection = 0
  ThreadFit = 0
  ThreadSize = 0
  ThreadType = 0
  Threaded = false
  UseCustomThreadClearance = false
FEATURE [PartDesign::Hole] Hole003
  BaseFeature = -> Hole002
  ClaimChildren = false
  CustomThreadClearance = 0
  Depth = 25
  DepthType = 1
  Diameter = 6
  DrillForDepth = false
  DrillPoint = 1
  DrillPointAngle = 118
  Fit = 0
  FitJoin = 0
  HoleCutCountersinkAngle = 90
  HoleCutCustomValues = false
  HoleCutDepth = 0
  HoleCutDiameter = 6.1
  HoleCutType = 0
  InnerFit = 0
  InnerFitJoin = 0
  ModelThread = false
  NewSolid = false
  Profile = -> Sketch011
  Refine = true
  Suppress = false
  Tapered = false
  TaperedAngle = 90
  ThreadClass = 0
  ThreadDepth = 93.56
  ThreadDepthType = 0
  ThreadDirection = 0
  ThreadFit = 0
  ThreadSize = 0
  ThreadType = 0
  Threaded = false
  UseCustomThreadClearance = false
FEATURE [Sketcher::SketchObject] Sketch012
  AttachmentOffset = pos=(0,0,0) rot=(0,1,0;0.349066rad)
  ExternalGeometry = -> [Hole003]
  FullyConstrained = true
  MapMode = 5
  Placement = pos=(0,0,0) rot=(0.443713,0.633687,0.633687;2.30637rad)
  Support = -> [YZ_Plane001]
  sketch-geometry (4):
    g0: LineSegment StartX=4 StartY=-6.25 StartZ=0 EndX=14 EndY=-6.25 EndZ=0
    g1: LineSegment StartX=14 StartY=-6.25 StartZ=0 EndX=14 EndY=-6.75 EndZ=0
    g2: LineSegment StartX=14 StartY=-6.75 StartZ=0 EndX=4 EndY=-6.75 EndZ=0
    g3: LineSegment StartX=4 StartY=-6.75 StartZ=0 EndX=4 EndY=-6.25 EndZ=0
  constraints (12):
    c: Coincident(g0,g1)
    c: Coincident(g1,g2)
    c: Coincident(g2,g3)
    c: Coincident(g3,g0)
    c: Horizontal(g0)
    c: Horizontal(g2)
    c: Vertical(g1)
    c: Vertical(g3)
    c: DistanceY(g1,g1) = 0.5
    c: DistanceX(g2,g2) = 10
    c: DistanceX(g-1,g0) = 4
    c: DistanceY(g-3,g2) = 8.25
FEATURE [PartDesign::SubtractiveHelix] SubtractiveHelix
  Angle = 0
  Axis = (-2e-16,2e-16,1)
  Base = (0,0,0)
  BaseFeature = -> Hole003
  ClaimChildren = false
  Fit = 0
  FitJoin = 0
  HasBeenEdited = true
  Height = 13
  InnerFit = 0
  InnerFitJoin = 0
  LeftHanded = false
  Mode = 0
  NewSolid = false
  Outside = false
  Pitch = 3
  Profile = -> Sketch012
  ReferenceAxis = -> Sketch012 [V_Axis]
  Refine = true
  Suppress = false
  Turns = 3
FEATURE [PartDesign::Pocket] Pocket002
  BaseFeature = -> SubtractiveHelix
  ClaimChildren = false
  Fit = 0
  FitJoin = 0
  InnerFit = 0
  InnerFitJoin = 0
  InnerTaperAngle = 0
  InnerTaperAngleRev = 0
  Length = 10.5
  Length2 = 100
  Linearize = true
  NewSolid = false
  Profile = -> Sketch007
  Refine = true
  Suppress = false
  Type = 0
FEATURE [Sketcher::SketchObject] Sketch013
  FullyConstrained = true
  MapMode = 5
  Placement = pos=(0,0,-15) rot=(1,0,0;3.14159rad)
  Support = -> [Pocket002]
  sketch-geometry (4):
    g0: LineSegment StartX=-11.5 StartY=0.5 StartZ=0 EndX=13.5 EndY=0.5 EndZ=0
    g1: LineSegment StartX=13.5 StartY=0.5 StartZ=0 EndX=13.5 EndY=-0.5 EndZ=0
    g2: LineSegment StartX=13.5 StartY=-0.5 StartZ=0 EndX=-11.5 EndY=-0.5 EndZ=0
    g3: LineSegment StartX=-11.5 StartY=-0.5 StartZ=0 EndX=-11.5 EndY=0.5 EndZ=0
  constraints (11):
    c: Coincident(g0,g1)
    c: Coincident(g1,g2)
    c: Coincident(g2,g3)
    c: Coincident(g3,g0)
    c: Horizontal(g0)
    c: Horizontal(g2)
    c: Vertical(g3)
    c: DistanceY(g1,g1) = 1
    c: Symmetric(g1,g0,g-1)
    c: DistanceX(g2,g2) = 25
    c: DistanceX(g2,g-1) = 11.5
FEATURE [PartDesign::Pocket] Pocket003
  BaseFeature = -> Pocket002
  ClaimChildren = false
  Fit = 0
  FitJoin = 0
  InnerFit = 0
  InnerFitJoin = 0
  InnerTaperAngle = 0
  InnerTaperAngleRev = 0
  Length = 10
  Length2 = 100
  Linearize = true
  NewSolid = false
  Profile = -> Sketch013
  Refine = true
  Suppress = false
  Type = 0
FEATURE [App::Link] Link001  label="Link001(Coupling)"
  AutoLinkLabel = true
  LinkedObject = -> Body001
  SyncGroupVisibility = false
  _LinkVersion = 1
FEATURE [Part::FeaturePython] Screw  label="M3x12-Screw"  # Fasteners workbench fastener (typed FeaturePython)
  Placement = pos=(8,4,-10) rot=(0,0.707107,0.707107;3.14159rad)
  diameter = 4
  invert = false
  length = 4
  lengthCustom = 12
  matchOuter = false
  offset = 0
  thread = false
  type = 33
FEATURE [Part::FeaturePython] Screw001  label="M4x8-Screw"  # Fasteners workbench fastener (typed FeaturePython)
  Placement = pos=(0,-10.23,-10) rot=(1,0,0;1.5708rad)
  diameter = 7
  invert = false
  length = 3
  lengthCustom = 8
  matchOuter = false
  offset = 0
  thread = false
  type = 29
FEATURE [App::Link] Link002  label="Link002(M4x8-Screw)"
  AutoLinkLabel = true
  LinkPlacement = pos=(0,-12.23,10) rot=(1,0,0;1.5708rad)
  LinkedObject = -> Screw001
  Placement = pos=(0,-12.23,10) rot=(1,0,0;1.5708rad)
  SyncGroupVisibility = false
  _LinkVersion = 1
FEATURE [App::Link] Link003  label="Link003(M3x12-Screw)"
  AutoLinkLabel = true
  LinkPlacement = pos=(8,4,10) rot=(0,0.707107,0.707107;3.14159rad)
  LinkedObject = -> Screw
  Placement = pos=(8,4,10) rot=(0,0.707107,0.707107;3.14159rad)
  SyncGroupVisibility = false
  _LinkVersion = 1
FEATURE [Part::FeaturePython] Parts001  # WARN: FeaturePython — macro-defined, semantics opaque (R4)
  Group = -> [Link001,Screw,Screw001,Link002,Link003]
  GroupMode = 0
  _LinkVersion = 1
FEATURE [PartDesign::Chamfer] Chamfer
  Angle = 45
  Base = -> Pocket003 [Edge115,Edge1,Edge17,Edge21,Edge138,Edge143]
  BaseFeature = -> Pocket003
  ChamferType = 0
  FlipDirection = false
  NewSolid = false
  Refine = true
  Size = 0.5
  Size2 = 1
  SupportTransform = false
  Suppress = false
FEATURE [PartDesign::Body] Body001  label="Coupling"
  AutoGroupSolids = false
  ExportMode = 0
  Group = -> [Sketch004,Pad004,Sketch005,Pocket,Sketch006,Pocket001,Sketch007,Sketch008,Hole,Sketch009,Sketch010,Sketch011,Hole001,Hole002,Hole003,Sketch012,SubtractiveHelix,Pocket002,Sketch013,Pocket003,Chamfer]
  Origin = -> Origin001
  Placement = pos=(0,0,-51) rot=(0,0,1;0rad)
  Tip = -> Chamfer
  _ExportChildren = -> [Pad004,Pocket,Pocket001,Hole,Hole001,Hole002,Hole003,SubtractiveHelix,Pocket002,Pocket003,Chamfer]
  _GroupVersion = 1
FEATURE [Part::FeaturePython] Screw002  label="M5x16-Screw"  # Fasteners workbench fastener (typed FeaturePython)
  diameter = 6
  invert = false
  length = 4
  lengthCustom = 16
  matchOuter = false
  offset = 0
  thread = false
  type = 33
FEATURE [App::DocumentObjectGroup] Group  label="Components"
  ExportMode = 1
  Group = -> [Body001,Body,Screw002]
  _GroupVersion = 1
FEATURE [App::LinkElement] Link004_i0
  LinkPlacement = pos=(23.55,67.55,6) rot=(0,0,1;0rad)
  LinkedObject = -> Screw002
  Placement = pos=(23.55,67.55,6) rot=(0,0,1;0rad)
  _LinkVersion = 1
FEATURE [App::LinkElement] Link004_i1
  LinkPlacement = pos=(-23.55,67.55,6) rot=(0,0,1;0rad)
  LinkedObject = -> Screw002
  Placement = pos=(-23.55,67.55,6) rot=(0,0,1;0rad)
  _LinkVersion = 1
FEATURE [App::LinkElement] Link004_i2
  LinkPlacement = pos=(-23.55,20.45,6) rot=(0,0,1;0rad)
  LinkedObject = -> Screw002
  Placement = pos=(-23.55,20.45,6) rot=(0,0,1;0rad)
  _LinkVersion = 1
FEATURE [App::LinkElement] Link004_i3
  LinkPlacement = pos=(23.55,20.45,6) rot=(0,0,1;0rad)
  LinkedObject = -> Screw002
  Placement = pos=(23.55,20.45,6) rot=(0,0,1;0rad)
  _LinkVersion = 1
FEATURE [App::Link] Link004  label="M5x16-Screw 4ct"
  AutoLinkLabel = true
  ElementCount = 4
  ElementList = -> [Link004_i0,Link004_i1,Link004_i2,Link004_i3]
  LinkPlacement = pos=(0,-44,0) rot=(0,0,1;0rad)
  LinkedObject = -> Screw002
  Placement = pos=(0,-44,0) rot=(0,0,1;0rad)
  SyncGroupVisibility = false
  _LinkVersion = 1
FEATURE [Part::FeaturePython] Parts  # WARN: FeaturePython — macro-defined, semantics opaque (R4)
  Group = -> [Link,Link004]
  GroupMode = 0
  _LinkVersion = 1
FEATURE [Part::FeaturePython] Assembly  label="NEMA23-76-Assembly"  # WARN: FeaturePython — macro-defined, semantics opaque (R4)
  AutoRelax = true
  BuildShape = 0
  Freeze = false
  Group = -> [Constraints,Elements,Parts]
  Verbose = false
  _LinkVersion = 1
  _SolverType = 1
  _Version = 1
FEATURE [App::FeaturePython] Constraints  # WARN: FeaturePython — macro-defined, semantics opaque (R4)
  Group = -> [Constraint004,Constraint006,Constraint007,Constraint008,Constraint009]
  _LinkVersion = 1
  _Version = 1
FEATURE [App::FeaturePython] Elements  # WARN: FeaturePython — macro-defined, semantics opaque (R4)
  Group = -> [Element,Element001,Element002,Element003,Element004,Element005,Element010,_Element006,_Element007,_Element008,_Element009]
  _LinkVersion = 1
FEATURE [Part::FeaturePython] Element  # link proxy (typed FeaturePython)
  Detach = false
  LinkTransform = true
  LinkedObject = -> Link [Fillet.Edge19]
  _LinkVersion = 1
  _Parent = -> Elements
FEATURE [Part::FeaturePython] Element001  # link proxy (typed FeaturePython)
  Detach = false
  LinkTransform = true
  LinkedObject = -> Link [Fillet.Edge49]
  _LinkVersion = 1
  _Parent = -> Elements
FEATURE [Part::FeaturePython] Element002  # link proxy (typed FeaturePython)
  Detach = false
  LinkTransform = true
  LinkedObject = -> Link [Fillet.Edge101]
  _LinkVersion = 1
  _Parent = -> Elements
FEATURE [Part::FeaturePython] Element003  # link proxy (typed FeaturePython)
  Detach = false
  LinkTransform = true
  LinkedObject = -> Link [Fillet.Edge103]
  _LinkVersion = 1
  _Parent = -> Elements
FEATURE [Part::FeaturePython] Element004  label="bracket-mate"  # link proxy (typed FeaturePython)
  Detach = false
  LinkTransform = true
  LinkedObject = -> Link [Fillet.Edge36]
  _LinkVersion = 1
  _Parent = -> Elements
FEATURE [Part::FeaturePython] Element005  label="Axis"  # link proxy (typed FeaturePython)
  Detach = false
  LinkTransform = true
  LinkedObject = -> Link [DatumLine.]
  _LinkVersion = 1
  _Parent = -> Elements
FEATURE [Part::FeaturePython] Assembly001  label="Coupling-Assembly"  # WARN: FeaturePython — macro-defined, semantics opaque (R4)
  AutoRelax = true
  BuildShape = 0
  Freeze = false
  Group = -> [Constraints001,Elements001,Parts001]
  Placement = pos=(0,5.84137e-06,-49) rot=(0,0,1;0rad)
  Verbose = false
  _LinkVersion = 1
  _SolverType = 1
  _Version = 1
FEATURE [App::FeaturePython] Constraints001  # WARN: FeaturePython — macro-defined, semantics opaque (R4)
  Group = -> [Constraint,Constraint001,Constraint002,Constraint003,Constraint005]
  _LinkVersion = 1
  _Version = 1
FEATURE [App::FeaturePython] Elements001  # WARN: FeaturePython — macro-defined, semantics opaque (R4)
  Group = -> [Element006,Element007,_Element,_Element001,_Element002,_Element003,_Element004,_Element005,Element008,Element009]
  _LinkVersion = 1
FEATURE [Part::FeaturePython] Element006  # link proxy (typed FeaturePython)
  Detach = false
  LinkTransform = true
  LinkedObject = -> Link001 [Hole.Sketch008.Edge2]
  Offset = pos=(0,0,3) rot=(0,0,1;0rad)
  Placement = pos=(0,-3,0) rot=(0,0,1;0rad)
  _LinkVersion = 1
  _Parent = -> Elements001
FEATURE [Part::FeaturePython] Element007  # link proxy (typed FeaturePython)
  Detach = false
  LinkTransform = true
  LinkedObject = -> Link001 [Hole.Sketch008.Edge1]
  Offset = pos=(0,0,5) rot=(0,0,1;0rad)
  Placement = pos=(0,-5,1.8e-15) rot=(0,0,1;0rad)
  _LinkVersion = 1
  _Parent = -> Elements001
FEATURE [App::FeaturePython] Constraint  label="Attachment"  # WARN: FeaturePython — macro-defined, semantics opaque (R4)
  Cascade = false
  Disabled = false
  Group = -> [ElementLink,ElementLink001]
  Multiply = false
  _ConstraintType = 45
  _LinkVersion = 1
  _Parent = -> Constraints001
FEATURE [App::FeaturePython] ElementLink  label="_Element"  # link proxy (typed FeaturePython)
  LinkTransform = true
  LinkedObject = -> _Element
  _LinkVersion = 1
  _Parent = -> Constraint
FEATURE [Part::FeaturePython] _Element  # link proxy (typed FeaturePython)
  Detach = false
  LinkTransform = true
  LinkedObject = -> Link001 [Pocket003.Edge106]
  _LinkVersion = 1
  _Parent = -> Elements001
FEATURE [App::FeaturePython] ElementLink001  label="_Element001"  # link proxy (typed FeaturePython)
  LinkTransform = true
  LinkedObject = -> _Element001
  _LinkVersion = 1
  _Parent = -> Constraint
FEATURE [Part::FeaturePython] _Element001  # link proxy (typed FeaturePython)
  Detach = false
  LinkTransform = true
  LinkedObject = -> Screw [Edge9]
  _LinkVersion = 1
  _Parent = -> Elements001
FEATURE [App::FeaturePython] Constraint001  label="Attachment001"  # WARN: FeaturePython — macro-defined, semantics opaque (R4)
  Cascade = false
  Disabled = false
  Group = -> [ElementLink002,ElementLink003]
  Multiply = false
  _ConstraintType = 45
  _LinkVersion = 1
  _Parent = -> Constraints001
FEATURE [App::FeaturePython] ElementLink002  label="_Element002"  # link proxy (typed FeaturePython)
  LinkTransform = true
  LinkedObject = -> _Element002
  _LinkVersion = 1
  _Parent = -> Constraint001
FEATURE [Part::FeaturePython] _Element002  # link proxy (typed FeaturePython)
  Detach = false
  LinkTransform = true
  LinkedObject = -> Link001 [Pocket003.Edge174]
  _LinkVersion = 1
  _Parent = -> Elements001
FEATURE [App::FeaturePython] ElementLink003  label="_Element003"  # link proxy (typed FeaturePython)
  LinkTransform = true
  LinkedObject = -> _Element003
  _LinkVersion = 1
  _Parent = -> Constraint001
FEATURE [Part::FeaturePython] _Element003  # link proxy (typed FeaturePython)
  Detach = false
  LinkTransform = true
  LinkedObject = -> Link003 [Edge9]
  _LinkVersion = 1
  _Parent = -> Elements001
FEATURE [App::FeaturePython] Constraint002  label="Attachment002"  # WARN: FeaturePython — macro-defined, semantics opaque (R4)
  Cascade = false
  Disabled = false
  Group = -> [ElementLink004,ElementLink005]
  Multiply = false
  _ConstraintType = 45
  _LinkVersion = 1
  _Parent = -> Constraints001
FEATURE [App::FeaturePython] ElementLink004  label="Element006"  # link proxy (typed FeaturePython)
  LinkTransform = true
  LinkedObject = -> Element006
  _LinkVersion = 1
  _Parent = -> Constraint002
FEATURE [App::FeaturePython] ElementLink005  label="_Element004"  # link proxy (typed FeaturePython)
  LinkTransform = true
  LinkedObject = -> _Element004
  _LinkVersion = 1
  _Parent = -> Constraint002
FEATURE [Part::FeaturePython] _Element004  # link proxy (typed FeaturePython)
  Detach = false
  LinkTransform = true
  LinkedObject = -> Screw001 [Edge10]
  _LinkVersion = 1
  _Parent = -> Elements001
FEATURE [App::FeaturePython] Constraint003  label="Attachment003"  # WARN: FeaturePython — macro-defined, semantics opaque (R4)
  Cascade = false
  Disabled = false
  Group = -> [ElementLink006,ElementLink007]
  Multiply = false
  _ConstraintType = 45
  _LinkVersion = 1
  _Parent = -> Constraints001
FEATURE [App::FeaturePython] ElementLink006  label="Element007"  # link proxy (typed FeaturePython)
  LinkTransform = true
  LinkedObject = -> Element007
  _LinkVersion = 1
  _Parent = -> Constraint003
FEATURE [App::FeaturePython] ElementLink007  label="_Element005"  # link proxy (typed FeaturePython)
  LinkTransform = true
  LinkedObject = -> _Element005
  _LinkVersion = 1
  _Parent = -> Constraint003
FEATURE [Part::FeaturePython] _Element005  # link proxy (typed FeaturePython)
  Detach = false
  LinkTransform = true
  LinkedObject = -> Link002 [Edge10]
  _LinkVersion = 1
  _Parent = -> Elements001
FEATURE [Part::FeaturePython] Element008  label="motor-mate"  # link proxy (typed FeaturePython)
  Detach = false
  LinkTransform = true
  LinkedObject = -> Link001 [Pocket.Sketch005.]
  Offset = pos=(0,0,-21) rot=(0,0,1;0rad)
  Placement = pos=(0,0,-21) rot=(0,0,1;0rad)
  _LinkVersion = 1
  _Parent = -> Elements001
FEATURE [Part::FeaturePython] Element009  label="screw-mate"  # link proxy (typed FeaturePython)
  Detach = false
  LinkTransform = true
  LinkedObject = -> Link001 [Pocket.Sketch005.]
  Offset = pos=(0,0,-10) rot=(0,0,1;0rad)
  Placement = pos=(0,0,-10) rot=(0,0,1;0rad)
  _LinkVersion = 1
  _Parent = -> Elements001
FEATURE [Part::FeaturePython] Element010  label="coupling-mate"  # link proxy (typed FeaturePython)
  Detach = false
  LinkTransform = true
  LinkedObject = -> Link [Fillet.Edge170]
  _LinkVersion = 1
  _Parent = -> Elements
FEATURE [App::FeaturePython] Constraint004  label="Locked"  # WARN: FeaturePython — macro-defined, semantics opaque (R4)
  Disabled = false
  Group = -> [ElementLink008]
  _ConstraintType = 0
  _LinkVersion = 1
  _Parent = -> Constraints
FEATURE [App::FeaturePython] ElementLink008  label="coupling-mate"  # link proxy (typed FeaturePython)
  LinkTransform = true
  LinkedObject = -> Element010
  _LinkVersion = 1
  _Parent = -> Constraint004
FEATURE [App::FeaturePython] Constraint005  label="Locked001"  # WARN: FeaturePython — macro-defined, semantics opaque (R4)
  Disabled = false
  Group = -> [ElementLink009]
  _ConstraintType = 0
  _LinkVersion = 1
  _Parent = -> Constraints001
FEATURE [App::FeaturePython] ElementLink009  label="motor-mate"  # link proxy (typed FeaturePython)
  LinkTransform = true
  LinkedObject = -> Element008
  _LinkVersion = 1
  _Parent = -> Constraint005
FEATURE [App::FeaturePython] Constraint006  label="Attachment004"  # WARN: FeaturePython — macro-defined, semantics opaque (R4)
  Cascade = false
  Disabled = false
  Group = -> [ElementLink010,ElementLink011]
  Multiply = false
  _ConstraintType = 45
  _LinkVersion = 1
  _Parent = -> Constraints
FEATURE [App::FeaturePython] ElementLink010  label="_Element006"  # link proxy (typed FeaturePython)
  LinkTransform = true
  LinkedObject = -> _Element006
  _LinkVersion = 1
  _Parent = -> Constraint006
FEATURE [Part::FeaturePython] _Element006  # link proxy (typed FeaturePython)
  Detach = false
  LinkTransform = true
  LinkedObject = -> Link004 [0.Edge9]
  _LinkVersion = 1
  _Parent = -> Elements
FEATURE [App::FeaturePython] ElementLink011  label="Element"  # link proxy (typed FeaturePython)
  LinkTransform = true
  LinkedObject = -> Element
  _LinkVersion = 1
  _Parent = -> Constraint006
FEATURE [App::FeaturePython] Constraint007  label="Attachment005"  # WARN: FeaturePython — macro-defined, semantics opaque (R4)
  Cascade = false
  Disabled = false
  Group = -> [ElementLink012,ElementLink013]
  Multiply = false
  _ConstraintType = 45
  _LinkVersion = 1
  _Parent = -> Constraints
FEATURE [App::FeaturePython] ElementLink012  label="_Element007"  # link proxy (typed FeaturePython)
  LinkTransform = true
  LinkedObject = -> _Element007
  _LinkVersion = 1
  _Parent = -> Constraint007
FEATURE [Part::FeaturePython] _Element007  # link proxy (typed FeaturePython)
  Detach = false
  LinkTransform = true
  LinkedObject = -> Link004 [1.Edge9]
  _LinkVersion = 1
  _Parent = -> Elements
FEATURE [App::FeaturePython] ElementLink013  label="Element001"  # link proxy (typed FeaturePython)
  LinkTransform = true
  LinkedObject = -> Element001
  _LinkVersion = 1
  _Parent = -> Constraint007
FEATURE [App::FeaturePython] Constraint008  label="Attachment006"  # WARN: FeaturePython — macro-defined, semantics opaque (R4)
  Cascade = false
  Disabled = false
  Group = -> [ElementLink014,ElementLink015]
  Multiply = false
  _ConstraintType = 45
  _LinkVersion = 1
  _Parent = -> Constraints
FEATURE [App::FeaturePython] ElementLink014  label="_Element008"  # link proxy (typed FeaturePython)
  LinkTransform = true
  LinkedObject = -> _Element008
  _LinkVersion = 1
  _Parent = -> Constraint008
FEATURE [Part::FeaturePython] _Element008  # link proxy (typed FeaturePython)
  Detach = false
  LinkTransform = true
  LinkedObject = -> Link004 [2.Edge9]
  _LinkVersion = 1
  _Parent = -> Elements
FEATURE [App::FeaturePython] ElementLink015  label="Element002"  # link proxy (typed FeaturePython)
  LinkTransform = true
  LinkedObject = -> Element002
  _LinkVersion = 1
  _Parent = -> Constraint008
FEATURE [App::FeaturePython] Constraint009  label="Attachment007"  # WARN: FeaturePython — macro-defined, semantics opaque (R4)
  Cascade = false
  Disabled = false
  Group = -> [ElementLink016,ElementLink017]
  Multiply = false
  _ConstraintType = 45
  _LinkVersion = 1
  _Parent = -> Constraints
FEATURE [App::FeaturePython] ElementLink016  label="_Element009"  # link proxy (typed FeaturePython)
  LinkTransform = true
  LinkedObject = -> _Element009
  _LinkVersion = 1
  _Parent = -> Constraint009
FEATURE [Part::FeaturePython] _Element009  # link proxy (typed FeaturePython)
  Detach = false
  LinkTransform = true
  LinkedObject = -> Link004 [3.Edge9]
  _LinkVersion = 1
  _Parent = -> Elements
FEATURE [App::FeaturePython] ElementLink017  label="Element003"  # link proxy (typed FeaturePython)
  LinkTransform = true
  LinkedObject = -> Element003
  _LinkVersion = 1
  _Parent = -> Constraint009
